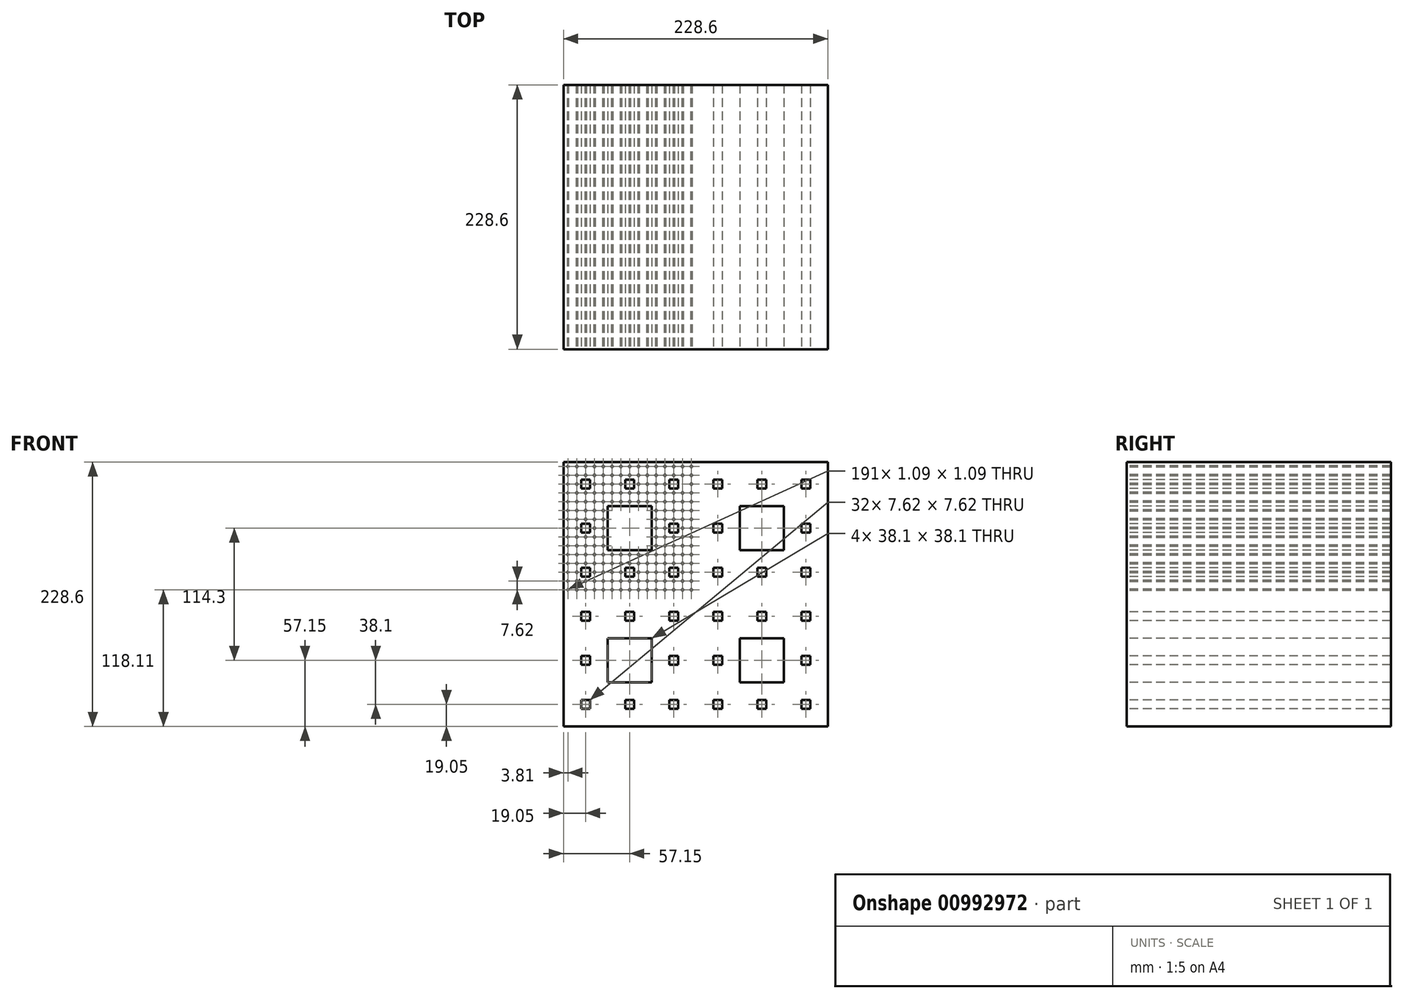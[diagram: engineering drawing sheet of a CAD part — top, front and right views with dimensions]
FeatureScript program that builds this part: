
annotation { "Feature Type Name" : "Feature", "Feature Type Description" : "" }
export const myFeature = defineFeature(function(context is Context, id is Id, definition is map)
    precondition{}
    {
        {
            var Q0;
            Q0=qCreatedBy(makeId("Front.planeOp"),FACE);
            var sketch = newSketch(context, id + "F0", { "sketchPlane" : qUnion([Q0])});
            skLineSegment(sketch, "E0.bottom", {"start": v(114.3, 114.3) * mm, "end": v(-114.3, 114.3) * mm});
            skLineSegment(sketch, "E0.top", {"start": v(114.3, -114.3) * mm, "end": v(-114.3, -114.3) * mm});
            skLineSegment(sketch, "E0.left", {"start": v(114.3, 114.3) * mm, "end": v(114.3, -114.3) * mm});
            skLineSegment(sketch, "E0.right", {"start": v(-114.3, 114.3) * mm, "end": v(-114.3, -114.3) * mm});
            skPoint(sketch, "E0.middle", {"position": v(0, 0) * mm});
            skSolve(sketch);
        }
        {
            var Q0;
            Q0 = qSketchRegion(id + "F0", true);
            extrude(context, id + "F1", {"entities" : qUnion([Q0]), "endBound" : BoundingType.SYMMETRIC, "depth" : 228.6 * mm, "offsetDistance" : 25.4 * mm});
        }
        {
            var Q0;
            Q0=makeQuery(id+"F1.opExtrude","CAP_FACE",FACE,{"disambiguationData":[OSD([sQuery(id+"F0.wireOp",EDGE,"E0.bottom"),sQuery(id+"F0.wireOp",EDGE,"E0.top"),sQuery(id+"F0.wireOp",EDGE,"E0.left"),sQuery(id+"F0.wireOp",EDGE,"E0.right")])],"isStart":false});
            var sketch = newSketch(context, id + "F2", { "sketchPlane" : qUnion([Q0])});
            skLineSegment(sketch, "E1", {"start": v(0, -114.3) * mm, "end": v(0, 114.3) * mm, "construction": true});
            skLineSegment(sketch, "E2", {"start": v(-114.3, 0) * mm, "end": v(114.3, 0) * mm, "construction": true});
            skLineSegment(sketch, "E3.bottom", {"start": v(-38.1, 76.2) * mm, "end": v(-76.2, 76.2) * mm});
            skLineSegment(sketch, "E3.top", {"start": v(-38.1, 38.1) * mm, "end": v(-76.2, 38.1) * mm});
            skLineSegment(sketch, "E3.left", {"start": v(-38.1, 76.2) * mm, "end": v(-38.1, 38.1) * mm});
            skLineSegment(sketch, "E3.right", {"start": v(-76.2, 76.2) * mm, "end": v(-76.2, 38.1) * mm});
            skPoint(sketch, "E4", {"position": v(-57.15, 95.25) * mm});
            skLineSegment(sketch, "E5.top", {"start": v(-38.1, 114.3) * mm, "end": v(-76.2, 114.3) * mm});
            skLineSegment(sketch, "E5.left", {"start": v(-38.1, 76.2) * mm, "end": v(-38.1, 114.3) * mm, "construction": true});
            skLineSegment(sketch, "E5.right", {"start": v(-76.2, 76.2) * mm, "end": v(-76.2, 114.3) * mm, "construction": true});
            skPoint(sketch, "E6", {"position": v(-19.05, 57.15) * mm});
            skPoint(sketch, "E7", {"position": v(-19.05, 95.25) * mm});
            skPoint(sketch, "E7.positionSnap0", {"position": v(-38.1, 95.25) * mm});
            skPoint(sketch, "E8", {"position": v(-57.15, 19.05) * mm});
            skPoint(sketch, "E9", {"position": v(-19.05, 19.05) * mm});
            skPoint(sketch, "E10", {"position": v(-95.25, 57.15) * mm});
            skPoint(sketch, "E11", {"position": v(-95.25, 95.25) * mm});
            skPoint(sketch, "E11.positionSnap0", {"position": v(-76.2, 95.25) * mm});
            skPoint(sketch, "E12", {"position": v(-95.25, 19.05) * mm});
            skLineSegment(sketch, "E13", {"start": v(-38.1, 76.2) * mm, "end": v(0, 76.2) * mm, "construction": true});
            skLineSegment(sketch, "E14", {"start": v(-38.1, 38.1) * mm, "end": v(0, 38.1) * mm, "construction": true});
            skLineSegment(sketch, "E15", {"start": v(-38.1, 38.1) * mm, "end": v(-38.1, 0) * mm, "construction": true});
            skLineSegment(sketch, "E16", {"start": v(-76.2, 38.1) * mm, "end": v(-76.2, 0) * mm, "construction": true});
            skLineSegment(sketch, "E17", {"start": v(-76.2, 76.2) * mm, "end": v(-114.3, 76.2) * mm, "construction": true});
            skLineSegment(sketch, "E18", {"start": v(-76.2, 38.1) * mm, "end": v(-114.3, 38.1) * mm, "construction": true});
            skLineSegment(sketch, "E19.bottom", {"start": v(-91.44, 99.06) * mm, "end": v(-99.06, 99.06) * mm});
            skLineSegment(sketch, "E19.top", {"start": v(-91.44, 91.44) * mm, "end": v(-99.06, 91.44) * mm});
            skLineSegment(sketch, "E19.left", {"start": v(-91.44, 99.06) * mm, "end": v(-91.44, 91.44) * mm});
            skLineSegment(sketch, "E19.right", {"start": v(-99.06, 99.06) * mm, "end": v(-99.06, 91.44) * mm});
            skLineSegment(sketch, "E20.0.1.0", {"start": v(-91.44, 60.96) * mm, "end": v(-91.44, 53.34) * mm});
            skLineSegment(sketch, "E20.0.1.2", {"start": v(-91.44, 60.96) * mm, "end": v(-99.06, 60.96) * mm});
            skLineSegment(sketch, "E20.0.1.3", {"start": v(-99.06, 60.96) * mm, "end": v(-99.06, 53.34) * mm});
            skLineSegment(sketch, "E20.0.1.4", {"start": v(-91.44, 53.34) * mm, "end": v(-99.06, 53.34) * mm});
            skLineSegment(sketch, "E20.0.2.0", {"start": v(-91.44, 22.86) * mm, "end": v(-91.44, 15.24) * mm});
            skLineSegment(sketch, "E20.0.2.2", {"start": v(-91.44, 22.86) * mm, "end": v(-99.06, 22.86) * mm});
            skLineSegment(sketch, "E20.0.2.3", {"start": v(-99.06, 22.86) * mm, "end": v(-99.06, 15.24) * mm});
            skLineSegment(sketch, "E20.0.2.4", {"start": v(-91.44, 15.24) * mm, "end": v(-99.06, 15.24) * mm});
            skLineSegment(sketch, "E20.1.0.0", {"start": v(-53.34, 99.06) * mm, "end": v(-53.34, 91.44) * mm});
            skLineSegment(sketch, "E20.1.0.2", {"start": v(-53.34, 99.06) * mm, "end": v(-60.96, 99.06) * mm});
            skLineSegment(sketch, "E20.1.0.3", {"start": v(-60.96, 99.06) * mm, "end": v(-60.96, 91.44) * mm});
            skLineSegment(sketch, "E20.1.0.4", {"start": v(-53.34, 91.44) * mm, "end": v(-60.96, 91.44) * mm});
            skLineSegment(sketch, "E20.1.2.0", {"start": v(-53.34, 22.86) * mm, "end": v(-53.34, 15.24) * mm});
            skLineSegment(sketch, "E20.1.2.2", {"start": v(-53.34, 22.86) * mm, "end": v(-60.96, 22.86) * mm});
            skLineSegment(sketch, "E20.1.2.3", {"start": v(-60.96, 22.86) * mm, "end": v(-60.96, 15.24) * mm});
            skLineSegment(sketch, "E20.1.2.4", {"start": v(-53.34, 15.24) * mm, "end": v(-60.96, 15.24) * mm});
            skLineSegment(sketch, "E20.2.0.0", {"start": v(-15.24, 99.06) * mm, "end": v(-15.24, 91.44) * mm});
            skLineSegment(sketch, "E20.2.0.2", {"start": v(-15.24, 99.06) * mm, "end": v(-22.86, 99.06) * mm});
            skLineSegment(sketch, "E20.2.0.3", {"start": v(-22.86, 99.06) * mm, "end": v(-22.86, 91.44) * mm});
            skLineSegment(sketch, "E20.2.0.4", {"start": v(-15.24, 91.44) * mm, "end": v(-22.86, 91.44) * mm});
            skLineSegment(sketch, "E20.2.1.0", {"start": v(-15.24, 60.96) * mm, "end": v(-15.24, 53.34) * mm});
            skLineSegment(sketch, "E20.2.1.2", {"start": v(-15.24, 60.96) * mm, "end": v(-22.86, 60.96) * mm});
            skLineSegment(sketch, "E20.2.1.3", {"start": v(-22.86, 60.96) * mm, "end": v(-22.86, 53.34) * mm});
            skLineSegment(sketch, "E20.2.1.4", {"start": v(-15.24, 53.34) * mm, "end": v(-22.86, 53.34) * mm});
            skLineSegment(sketch, "E20.2.2.0", {"start": v(-15.24, 22.86) * mm, "end": v(-15.24, 15.24) * mm});
            skLineSegment(sketch, "E20.2.2.2", {"start": v(-15.24, 22.86) * mm, "end": v(-22.86, 22.86) * mm});
            skLineSegment(sketch, "E20.2.2.3", {"start": v(-22.86, 22.86) * mm, "end": v(-22.86, 15.24) * mm});
            skLineSegment(sketch, "E20.2.2.4", {"start": v(-15.24, 15.24) * mm, "end": v(-22.86, 15.24) * mm});
            skLineSegment(sketch, "E20.direction1", {"start": v(-99.06, 91.44) * mm, "end": v(-60.96, 91.44) * mm, "construction": true});
            skLineSegment(sketch, "E20.direction2", {"start": v(-99.06, 91.44) * mm, "end": v(-99.06, 53.34) * mm, "construction": true});
            skLineSegment(sketch, "E21.0.1.0", {"start": v(-38.1, -76.2) * mm, "end": v(0, -76.2) * mm, "construction": true});
            skLineSegment(sketch, "E21.0.1.1", {"start": v(-38.1, 0) * mm, "end": v(-76.2, 0) * mm});
            skLineSegment(sketch, "E21.0.1.2", {"start": v(-76.2, -76.2) * mm, "end": v(-114.3, -76.2) * mm, "construction": true});
            skLineSegment(sketch, "E21.0.1.3", {"start": v(-38.1, -38.1) * mm, "end": v(-38.1, 0) * mm, "construction": true});
            skPoint(sketch, "E21.0.1.4", {"position": v(-19.05, -95.25) * mm});
            skPoint(sketch, "E21.0.1.5", {"position": v(-95.25, -95.25) * mm});
            skLineSegment(sketch, "E21.0.1.6", {"start": v(-76.2, -76.2) * mm, "end": v(-76.2, -114.3) * mm, "construction": true});
            skLineSegment(sketch, "E21.0.1.7", {"start": v(-76.2, -38.1) * mm, "end": v(-76.2, -76.2) * mm});
            skLineSegment(sketch, "E21.0.1.8", {"start": v(-38.1, -38.1) * mm, "end": v(-38.1, -76.2) * mm});
            skPoint(sketch, "E21.0.1.9", {"position": v(-57.15, -95.25) * mm});
            skLineSegment(sketch, "E21.0.1.10", {"start": v(-38.1, -38.1) * mm, "end": v(0, -38.1) * mm, "construction": true});
            skPoint(sketch, "E21.0.1.11", {"position": v(-19.05, -57.15) * mm});
            skPoint(sketch, "E21.0.1.12", {"position": v(-38.1, -19.05) * mm});
            skLineSegment(sketch, "E21.0.1.13", {"start": v(-38.1, -76.2) * mm, "end": v(-38.1, -114.3) * mm, "construction": true});
            skLineSegment(sketch, "E21.0.1.14", {"start": v(-99.06, -22.86) * mm, "end": v(-60.96, -22.86) * mm, "construction": true});
            skPoint(sketch, "E21.0.1.15", {"position": v(-95.25, -57.15) * mm});
            skPoint(sketch, "E21.0.1.16", {"position": v(-76.2, -19.05) * mm});
            skLineSegment(sketch, "E21.0.1.17", {"start": v(-38.1, -38.1) * mm, "end": v(-76.2, -38.1) * mm});
            skLineSegment(sketch, "E21.0.1.18", {"start": v(-76.2, -38.1) * mm, "end": v(-114.3, -38.1) * mm, "construction": true});
            skLineSegment(sketch, "E21.0.1.19", {"start": v(-76.2, -38.1) * mm, "end": v(-76.2, 0) * mm, "construction": true});
            skLineSegment(sketch, "E21.0.1.20", {"start": v(-99.06, -22.86) * mm, "end": v(-99.06, -60.96) * mm, "construction": true});
            skLineSegment(sketch, "E21.0.1.21", {"start": v(-38.1, -76.2) * mm, "end": v(-76.2, -76.2) * mm});
            skPoint(sketch, "E21.0.1.22", {"position": v(-19.05, -19.05) * mm});
            skPoint(sketch, "E21.0.1.23", {"position": v(-95.25, -19.05) * mm});
            skPoint(sketch, "E21.0.1.24", {"position": v(-57.15, -19.05) * mm});
            skPoint(sketch, "E21.0.1.25", {"position": v(-95.25, -57.15) * mm});
            skPoint(sketch, "E21.0.1.26", {"position": v(-95.25, -95.25) * mm});
            skPoint(sketch, "E21.0.1.27", {"position": v(-19.05, -95.25) * mm});
            skPoint(sketch, "E21.0.1.28", {"position": v(-57.15, -19.05) * mm});
            skPoint(sketch, "E21.0.1.29", {"position": v(-19.05, -57.15) * mm});
            skPoint(sketch, "E21.0.1.30", {"position": v(-95.25, -19.05) * mm});
            skPoint(sketch, "E21.0.1.31", {"position": v(-19.05, -19.05) * mm});
            skPoint(sketch, "E21.0.1.32", {"position": v(-57.15, -95.25) * mm});
            skLineSegment(sketch, "E21.0.1.33", {"start": v(-38.1, -38.1) * mm, "end": v(-76.2, -38.1) * mm});
            skLineSegment(sketch, "E21.0.1.34", {"start": v(-99.06, -15.24) * mm, "end": v(-99.06, -22.86) * mm});
            skPoint(sketch, "E21.0.1.35", {"position": v(-19.05, -57.15) * mm});
            skPoint(sketch, "E21.0.1.36", {"position": v(-19.05, -19.05) * mm});
            skPoint(sketch, "E21.0.1.37", {"position": v(-95.25, -57.15) * mm});
            skPoint(sketch, "E21.0.1.38", {"position": v(-57.15, -95.25) * mm});
            skPoint(sketch, "E21.0.1.39", {"position": v(-57.15, -19.05) * mm});
            skPoint(sketch, "E21.0.1.40", {"position": v(-19.05, -95.25) * mm});
            skLineSegment(sketch, "E21.0.1.41", {"start": v(-91.44, -15.24) * mm, "end": v(-99.06, -15.24) * mm});
            skLineSegment(sketch, "E21.0.1.42", {"start": v(-91.44, -22.86) * mm, "end": v(-99.06, -22.86) * mm});
            skLineSegment(sketch, "E21.0.1.43", {"start": v(-91.44, -15.24) * mm, "end": v(-91.44, -22.86) * mm});
            skPoint(sketch, "E21.0.1.44", {"position": v(-95.25, -95.25) * mm});
            skLineSegment(sketch, "E21.0.1.45", {"start": v(-91.44, -91.44) * mm, "end": v(-91.44, -99.06) * mm});
            skLineSegment(sketch, "E21.0.1.46", {"start": v(-22.86, -53.34) * mm, "end": v(-22.86, -60.96) * mm});
            skLineSegment(sketch, "E21.0.1.47", {"start": v(-15.24, -15.24) * mm, "end": v(-22.86, -15.24) * mm});
            skLineSegment(sketch, "E21.0.1.48", {"start": v(-15.24, -53.34) * mm, "end": v(-22.86, -53.34) * mm});
            skLineSegment(sketch, "E21.0.1.49", {"start": v(-99.06, -91.44) * mm, "end": v(-99.06, -99.06) * mm});
            skLineSegment(sketch, "E21.0.1.50", {"start": v(-91.44, -53.34) * mm, "end": v(-91.44, -60.96) * mm});
            skLineSegment(sketch, "E21.0.1.51", {"start": v(-60.96, -91.44) * mm, "end": v(-60.96, -99.06) * mm});
            skLineSegment(sketch, "E21.0.1.52", {"start": v(-15.24, -15.24) * mm, "end": v(-15.24, -22.86) * mm});
            skLineSegment(sketch, "E21.0.1.53", {"start": v(-91.44, -53.34) * mm, "end": v(-99.06, -53.34) * mm});
            skLineSegment(sketch, "E21.0.1.54", {"start": v(-53.34, -91.44) * mm, "end": v(-60.96, -91.44) * mm});
            skLineSegment(sketch, "E21.0.1.55", {"start": v(-22.86, -91.44) * mm, "end": v(-22.86, -99.06) * mm});
            skLineSegment(sketch, "E21.0.1.56", {"start": v(-15.24, -53.34) * mm, "end": v(-15.24, -60.96) * mm});
            skLineSegment(sketch, "E21.0.1.57", {"start": v(-91.44, -99.06) * mm, "end": v(-99.06, -99.06) * mm});
            skLineSegment(sketch, "E21.0.1.58", {"start": v(-91.44, -91.44) * mm, "end": v(-99.06, -91.44) * mm});
            skLineSegment(sketch, "E21.0.1.59", {"start": v(-22.86, -15.24) * mm, "end": v(-22.86, -22.86) * mm});
            skLineSegment(sketch, "E21.0.1.60", {"start": v(-15.24, -99.06) * mm, "end": v(-22.86, -99.06) * mm});
            skPoint(sketch, "E21.0.1.61", {"position": v(-57.15, -19.05) * mm});
            skLineSegment(sketch, "E21.0.1.62", {"start": v(-53.34, -99.06) * mm, "end": v(-60.96, -99.06) * mm});
            skLineSegment(sketch, "E21.0.1.63", {"start": v(-53.34, -91.44) * mm, "end": v(-53.34, -99.06) * mm});
            skLineSegment(sketch, "E21.0.1.64", {"start": v(-99.06, -53.34) * mm, "end": v(-99.06, -60.96) * mm});
            skLineSegment(sketch, "E21.0.1.65", {"start": v(-15.24, -91.44) * mm, "end": v(-15.24, -99.06) * mm});
            skLineSegment(sketch, "E21.0.1.66", {"start": v(-15.24, -60.96) * mm, "end": v(-22.86, -60.96) * mm});
            skLineSegment(sketch, "E21.0.1.67", {"start": v(-15.24, -91.44) * mm, "end": v(-22.86, -91.44) * mm});
            skLineSegment(sketch, "E21.0.1.68", {"start": v(-91.44, -60.96) * mm, "end": v(-99.06, -60.96) * mm});
            skLineSegment(sketch, "E21.0.1.69", {"start": v(-15.24, -22.86) * mm, "end": v(-22.86, -22.86) * mm});
            skLineSegment(sketch, "E21.0.1.70", {"start": v(-53.34, -15.24) * mm, "end": v(-53.34, -22.86) * mm});
            skLineSegment(sketch, "E21.0.1.71", {"start": v(-60.96, -15.24) * mm, "end": v(-60.96, -22.86) * mm});
            skLineSegment(sketch, "E21.0.1.72", {"start": v(-53.34, -22.86) * mm, "end": v(-60.96, -22.86) * mm});
            skLineSegment(sketch, "E21.0.1.73", {"start": v(-53.34, -15.24) * mm, "end": v(-60.96, -15.24) * mm});
            skLineSegment(sketch, "E21.1.0.0", {"start": v(76.2, 38.1) * mm, "end": v(114.3, 38.1) * mm, "construction": true});
            skLineSegment(sketch, "E21.1.0.1", {"start": v(76.2, 114.3) * mm, "end": v(38.1, 114.3) * mm});
            skLineSegment(sketch, "E21.1.0.2", {"start": v(38.1, 38.1) * mm, "end": v(0, 38.1) * mm, "construction": true});
            skLineSegment(sketch, "E21.1.0.3", {"start": v(76.2, 76.2) * mm, "end": v(76.2, 114.3) * mm, "construction": true});
            skPoint(sketch, "E21.1.0.4", {"position": v(95.25, 19.05) * mm});
            skPoint(sketch, "E21.1.0.5", {"position": v(19.05, 19.05) * mm});
            skLineSegment(sketch, "E21.1.0.6", {"start": v(38.1, 38.1) * mm, "end": v(38.1, 0) * mm, "construction": true});
            skLineSegment(sketch, "E21.1.0.7", {"start": v(38.1, 76.2) * mm, "end": v(38.1, 38.1) * mm});
            skLineSegment(sketch, "E21.1.0.8", {"start": v(76.2, 76.2) * mm, "end": v(76.2, 38.1) * mm});
            skPoint(sketch, "E21.1.0.9", {"position": v(57.15, 19.05) * mm});
            skLineSegment(sketch, "E21.1.0.10", {"start": v(76.2, 76.2) * mm, "end": v(114.3, 76.2) * mm, "construction": true});
            skPoint(sketch, "E21.1.0.11", {"position": v(95.25, 57.15) * mm});
            skPoint(sketch, "E21.1.0.12", {"position": v(76.2, 95.25) * mm});
            skLineSegment(sketch, "E21.1.0.13", {"start": v(76.2, 38.1) * mm, "end": v(76.2, 0) * mm, "construction": true});
            skLineSegment(sketch, "E21.1.0.14", {"start": v(15.24, 91.44) * mm, "end": v(53.34, 91.44) * mm, "construction": true});
            skPoint(sketch, "E21.1.0.15", {"position": v(19.05, 57.15) * mm});
            skPoint(sketch, "E21.1.0.16", {"position": v(38.1, 95.25) * mm});
            skLineSegment(sketch, "E21.1.0.17", {"start": v(76.2, 76.2) * mm, "end": v(38.1, 76.2) * mm});
            skLineSegment(sketch, "E21.1.0.18", {"start": v(38.1, 76.2) * mm, "end": v(0, 76.2) * mm, "construction": true});
            skLineSegment(sketch, "E21.1.0.19", {"start": v(38.1, 76.2) * mm, "end": v(38.1, 114.3) * mm, "construction": true});
            skLineSegment(sketch, "E21.1.0.20", {"start": v(15.24, 91.44) * mm, "end": v(15.24, 53.34) * mm, "construction": true});
            skLineSegment(sketch, "E21.1.0.21", {"start": v(76.2, 38.1) * mm, "end": v(38.1, 38.1) * mm});
            skPoint(sketch, "E21.1.0.22", {"position": v(95.25, 95.25) * mm});
            skPoint(sketch, "E21.1.0.23", {"position": v(19.05, 95.25) * mm});
            skPoint(sketch, "E21.1.0.24", {"position": v(57.15, 95.25) * mm});
            skPoint(sketch, "E21.1.0.25", {"position": v(19.05, 57.15) * mm});
            skPoint(sketch, "E21.1.0.26", {"position": v(19.05, 19.05) * mm});
            skPoint(sketch, "E21.1.0.27", {"position": v(95.25, 19.05) * mm});
            skPoint(sketch, "E21.1.0.28", {"position": v(57.15, 95.25) * mm});
            skPoint(sketch, "E21.1.0.29", {"position": v(95.25, 57.15) * mm});
            skPoint(sketch, "E21.1.0.30", {"position": v(19.05, 95.25) * mm});
            skPoint(sketch, "E21.1.0.31", {"position": v(95.25, 95.25) * mm});
            skPoint(sketch, "E21.1.0.32", {"position": v(57.15, 19.05) * mm});
            skLineSegment(sketch, "E21.1.0.33", {"start": v(76.2, 76.2) * mm, "end": v(38.1, 76.2) * mm});
            skLineSegment(sketch, "E21.1.0.34", {"start": v(15.24, 99.06) * mm, "end": v(15.24, 91.44) * mm});
            skPoint(sketch, "E21.1.0.35", {"position": v(95.25, 57.15) * mm});
            skPoint(sketch, "E21.1.0.36", {"position": v(95.25, 95.25) * mm});
            skPoint(sketch, "E21.1.0.37", {"position": v(19.05, 57.15) * mm});
            skPoint(sketch, "E21.1.0.38", {"position": v(57.15, 19.05) * mm});
            skPoint(sketch, "E21.1.0.39", {"position": v(57.15, 95.25) * mm});
            skPoint(sketch, "E21.1.0.40", {"position": v(95.25, 19.05) * mm});
            skLineSegment(sketch, "E21.1.0.41", {"start": v(22.86, 99.06) * mm, "end": v(15.24, 99.06) * mm});
            skLineSegment(sketch, "E21.1.0.42", {"start": v(22.86, 91.44) * mm, "end": v(15.24, 91.44) * mm});
            skLineSegment(sketch, "E21.1.0.43", {"start": v(22.86, 99.06) * mm, "end": v(22.86, 91.44) * mm});
            skPoint(sketch, "E21.1.0.44", {"position": v(19.05, 19.05) * mm});
            skLineSegment(sketch, "E21.1.0.45", {"start": v(22.86, 22.86) * mm, "end": v(22.86, 15.24) * mm});
            skLineSegment(sketch, "E21.1.0.46", {"start": v(91.44, 60.96) * mm, "end": v(91.44, 53.34) * mm});
            skLineSegment(sketch, "E21.1.0.47", {"start": v(99.06, 99.06) * mm, "end": v(91.44, 99.06) * mm});
            skLineSegment(sketch, "E21.1.0.48", {"start": v(99.06, 60.96) * mm, "end": v(91.44, 60.96) * mm});
            skLineSegment(sketch, "E21.1.0.49", {"start": v(15.24, 22.86) * mm, "end": v(15.24, 15.24) * mm});
            skLineSegment(sketch, "E21.1.0.50", {"start": v(22.86, 60.96) * mm, "end": v(22.86, 53.34) * mm});
            skLineSegment(sketch, "E21.1.0.51", {"start": v(53.34, 22.86) * mm, "end": v(53.34, 15.24) * mm});
            skLineSegment(sketch, "E21.1.0.52", {"start": v(99.06, 99.06) * mm, "end": v(99.06, 91.44) * mm});
            skLineSegment(sketch, "E21.1.0.53", {"start": v(22.86, 60.96) * mm, "end": v(15.24, 60.96) * mm});
            skLineSegment(sketch, "E21.1.0.54", {"start": v(60.96, 22.86) * mm, "end": v(53.34, 22.86) * mm});
            skLineSegment(sketch, "E21.1.0.55", {"start": v(91.44, 22.86) * mm, "end": v(91.44, 15.24) * mm});
            skLineSegment(sketch, "E21.1.0.56", {"start": v(99.06, 60.96) * mm, "end": v(99.06, 53.34) * mm});
            skLineSegment(sketch, "E21.1.0.57", {"start": v(22.86, 15.24) * mm, "end": v(15.24, 15.24) * mm});
            skLineSegment(sketch, "E21.1.0.58", {"start": v(22.86, 22.86) * mm, "end": v(15.24, 22.86) * mm});
            skLineSegment(sketch, "E21.1.0.59", {"start": v(91.44, 99.06) * mm, "end": v(91.44, 91.44) * mm});
            skLineSegment(sketch, "E21.1.0.60", {"start": v(99.06, 15.24) * mm, "end": v(91.44, 15.24) * mm});
            skPoint(sketch, "E21.1.0.61", {"position": v(57.15, 95.25) * mm});
            skLineSegment(sketch, "E21.1.0.62", {"start": v(60.96, 15.24) * mm, "end": v(53.34, 15.24) * mm});
            skLineSegment(sketch, "E21.1.0.63", {"start": v(60.96, 22.86) * mm, "end": v(60.96, 15.24) * mm});
            skLineSegment(sketch, "E21.1.0.64", {"start": v(15.24, 60.96) * mm, "end": v(15.24, 53.34) * mm});
            skLineSegment(sketch, "E21.1.0.65", {"start": v(99.06, 22.86) * mm, "end": v(99.06, 15.24) * mm});
            skLineSegment(sketch, "E21.1.0.66", {"start": v(99.06, 53.34) * mm, "end": v(91.44, 53.34) * mm});
            skLineSegment(sketch, "E21.1.0.67", {"start": v(99.06, 22.86) * mm, "end": v(91.44, 22.86) * mm});
            skLineSegment(sketch, "E21.1.0.68", {"start": v(22.86, 53.34) * mm, "end": v(15.24, 53.34) * mm});
            skLineSegment(sketch, "E21.1.0.69", {"start": v(99.06, 91.44) * mm, "end": v(91.44, 91.44) * mm});
            skLineSegment(sketch, "E21.1.0.70", {"start": v(60.96, 99.06) * mm, "end": v(60.96, 91.44) * mm});
            skLineSegment(sketch, "E21.1.0.71", {"start": v(53.34, 99.06) * mm, "end": v(53.34, 91.44) * mm});
            skLineSegment(sketch, "E21.1.0.72", {"start": v(60.96, 91.44) * mm, "end": v(53.34, 91.44) * mm});
            skLineSegment(sketch, "E21.1.0.73", {"start": v(60.96, 99.06) * mm, "end": v(53.34, 99.06) * mm});
            skLineSegment(sketch, "E21.1.1.0", {"start": v(76.2, -76.2) * mm, "end": v(114.3, -76.2) * mm, "construction": true});
            skLineSegment(sketch, "E21.1.1.1", {"start": v(76.2, 0) * mm, "end": v(38.1, 0) * mm});
            skLineSegment(sketch, "E21.1.1.2", {"start": v(38.1, -76.2) * mm, "end": v(0, -76.2) * mm, "construction": true});
            skLineSegment(sketch, "E21.1.1.3", {"start": v(76.2, -38.1) * mm, "end": v(76.2, 0) * mm, "construction": true});
            skPoint(sketch, "E21.1.1.4", {"position": v(95.25, -95.25) * mm});
            skPoint(sketch, "E21.1.1.5", {"position": v(19.05, -95.25) * mm});
            skLineSegment(sketch, "E21.1.1.6", {"start": v(38.1, -76.2) * mm, "end": v(38.1, -114.3) * mm, "construction": true});
            skLineSegment(sketch, "E21.1.1.7", {"start": v(38.1, -38.1) * mm, "end": v(38.1, -76.2) * mm});
            skLineSegment(sketch, "E21.1.1.8", {"start": v(76.2, -38.1) * mm, "end": v(76.2, -76.2) * mm});
            skPoint(sketch, "E21.1.1.9", {"position": v(57.15, -95.25) * mm});
            skLineSegment(sketch, "E21.1.1.10", {"start": v(76.2, -38.1) * mm, "end": v(114.3, -38.1) * mm, "construction": true});
            skPoint(sketch, "E21.1.1.11", {"position": v(95.25, -57.15) * mm});
            skPoint(sketch, "E21.1.1.12", {"position": v(76.2, -19.05) * mm});
            skLineSegment(sketch, "E21.1.1.13", {"start": v(76.2, -76.2) * mm, "end": v(76.2, -114.3) * mm, "construction": true});
            skLineSegment(sketch, "E21.1.1.14", {"start": v(15.24, -22.86) * mm, "end": v(53.34, -22.86) * mm, "construction": true});
            skPoint(sketch, "E21.1.1.15", {"position": v(19.05, -57.15) * mm});
            skPoint(sketch, "E21.1.1.16", {"position": v(38.1, -19.05) * mm});
            skLineSegment(sketch, "E21.1.1.17", {"start": v(76.2, -38.1) * mm, "end": v(38.1, -38.1) * mm});
            skLineSegment(sketch, "E21.1.1.18", {"start": v(38.1, -38.1) * mm, "end": v(0, -38.1) * mm, "construction": true});
            skLineSegment(sketch, "E21.1.1.19", {"start": v(38.1, -38.1) * mm, "end": v(38.1, 0) * mm, "construction": true});
            skLineSegment(sketch, "E21.1.1.20", {"start": v(15.24, -22.86) * mm, "end": v(15.24, -60.96) * mm, "construction": true});
            skLineSegment(sketch, "E21.1.1.21", {"start": v(76.2, -76.2) * mm, "end": v(38.1, -76.2) * mm});
            skPoint(sketch, "E21.1.1.22", {"position": v(95.25, -19.05) * mm});
            skPoint(sketch, "E21.1.1.23", {"position": v(19.05, -19.05) * mm});
            skPoint(sketch, "E21.1.1.24", {"position": v(57.15, -19.05) * mm});
            skPoint(sketch, "E21.1.1.25", {"position": v(19.05, -57.15) * mm});
            skPoint(sketch, "E21.1.1.26", {"position": v(19.05, -95.25) * mm});
            skPoint(sketch, "E21.1.1.27", {"position": v(95.25, -95.25) * mm});
            skPoint(sketch, "E21.1.1.28", {"position": v(57.15, -19.05) * mm});
            skPoint(sketch, "E21.1.1.29", {"position": v(95.25, -57.15) * mm});
            skPoint(sketch, "E21.1.1.30", {"position": v(19.05, -19.05) * mm});
            skPoint(sketch, "E21.1.1.31", {"position": v(95.25, -19.05) * mm});
            skPoint(sketch, "E21.1.1.32", {"position": v(57.15, -95.25) * mm});
            skLineSegment(sketch, "E21.1.1.33", {"start": v(76.2, -38.1) * mm, "end": v(38.1, -38.1) * mm});
            skLineSegment(sketch, "E21.1.1.34", {"start": v(15.24, -15.24) * mm, "end": v(15.24, -22.86) * mm});
            skPoint(sketch, "E21.1.1.35", {"position": v(95.25, -57.15) * mm});
            skPoint(sketch, "E21.1.1.36", {"position": v(95.25, -19.05) * mm});
            skPoint(sketch, "E21.1.1.37", {"position": v(19.05, -57.15) * mm});
            skPoint(sketch, "E21.1.1.38", {"position": v(57.15, -95.25) * mm});
            skPoint(sketch, "E21.1.1.39", {"position": v(57.15, -19.05) * mm});
            skPoint(sketch, "E21.1.1.40", {"position": v(95.25, -95.25) * mm});
            skLineSegment(sketch, "E21.1.1.41", {"start": v(22.86, -15.24) * mm, "end": v(15.24, -15.24) * mm});
            skLineSegment(sketch, "E21.1.1.42", {"start": v(22.86, -22.86) * mm, "end": v(15.24, -22.86) * mm});
            skLineSegment(sketch, "E21.1.1.43", {"start": v(22.86, -15.24) * mm, "end": v(22.86, -22.86) * mm});
            skPoint(sketch, "E21.1.1.44", {"position": v(19.05, -95.25) * mm});
            skLineSegment(sketch, "E21.1.1.45", {"start": v(22.86, -91.44) * mm, "end": v(22.86, -99.06) * mm});
            skLineSegment(sketch, "E21.1.1.46", {"start": v(91.44, -53.34) * mm, "end": v(91.44, -60.96) * mm});
            skLineSegment(sketch, "E21.1.1.47", {"start": v(99.06, -15.24) * mm, "end": v(91.44, -15.24) * mm});
            skLineSegment(sketch, "E21.1.1.48", {"start": v(99.06, -53.34) * mm, "end": v(91.44, -53.34) * mm});
            skLineSegment(sketch, "E21.1.1.49", {"start": v(15.24, -91.44) * mm, "end": v(15.24, -99.06) * mm});
            skLineSegment(sketch, "E21.1.1.50", {"start": v(22.86, -53.34) * mm, "end": v(22.86, -60.96) * mm});
            skLineSegment(sketch, "E21.1.1.51", {"start": v(53.34, -91.44) * mm, "end": v(53.34, -99.06) * mm});
            skLineSegment(sketch, "E21.1.1.52", {"start": v(99.06, -15.24) * mm, "end": v(99.06, -22.86) * mm});
            skLineSegment(sketch, "E21.1.1.53", {"start": v(22.86, -53.34) * mm, "end": v(15.24, -53.34) * mm});
            skLineSegment(sketch, "E21.1.1.54", {"start": v(60.96, -91.44) * mm, "end": v(53.34, -91.44) * mm});
            skLineSegment(sketch, "E21.1.1.55", {"start": v(91.44, -91.44) * mm, "end": v(91.44, -99.06) * mm});
            skLineSegment(sketch, "E21.1.1.56", {"start": v(99.06, -53.34) * mm, "end": v(99.06, -60.96) * mm});
            skLineSegment(sketch, "E21.1.1.57", {"start": v(22.86, -99.06) * mm, "end": v(15.24, -99.06) * mm});
            skLineSegment(sketch, "E21.1.1.58", {"start": v(22.86, -91.44) * mm, "end": v(15.24, -91.44) * mm});
            skLineSegment(sketch, "E21.1.1.59", {"start": v(91.44, -15.24) * mm, "end": v(91.44, -22.86) * mm});
            skLineSegment(sketch, "E21.1.1.60", {"start": v(99.06, -99.06) * mm, "end": v(91.44, -99.06) * mm});
            skPoint(sketch, "E21.1.1.61", {"position": v(57.15, -19.05) * mm});
            skLineSegment(sketch, "E21.1.1.62", {"start": v(60.96, -99.06) * mm, "end": v(53.34, -99.06) * mm});
            skLineSegment(sketch, "E21.1.1.63", {"start": v(60.96, -91.44) * mm, "end": v(60.96, -99.06) * mm});
            skLineSegment(sketch, "E21.1.1.64", {"start": v(15.24, -53.34) * mm, "end": v(15.24, -60.96) * mm});
            skLineSegment(sketch, "E21.1.1.65", {"start": v(99.06, -91.44) * mm, "end": v(99.06, -99.06) * mm});
            skLineSegment(sketch, "E21.1.1.66", {"start": v(99.06, -60.96) * mm, "end": v(91.44, -60.96) * mm});
            skLineSegment(sketch, "E21.1.1.67", {"start": v(99.06, -91.44) * mm, "end": v(91.44, -91.44) * mm});
            skLineSegment(sketch, "E21.1.1.68", {"start": v(22.86, -60.96) * mm, "end": v(15.24, -60.96) * mm});
            skLineSegment(sketch, "E21.1.1.69", {"start": v(99.06, -22.86) * mm, "end": v(91.44, -22.86) * mm});
            skLineSegment(sketch, "E21.1.1.70", {"start": v(60.96, -15.24) * mm, "end": v(60.96, -22.86) * mm});
            skLineSegment(sketch, "E21.1.1.71", {"start": v(53.34, -15.24) * mm, "end": v(53.34, -22.86) * mm});
            skLineSegment(sketch, "E21.1.1.72", {"start": v(60.96, -22.86) * mm, "end": v(53.34, -22.86) * mm});
            skLineSegment(sketch, "E21.1.1.73", {"start": v(60.96, -15.24) * mm, "end": v(53.34, -15.24) * mm});
            skLineSegment(sketch, "E21.direction1", {"start": v(-99.06, 15.24) * mm, "end": v(15.24, 15.24) * mm, "construction": true});
            skLineSegment(sketch, "E21.direction2", {"start": v(-99.06, 15.24) * mm, "end": v(-99.06, -99.06) * mm, "construction": true});
            skSolve(sketch);
        }
        {
            var Q0;
            Q0 = qSketchRegion(id + "F2", true);
            extrude(context, id + "F3", {"entities" : qUnion([Q0]), "operationType" : NewBodyOperationType.REMOVE, "oppositeDirection" : true, "depth" : 228.6 * mm, "offsetDistance" : 25.4 * mm});
        }
        {
            var Q0;
            Q0=makeQuery(id+"F1.opExtrude","CAP_FACE",FACE,{"disambiguationData":[OSD([sQuery(id+"F0.wireOp",EDGE,"E0.bottom"),sQuery(id+"F0.wireOp",EDGE,"E0.top"),sQuery(id+"F0.wireOp",EDGE,"E0.left"),sQuery(id+"F0.wireOp",EDGE,"E0.right")])],"isStart":false});
            var sketch = newSketch(context, id + "F4", { "sketchPlane" : qUnion([Q0])});
            skPoint(sketch, "E22.middle.positionSnap0", {"position": v(-95.25, 99.06) * mm});
            skPoint(sketch, "E22.middle.positionSnap1", {"position": v(-91.44, 95.25) * mm});
            skPoint(sketch, "E22.centerSnap0", {"position": v(-95.25, 99.06) * mm});
            skPoint(sketch, "E22.centerSnap1", {"position": v(-91.44, 95.25) * mm});
            skPoint(sketch, "E23.startSnap0", {"position": v(-83.82, 106.68) * mm});
            skPoint(sketch, "E24.startSnap0", {"position": v(-99.06, 83.82) * mm});
            skPoint(sketch, "E25", {"position": v(-110.49, 110.5) * mm});
            skPoint(sketch, "E25.positionSnap0", {"position": v(-106.68, 110.5) * mm});
            skLineSegment(sketch, "E26.bottom", {"start": v(-109.95, 111.03) * mm, "end": v(-111.03, 111.03) * mm});
            skLineSegment(sketch, "E26.top", {"start": v(-109.95, 109.95) * mm, "end": v(-111.03, 109.95) * mm});
            skLineSegment(sketch, "E26.left", {"start": v(-109.95, 111.03) * mm, "end": v(-109.95, 109.95) * mm});
            skLineSegment(sketch, "E26.right", {"start": v(-111.03, 111.03) * mm, "end": v(-111.03, 109.95) * mm});
            skLineSegment(sketch, "E27.0.1.0", {"start": v(-109.95, 102.33) * mm, "end": v(-111.03, 102.33) * mm});
            skLineSegment(sketch, "E27.0.1.1", {"start": v(-109.95, 103.41) * mm, "end": v(-109.95, 102.33) * mm});
            skLineSegment(sketch, "E27.0.1.2", {"start": v(-111.03, 103.41) * mm, "end": v(-111.03, 102.33) * mm});
            skLineSegment(sketch, "E27.0.1.3", {"start": v(-109.95, 103.41) * mm, "end": v(-111.03, 103.41) * mm});
            skPoint(sketch, "E27.0.1.4", {"position": v(-110.49, 102.87) * mm});
            skPoint(sketch, "E27.0.1.5", {"position": v(-110.49, 102.87) * mm});
            skLineSegment(sketch, "E27.0.2.0", {"start": v(-109.95, 94.7) * mm, "end": v(-111.03, 94.7) * mm});
            skLineSegment(sketch, "E27.0.2.1", {"start": v(-109.95, 95.8) * mm, "end": v(-109.95, 94.7) * mm});
            skLineSegment(sketch, "E27.0.2.2", {"start": v(-111.03, 95.8) * mm, "end": v(-111.03, 94.7) * mm});
            skLineSegment(sketch, "E27.0.2.3", {"start": v(-109.95, 95.8) * mm, "end": v(-111.03, 95.8) * mm});
            skPoint(sketch, "E27.0.2.4", {"position": v(-110.49, 95.25) * mm});
            skPoint(sketch, "E27.0.2.5", {"position": v(-110.49, 95.25) * mm});
            skLineSegment(sketch, "E27.0.3.0", {"start": v(-109.95, 87.09) * mm, "end": v(-111.03, 87.09) * mm});
            skLineSegment(sketch, "E27.0.3.1", {"start": v(-109.95, 88.17) * mm, "end": v(-109.95, 87.09) * mm});
            skLineSegment(sketch, "E27.0.3.2", {"start": v(-111.03, 88.17) * mm, "end": v(-111.03, 87.09) * mm});
            skLineSegment(sketch, "E27.0.3.3", {"start": v(-109.95, 88.17) * mm, "end": v(-111.03, 88.17) * mm});
            skPoint(sketch, "E27.0.3.4", {"position": v(-110.49, 87.63) * mm});
            skPoint(sketch, "E27.0.3.5", {"position": v(-110.49, 87.63) * mm});
            skLineSegment(sketch, "E27.0.4.0", {"start": v(-109.95, 79.47) * mm, "end": v(-111.03, 79.47) * mm});
            skLineSegment(sketch, "E27.0.4.1", {"start": v(-109.95, 80.55) * mm, "end": v(-109.95, 79.47) * mm});
            skLineSegment(sketch, "E27.0.4.2", {"start": v(-111.03, 80.55) * mm, "end": v(-111.03, 79.47) * mm});
            skLineSegment(sketch, "E27.0.4.3", {"start": v(-109.95, 80.55) * mm, "end": v(-111.03, 80.55) * mm});
            skPoint(sketch, "E27.0.4.4", {"position": v(-110.49, 80) * mm});
            skPoint(sketch, "E27.0.4.5", {"position": v(-110.49, 80) * mm});
            skLineSegment(sketch, "E27.1.0.0", {"start": v(-102.33, 109.95) * mm, "end": v(-103.41, 109.95) * mm});
            skLineSegment(sketch, "E27.1.0.1", {"start": v(-102.33, 111.03) * mm, "end": v(-102.33, 109.95) * mm});
            skLineSegment(sketch, "E27.1.0.2", {"start": v(-103.41, 111.03) * mm, "end": v(-103.41, 109.95) * mm});
            skLineSegment(sketch, "E27.1.0.3", {"start": v(-102.33, 111.03) * mm, "end": v(-103.41, 111.03) * mm});
            skPoint(sketch, "E27.1.0.4", {"position": v(-102.87, 110.5) * mm});
            skPoint(sketch, "E27.1.0.5", {"position": v(-102.87, 110.5) * mm});
            skLineSegment(sketch, "E27.1.1.0", {"start": v(-102.33, 102.33) * mm, "end": v(-103.41, 102.33) * mm});
            skLineSegment(sketch, "E27.1.1.1", {"start": v(-102.33, 103.41) * mm, "end": v(-102.33, 102.33) * mm});
            skLineSegment(sketch, "E27.1.1.2", {"start": v(-103.41, 103.41) * mm, "end": v(-103.41, 102.33) * mm});
            skLineSegment(sketch, "E27.1.1.3", {"start": v(-102.33, 103.41) * mm, "end": v(-103.41, 103.41) * mm});
            skPoint(sketch, "E27.1.1.4", {"position": v(-102.87, 102.87) * mm});
            skPoint(sketch, "E27.1.1.5", {"position": v(-102.87, 102.87) * mm});
            skLineSegment(sketch, "E27.1.2.0", {"start": v(-102.33, 94.7) * mm, "end": v(-103.41, 94.7) * mm});
            skLineSegment(sketch, "E27.1.2.1", {"start": v(-102.33, 95.8) * mm, "end": v(-102.33, 94.7) * mm});
            skLineSegment(sketch, "E27.1.2.2", {"start": v(-103.41, 95.8) * mm, "end": v(-103.41, 94.7) * mm});
            skLineSegment(sketch, "E27.1.2.3", {"start": v(-102.33, 95.8) * mm, "end": v(-103.41, 95.8) * mm});
            skPoint(sketch, "E27.1.2.4", {"position": v(-102.87, 95.25) * mm});
            skPoint(sketch, "E27.1.2.5", {"position": v(-102.87, 95.25) * mm});
            skLineSegment(sketch, "E27.1.3.0", {"start": v(-102.33, 87.09) * mm, "end": v(-103.41, 87.09) * mm});
            skLineSegment(sketch, "E27.1.3.1", {"start": v(-102.33, 88.17) * mm, "end": v(-102.33, 87.09) * mm});
            skLineSegment(sketch, "E27.1.3.2", {"start": v(-103.41, 88.17) * mm, "end": v(-103.41, 87.09) * mm});
            skLineSegment(sketch, "E27.1.3.3", {"start": v(-102.33, 88.17) * mm, "end": v(-103.41, 88.17) * mm});
            skPoint(sketch, "E27.1.3.4", {"position": v(-102.87, 87.63) * mm});
            skPoint(sketch, "E27.1.3.5", {"position": v(-102.87, 87.63) * mm});
            skLineSegment(sketch, "E27.1.4.0", {"start": v(-102.33, 79.47) * mm, "end": v(-103.41, 79.47) * mm});
            skLineSegment(sketch, "E27.1.4.1", {"start": v(-102.33, 80.55) * mm, "end": v(-102.33, 79.47) * mm});
            skLineSegment(sketch, "E27.1.4.2", {"start": v(-103.41, 80.55) * mm, "end": v(-103.41, 79.47) * mm});
            skLineSegment(sketch, "E27.1.4.3", {"start": v(-102.33, 80.55) * mm, "end": v(-103.41, 80.55) * mm});
            skPoint(sketch, "E27.1.4.4", {"position": v(-102.87, 80) * mm});
            skPoint(sketch, "E27.1.4.5", {"position": v(-102.87, 80) * mm});
            skLineSegment(sketch, "E27.2.0.0", {"start": v(-94.7, 109.95) * mm, "end": v(-95.8, 109.95) * mm});
            skLineSegment(sketch, "E27.2.0.1", {"start": v(-94.7, 111.03) * mm, "end": v(-94.7, 109.95) * mm});
            skLineSegment(sketch, "E27.2.0.2", {"start": v(-95.8, 111.03) * mm, "end": v(-95.8, 109.95) * mm});
            skLineSegment(sketch, "E27.2.0.3", {"start": v(-94.7, 111.03) * mm, "end": v(-95.8, 111.03) * mm});
            skPoint(sketch, "E27.2.0.4", {"position": v(-95.25, 110.5) * mm});
            skPoint(sketch, "E27.2.0.5", {"position": v(-95.25, 110.5) * mm});
            skLineSegment(sketch, "E27.2.1.0", {"start": v(-94.7, 102.33) * mm, "end": v(-95.8, 102.33) * mm});
            skLineSegment(sketch, "E27.2.1.1", {"start": v(-94.7, 103.41) * mm, "end": v(-94.7, 102.33) * mm});
            skLineSegment(sketch, "E27.2.1.2", {"start": v(-95.8, 103.41) * mm, "end": v(-95.8, 102.33) * mm});
            skLineSegment(sketch, "E27.2.1.3", {"start": v(-94.7, 103.41) * mm, "end": v(-95.8, 103.41) * mm});
            skPoint(sketch, "E27.2.1.4", {"position": v(-95.25, 102.87) * mm});
            skPoint(sketch, "E27.2.1.5", {"position": v(-95.25, 102.87) * mm});
            skLineSegment(sketch, "E27.2.3.0", {"start": v(-94.7, 87.09) * mm, "end": v(-95.8, 87.09) * mm});
            skLineSegment(sketch, "E27.2.3.1", {"start": v(-94.7, 88.17) * mm, "end": v(-94.7, 87.09) * mm});
            skLineSegment(sketch, "E27.2.3.2", {"start": v(-95.8, 88.17) * mm, "end": v(-95.8, 87.09) * mm});
            skLineSegment(sketch, "E27.2.3.3", {"start": v(-94.7, 88.17) * mm, "end": v(-95.8, 88.17) * mm});
            skPoint(sketch, "E27.2.3.4", {"position": v(-95.25, 87.63) * mm});
            skPoint(sketch, "E27.2.3.5", {"position": v(-95.25, 87.63) * mm});
            skLineSegment(sketch, "E27.2.4.0", {"start": v(-94.7, 79.47) * mm, "end": v(-95.8, 79.47) * mm});
            skLineSegment(sketch, "E27.2.4.1", {"start": v(-94.7, 80.55) * mm, "end": v(-94.7, 79.47) * mm});
            skLineSegment(sketch, "E27.2.4.2", {"start": v(-95.8, 80.55) * mm, "end": v(-95.8, 79.47) * mm});
            skLineSegment(sketch, "E27.2.4.3", {"start": v(-94.7, 80.55) * mm, "end": v(-95.8, 80.55) * mm});
            skPoint(sketch, "E27.2.4.4", {"position": v(-95.25, 80) * mm});
            skPoint(sketch, "E27.2.4.5", {"position": v(-95.25, 80) * mm});
            skLineSegment(sketch, "E27.3.0.0", {"start": v(-87.09, 109.95) * mm, "end": v(-88.17, 109.95) * mm});
            skLineSegment(sketch, "E27.3.0.1", {"start": v(-87.09, 111.03) * mm, "end": v(-87.09, 109.95) * mm});
            skLineSegment(sketch, "E27.3.0.2", {"start": v(-88.17, 111.03) * mm, "end": v(-88.17, 109.95) * mm});
            skLineSegment(sketch, "E27.3.0.3", {"start": v(-87.09, 111.03) * mm, "end": v(-88.17, 111.03) * mm});
            skPoint(sketch, "E27.3.0.4", {"position": v(-87.63, 110.5) * mm});
            skPoint(sketch, "E27.3.0.5", {"position": v(-87.63, 110.5) * mm});
            skLineSegment(sketch, "E27.3.1.0", {"start": v(-87.09, 102.33) * mm, "end": v(-88.17, 102.33) * mm});
            skLineSegment(sketch, "E27.3.1.1", {"start": v(-87.09, 103.41) * mm, "end": v(-87.09, 102.33) * mm});
            skLineSegment(sketch, "E27.3.1.2", {"start": v(-88.17, 103.41) * mm, "end": v(-88.17, 102.33) * mm});
            skLineSegment(sketch, "E27.3.1.3", {"start": v(-87.09, 103.41) * mm, "end": v(-88.17, 103.41) * mm});
            skPoint(sketch, "E27.3.1.4", {"position": v(-87.63, 102.87) * mm});
            skPoint(sketch, "E27.3.1.5", {"position": v(-87.63, 102.87) * mm});
            skLineSegment(sketch, "E27.3.2.0", {"start": v(-87.09, 94.7) * mm, "end": v(-88.17, 94.7) * mm});
            skLineSegment(sketch, "E27.3.2.1", {"start": v(-87.09, 95.8) * mm, "end": v(-87.09, 94.7) * mm});
            skLineSegment(sketch, "E27.3.2.2", {"start": v(-88.17, 95.8) * mm, "end": v(-88.17, 94.7) * mm});
            skLineSegment(sketch, "E27.3.2.3", {"start": v(-87.09, 95.8) * mm, "end": v(-88.17, 95.8) * mm});
            skPoint(sketch, "E27.3.2.4", {"position": v(-87.63, 95.25) * mm});
            skPoint(sketch, "E27.3.2.5", {"position": v(-87.63, 95.25) * mm});
            skLineSegment(sketch, "E27.3.3.0", {"start": v(-87.09, 87.09) * mm, "end": v(-88.17, 87.09) * mm});
            skLineSegment(sketch, "E27.3.3.1", {"start": v(-87.09, 88.17) * mm, "end": v(-87.09, 87.09) * mm});
            skLineSegment(sketch, "E27.3.3.2", {"start": v(-88.17, 88.17) * mm, "end": v(-88.17, 87.09) * mm});
            skLineSegment(sketch, "E27.3.3.3", {"start": v(-87.09, 88.17) * mm, "end": v(-88.17, 88.17) * mm});
            skPoint(sketch, "E27.3.3.4", {"position": v(-87.63, 87.63) * mm});
            skPoint(sketch, "E27.3.3.5", {"position": v(-87.63, 87.63) * mm});
            skLineSegment(sketch, "E27.3.4.0", {"start": v(-87.09, 79.47) * mm, "end": v(-88.17, 79.47) * mm});
            skLineSegment(sketch, "E27.3.4.1", {"start": v(-87.09, 80.55) * mm, "end": v(-87.09, 79.47) * mm});
            skLineSegment(sketch, "E27.3.4.2", {"start": v(-88.17, 80.55) * mm, "end": v(-88.17, 79.47) * mm});
            skLineSegment(sketch, "E27.3.4.3", {"start": v(-87.09, 80.55) * mm, "end": v(-88.17, 80.55) * mm});
            skPoint(sketch, "E27.3.4.4", {"position": v(-87.63, 80) * mm});
            skPoint(sketch, "E27.3.4.5", {"position": v(-87.63, 80) * mm});
            skLineSegment(sketch, "E27.4.0.0", {"start": v(-79.47, 109.95) * mm, "end": v(-80.55, 109.95) * mm});
            skLineSegment(sketch, "E27.4.0.1", {"start": v(-79.47, 111.03) * mm, "end": v(-79.47, 109.95) * mm});
            skLineSegment(sketch, "E27.4.0.2", {"start": v(-80.55, 111.03) * mm, "end": v(-80.55, 109.95) * mm});
            skLineSegment(sketch, "E27.4.0.3", {"start": v(-79.47, 111.03) * mm, "end": v(-80.55, 111.03) * mm});
            skPoint(sketch, "E27.4.0.4", {"position": v(-80, 110.5) * mm});
            skPoint(sketch, "E27.4.0.5", {"position": v(-80, 110.5) * mm});
            skLineSegment(sketch, "E27.4.1.0", {"start": v(-79.47, 102.33) * mm, "end": v(-80.55, 102.33) * mm});
            skLineSegment(sketch, "E27.4.1.1", {"start": v(-79.47, 103.41) * mm, "end": v(-79.47, 102.33) * mm});
            skLineSegment(sketch, "E27.4.1.2", {"start": v(-80.55, 103.41) * mm, "end": v(-80.55, 102.33) * mm});
            skLineSegment(sketch, "E27.4.1.3", {"start": v(-79.47, 103.41) * mm, "end": v(-80.55, 103.41) * mm});
            skPoint(sketch, "E27.4.1.4", {"position": v(-80, 102.87) * mm});
            skPoint(sketch, "E27.4.1.5", {"position": v(-80, 102.87) * mm});
            skLineSegment(sketch, "E27.4.2.0", {"start": v(-79.47, 94.7) * mm, "end": v(-80.55, 94.7) * mm});
            skLineSegment(sketch, "E27.4.2.1", {"start": v(-79.47, 95.8) * mm, "end": v(-79.47, 94.7) * mm});
            skLineSegment(sketch, "E27.4.2.2", {"start": v(-80.55, 95.8) * mm, "end": v(-80.55, 94.7) * mm});
            skLineSegment(sketch, "E27.4.2.3", {"start": v(-79.47, 95.8) * mm, "end": v(-80.55, 95.8) * mm});
            skPoint(sketch, "E27.4.2.4", {"position": v(-80, 95.25) * mm});
            skPoint(sketch, "E27.4.2.5", {"position": v(-80, 95.25) * mm});
            skLineSegment(sketch, "E27.4.3.0", {"start": v(-79.47, 87.09) * mm, "end": v(-80.55, 87.09) * mm});
            skLineSegment(sketch, "E27.4.3.1", {"start": v(-79.47, 88.17) * mm, "end": v(-79.47, 87.09) * mm});
            skLineSegment(sketch, "E27.4.3.2", {"start": v(-80.55, 88.17) * mm, "end": v(-80.55, 87.09) * mm});
            skLineSegment(sketch, "E27.4.3.3", {"start": v(-79.47, 88.17) * mm, "end": v(-80.55, 88.17) * mm});
            skPoint(sketch, "E27.4.3.4", {"position": v(-80, 87.63) * mm});
            skPoint(sketch, "E27.4.3.5", {"position": v(-80, 87.63) * mm});
            skLineSegment(sketch, "E27.4.4.0", {"start": v(-79.47, 79.47) * mm, "end": v(-80.55, 79.47) * mm});
            skLineSegment(sketch, "E27.4.4.1", {"start": v(-79.47, 80.55) * mm, "end": v(-79.47, 79.47) * mm});
            skLineSegment(sketch, "E27.4.4.2", {"start": v(-80.55, 80.55) * mm, "end": v(-80.55, 79.47) * mm});
            skLineSegment(sketch, "E27.4.4.3", {"start": v(-79.47, 80.55) * mm, "end": v(-80.55, 80.55) * mm});
            skPoint(sketch, "E27.4.4.4", {"position": v(-80, 80) * mm});
            skPoint(sketch, "E27.4.4.5", {"position": v(-80, 80) * mm});
            skPoint(sketch, "E28.0.1.1", {"position": v(-102.87, 41.9) * mm});
            skPoint(sketch, "E28.0.1.2", {"position": v(-87.63, 49.53) * mm});
            skPoint(sketch, "E28.0.1.3", {"position": v(-80, 64.77) * mm});
            skPoint(sketch, "E28.0.1.5", {"position": v(-110.49, 64.77) * mm});
            skPoint(sketch, "E28.0.1.6", {"position": v(-80, 49.53) * mm});
            skPoint(sketch, "E28.0.1.7", {"position": v(-80, 57.15) * mm});
            skPoint(sketch, "E28.0.1.8", {"position": v(-95.25, 64.77) * mm});
            skPoint(sketch, "E28.0.1.11", {"position": v(-106.68, 72.4) * mm});
            skPoint(sketch, "E28.0.1.13", {"position": v(-102.87, 49.53) * mm});
            skPoint(sketch, "E28.0.1.14", {"position": v(-95.25, 60.96) * mm});
            skPoint(sketch, "E28.0.1.16", {"position": v(-110.49, 41.9) * mm});
            skPoint(sketch, "E28.0.1.21", {"position": v(-102.87, 57.15) * mm});
            skPoint(sketch, "E28.0.1.22", {"position": v(-87.63, 57.15) * mm});
            skPoint(sketch, "E28.0.1.23", {"position": v(-80, 41.9) * mm});
            skPoint(sketch, "E28.0.1.24", {"position": v(-99.06, 45.72) * mm});
            skPoint(sketch, "E28.0.1.26", {"position": v(-95.25, 41.9) * mm});
            skPoint(sketch, "E28.0.1.27", {"position": v(-102.87, 64.77) * mm});
            skPoint(sketch, "E28.0.1.29", {"position": v(-87.63, 64.77) * mm});
            skPoint(sketch, "E28.0.1.30", {"position": v(-95.25, 72.4) * mm});
            skPoint(sketch, "E28.0.1.31", {"position": v(-87.63, 41.9) * mm});
            skPoint(sketch, "E28.0.1.32", {"position": v(-80, 72.4) * mm});
            skPoint(sketch, "E28.0.1.33", {"position": v(-95.25, 49.53) * mm});
            skPoint(sketch, "E28.0.1.34", {"position": v(-110.49, 49.53) * mm});
            skPoint(sketch, "E28.0.1.36", {"position": v(-102.87, 72.4) * mm});
            skPoint(sketch, "E28.0.1.39", {"position": v(-110.49, 57.15) * mm});
            skPoint(sketch, "E28.0.1.40", {"position": v(-91.44, 57.15) * mm});
            skPoint(sketch, "E28.0.1.42", {"position": v(-83.82, 68.58) * mm});
            skPoint(sketch, "E28.0.1.44", {"position": v(-87.63, 72.4) * mm});
            skPoint(sketch, "E28.0.1.45", {"position": v(-80, 72.4) * mm});
            skPoint(sketch, "E28.0.1.46", {"position": v(-110.49, 57.15) * mm});
            skPoint(sketch, "E28.0.1.47", {"position": v(-87.63, 41.9) * mm});
            skPoint(sketch, "E28.0.1.48", {"position": v(-87.63, 49.53) * mm});
            skPoint(sketch, "E28.0.1.49", {"position": v(-91.44, 57.15) * mm});
            skPoint(sketch, "E28.0.1.50", {"position": v(-110.49, 41.9) * mm});
            skPoint(sketch, "E28.0.1.51", {"position": v(-110.49, 49.53) * mm});
            skPoint(sketch, "E28.0.1.52", {"position": v(-95.25, 49.53) * mm});
            skPoint(sketch, "E28.0.1.53", {"position": v(-102.87, 64.77) * mm});
            skPoint(sketch, "E28.0.1.54", {"position": v(-95.25, 72.4) * mm});
            skPoint(sketch, "E28.0.1.55", {"position": v(-102.87, 57.15) * mm});
            skPoint(sketch, "E28.0.1.56", {"position": v(-110.49, 64.77) * mm});
            skPoint(sketch, "E28.0.1.57", {"position": v(-87.63, 57.15) * mm});
            skPoint(sketch, "E28.0.1.58", {"position": v(-87.63, 64.77) * mm});
            skPoint(sketch, "E28.0.1.59", {"position": v(-80, 41.9) * mm});
            skPoint(sketch, "E28.0.1.60", {"position": v(-102.87, 72.4) * mm});
            skPoint(sketch, "E28.0.1.61", {"position": v(-80, 57.15) * mm});
            skPoint(sketch, "E28.0.1.62", {"position": v(-87.63, 72.4) * mm});
            skPoint(sketch, "E28.0.1.63", {"position": v(-80, 49.53) * mm});
            skPoint(sketch, "E28.0.1.64", {"position": v(-102.87, 41.9) * mm});
            skPoint(sketch, "E28.0.1.65", {"position": v(-95.25, 60.96) * mm});
            skPoint(sketch, "E28.0.1.66", {"position": v(-102.87, 49.53) * mm});
            skPoint(sketch, "E28.0.1.67", {"position": v(-80, 64.77) * mm});
            skPoint(sketch, "E28.0.1.68", {"position": v(-110.49, 72.4) * mm});
            skPoint(sketch, "E28.0.1.69", {"position": v(-95.25, 64.77) * mm});
            skPoint(sketch, "E28.0.1.70", {"position": v(-95.25, 41.9) * mm});
            skLineSegment(sketch, "E28.0.1.71", {"start": v(-87.09, 57.7) * mm, "end": v(-87.09, 56.6) * mm});
            skPoint(sketch, "E28.0.1.72", {"position": v(-110.49, 72.4) * mm});
            skLineSegment(sketch, "E28.0.1.73", {"start": v(-87.09, 56.6) * mm, "end": v(-88.17, 56.6) * mm});
            skLineSegment(sketch, "E28.0.1.74", {"start": v(-79.47, 41.37) * mm, "end": v(-80.55, 41.37) * mm});
            skLineSegment(sketch, "E28.0.1.75", {"start": v(-95.8, 42.45) * mm, "end": v(-95.8, 41.37) * mm});
            skLineSegment(sketch, "E28.0.1.76", {"start": v(-94.7, 50.07) * mm, "end": v(-94.7, 48.99) * mm});
            skLineSegment(sketch, "E28.0.1.77", {"start": v(-102.33, 41.37) * mm, "end": v(-103.41, 41.37) * mm});
            skLineSegment(sketch, "E28.0.1.78", {"start": v(-103.41, 57.7) * mm, "end": v(-103.41, 56.6) * mm});
            skLineSegment(sketch, "E28.0.1.79", {"start": v(-103.41, 42.45) * mm, "end": v(-103.41, 41.37) * mm});
            skLineSegment(sketch, "E28.0.1.80", {"start": v(-102.33, 71.85) * mm, "end": v(-103.41, 71.85) * mm});
            skLineSegment(sketch, "E28.0.1.81", {"start": v(-102.33, 72.93) * mm, "end": v(-103.41, 72.93) * mm});
            skLineSegment(sketch, "E28.0.1.82", {"start": v(-111.03, 50.07) * mm, "end": v(-111.03, 48.99) * mm});
            skLineSegment(sketch, "E28.0.1.83", {"start": v(-79.47, 65.31) * mm, "end": v(-80.55, 65.31) * mm});
            skLineSegment(sketch, "E28.0.1.84", {"start": v(-102.33, 57.7) * mm, "end": v(-102.33, 56.6) * mm});
            skLineSegment(sketch, "E28.0.1.85", {"start": v(-87.09, 50.07) * mm, "end": v(-88.17, 50.07) * mm});
            skLineSegment(sketch, "E28.0.1.86", {"start": v(-94.7, 64.23) * mm, "end": v(-95.8, 64.23) * mm});
            skLineSegment(sketch, "E28.0.1.87", {"start": v(-87.09, 64.23) * mm, "end": v(-88.17, 64.23) * mm});
            skLineSegment(sketch, "E28.0.1.88", {"start": v(-109.95, 50.07) * mm, "end": v(-111.03, 50.07) * mm});
            skLineSegment(sketch, "E28.0.1.89", {"start": v(-102.33, 50.07) * mm, "end": v(-103.41, 50.07) * mm});
            skLineSegment(sketch, "E28.0.1.90", {"start": v(-109.95, 41.37) * mm, "end": v(-111.03, 41.37) * mm});
            skLineSegment(sketch, "E28.0.1.91", {"start": v(-109.95, 64.23) * mm, "end": v(-111.03, 64.23) * mm});
            skLineSegment(sketch, "E28.0.1.92", {"start": v(-103.41, 50.07) * mm, "end": v(-103.41, 48.99) * mm});
            skLineSegment(sketch, "E28.0.1.93", {"start": v(-94.7, 41.37) * mm, "end": v(-95.8, 41.37) * mm});
            skLineSegment(sketch, "E28.0.1.94", {"start": v(-109.95, 56.6) * mm, "end": v(-111.03, 56.6) * mm});
            skLineSegment(sketch, "E28.0.1.95", {"start": v(-95.8, 65.31) * mm, "end": v(-95.8, 64.23) * mm});
            skLineSegment(sketch, "E28.0.1.96", {"start": v(-87.09, 57.7) * mm, "end": v(-88.17, 57.7) * mm});
            skLineSegment(sketch, "E28.0.1.97", {"start": v(-88.17, 42.45) * mm, "end": v(-88.17, 41.37) * mm});
            skLineSegment(sketch, "E28.0.1.98", {"start": v(-79.47, 65.31) * mm, "end": v(-79.47, 64.23) * mm});
            skLineSegment(sketch, "E28.0.1.99", {"start": v(-109.95, 42.45) * mm, "end": v(-109.95, 41.37) * mm});
            skLineSegment(sketch, "E28.0.1.100", {"start": v(-111.03, 57.7) * mm, "end": v(-111.03, 56.6) * mm});
            skLineSegment(sketch, "E28.0.1.101", {"start": v(-109.95, 65.31) * mm, "end": v(-111.03, 65.31) * mm});
            skLineSegment(sketch, "E28.0.1.102", {"start": v(-79.47, 50.07) * mm, "end": v(-79.47, 48.99) * mm});
            skLineSegment(sketch, "E28.0.1.103", {"start": v(-102.33, 42.45) * mm, "end": v(-103.41, 42.45) * mm});
            skLineSegment(sketch, "E28.0.1.104", {"start": v(-79.47, 56.6) * mm, "end": v(-80.55, 56.6) * mm});
            skLineSegment(sketch, "E28.0.1.105", {"start": v(-87.09, 72.93) * mm, "end": v(-87.09, 71.85) * mm});
            skLineSegment(sketch, "E28.0.1.106", {"start": v(-87.09, 42.45) * mm, "end": v(-87.09, 41.37) * mm});
            skLineSegment(sketch, "E28.0.1.107", {"start": v(-103.41, 65.31) * mm, "end": v(-103.41, 64.23) * mm});
            skLineSegment(sketch, "E28.0.1.108", {"start": v(-94.7, 48.99) * mm, "end": v(-95.8, 48.99) * mm});
            skLineSegment(sketch, "E28.0.1.109", {"start": v(-102.33, 65.31) * mm, "end": v(-102.33, 64.23) * mm});
            skLineSegment(sketch, "E28.0.1.110", {"start": v(-80.55, 57.7) * mm, "end": v(-80.55, 56.6) * mm});
            skLineSegment(sketch, "E28.0.1.111", {"start": v(-87.09, 41.37) * mm, "end": v(-88.17, 41.37) * mm});
            skLineSegment(sketch, "E28.0.1.112", {"start": v(-102.33, 72.93) * mm, "end": v(-102.33, 71.85) * mm});
            skLineSegment(sketch, "E28.0.1.113", {"start": v(-94.7, 42.45) * mm, "end": v(-94.7, 41.37) * mm});
            skLineSegment(sketch, "E28.0.1.114", {"start": v(-102.33, 57.7) * mm, "end": v(-103.41, 57.7) * mm});
            skLineSegment(sketch, "E28.0.1.115", {"start": v(-102.33, 56.6) * mm, "end": v(-103.41, 56.6) * mm});
            skLineSegment(sketch, "E28.0.1.116", {"start": v(-87.09, 42.45) * mm, "end": v(-88.17, 42.45) * mm});
            skLineSegment(sketch, "E28.0.1.117", {"start": v(-102.33, 42.45) * mm, "end": v(-102.33, 41.37) * mm});
            skLineSegment(sketch, "E28.0.1.118", {"start": v(-79.47, 57.7) * mm, "end": v(-80.55, 57.7) * mm});
            skLineSegment(sketch, "E28.0.1.119", {"start": v(-88.17, 65.31) * mm, "end": v(-88.17, 64.23) * mm});
            skLineSegment(sketch, "E28.0.1.120", {"start": v(-109.95, 48.99) * mm, "end": v(-111.03, 48.99) * mm});
            skLineSegment(sketch, "E28.0.1.121", {"start": v(-79.47, 50.07) * mm, "end": v(-80.55, 50.07) * mm});
            skLineSegment(sketch, "E28.0.1.122", {"start": v(-111.03, 42.45) * mm, "end": v(-111.03, 41.37) * mm});
            skLineSegment(sketch, "E28.0.1.123", {"start": v(-94.7, 72.93) * mm, "end": v(-94.7, 71.85) * mm});
            skLineSegment(sketch, "E28.0.1.124", {"start": v(-94.7, 65.31) * mm, "end": v(-94.7, 64.23) * mm});
            skLineSegment(sketch, "E28.0.1.125", {"start": v(-79.47, 71.85) * mm, "end": v(-80.55, 71.85) * mm});
            skLineSegment(sketch, "E28.0.1.126", {"start": v(-80.55, 65.31) * mm, "end": v(-80.55, 64.23) * mm});
            skLineSegment(sketch, "E28.0.1.127", {"start": v(-87.09, 72.93) * mm, "end": v(-88.17, 72.93) * mm});
            skLineSegment(sketch, "E28.0.1.128", {"start": v(-95.8, 50.07) * mm, "end": v(-95.8, 48.99) * mm});
            skLineSegment(sketch, "E28.0.1.129", {"start": v(-94.7, 71.85) * mm, "end": v(-95.8, 71.85) * mm});
            skLineSegment(sketch, "E28.0.1.130", {"start": v(-87.09, 71.85) * mm, "end": v(-88.17, 71.85) * mm});
            skLineSegment(sketch, "E28.0.1.131", {"start": v(-103.41, 72.93) * mm, "end": v(-103.41, 71.85) * mm});
            skLineSegment(sketch, "E28.0.1.132", {"start": v(-109.95, 65.31) * mm, "end": v(-109.95, 64.23) * mm});
            skLineSegment(sketch, "E28.0.1.133", {"start": v(-79.47, 72.93) * mm, "end": v(-80.55, 72.93) * mm});
            skLineSegment(sketch, "E28.0.1.134", {"start": v(-94.7, 42.45) * mm, "end": v(-95.8, 42.45) * mm});
            skLineSegment(sketch, "E28.0.1.135", {"start": v(-87.09, 65.31) * mm, "end": v(-88.17, 65.31) * mm});
            skLineSegment(sketch, "E28.0.1.136", {"start": v(-94.7, 72.93) * mm, "end": v(-95.8, 72.93) * mm});
            skLineSegment(sketch, "E28.0.1.137", {"start": v(-102.33, 50.07) * mm, "end": v(-102.33, 48.99) * mm});
            skLineSegment(sketch, "E28.0.1.138", {"start": v(-94.7, 65.31) * mm, "end": v(-95.8, 65.31) * mm});
            skLineSegment(sketch, "E28.0.1.139", {"start": v(-79.47, 42.45) * mm, "end": v(-80.55, 42.45) * mm});
            skLineSegment(sketch, "E28.0.1.140", {"start": v(-87.09, 65.31) * mm, "end": v(-87.09, 64.23) * mm});
            skLineSegment(sketch, "E28.0.1.141", {"start": v(-80.55, 72.93) * mm, "end": v(-80.55, 71.85) * mm});
            skLineSegment(sketch, "E28.0.1.142", {"start": v(-80.55, 50.07) * mm, "end": v(-80.55, 48.99) * mm});
            skLineSegment(sketch, "E28.0.1.143", {"start": v(-80.55, 42.45) * mm, "end": v(-80.55, 41.37) * mm});
            skLineSegment(sketch, "E28.0.1.144", {"start": v(-102.33, 64.23) * mm, "end": v(-103.41, 64.23) * mm});
            skLineSegment(sketch, "E28.0.1.145", {"start": v(-79.47, 72.93) * mm, "end": v(-79.47, 71.85) * mm});
            skLineSegment(sketch, "E28.0.1.146", {"start": v(-88.17, 72.93) * mm, "end": v(-88.17, 71.85) * mm});
            skLineSegment(sketch, "E28.0.1.147", {"start": v(-79.47, 42.45) * mm, "end": v(-79.47, 41.37) * mm});
            skLineSegment(sketch, "E28.0.1.148", {"start": v(-95.8, 72.93) * mm, "end": v(-95.8, 71.85) * mm});
            skLineSegment(sketch, "E28.0.1.149", {"start": v(-79.47, 48.99) * mm, "end": v(-80.55, 48.99) * mm});
            skLineSegment(sketch, "E28.0.1.150", {"start": v(-94.7, 50.07) * mm, "end": v(-95.8, 50.07) * mm});
            skLineSegment(sketch, "E28.0.1.151", {"start": v(-79.47, 57.7) * mm, "end": v(-79.47, 56.6) * mm});
            skLineSegment(sketch, "E28.0.1.152", {"start": v(-87.09, 48.99) * mm, "end": v(-88.17, 48.99) * mm});
            skLineSegment(sketch, "E28.0.1.153", {"start": v(-87.09, 50.07) * mm, "end": v(-87.09, 48.99) * mm});
            skLineSegment(sketch, "E28.0.1.154", {"start": v(-79.47, 64.23) * mm, "end": v(-80.55, 64.23) * mm});
            skLineSegment(sketch, "E28.0.1.155", {"start": v(-102.33, 65.31) * mm, "end": v(-103.41, 65.31) * mm});
            skLineSegment(sketch, "E28.0.1.156", {"start": v(-109.95, 42.45) * mm, "end": v(-111.03, 42.45) * mm});
            skLineSegment(sketch, "E28.0.1.157", {"start": v(-109.95, 57.7) * mm, "end": v(-111.03, 57.7) * mm});
            skLineSegment(sketch, "E28.0.1.158", {"start": v(-102.33, 48.99) * mm, "end": v(-103.41, 48.99) * mm});
            skLineSegment(sketch, "E28.0.1.159", {"start": v(-109.95, 72.93) * mm, "end": v(-111.03, 72.93) * mm});
            skLineSegment(sketch, "E28.0.1.160", {"start": v(-88.17, 50.07) * mm, "end": v(-88.17, 48.99) * mm});
            skLineSegment(sketch, "E28.0.1.161", {"start": v(-109.95, 71.85) * mm, "end": v(-111.03, 71.85) * mm});
            skLineSegment(sketch, "E28.0.1.162", {"start": v(-109.95, 72.93) * mm, "end": v(-109.95, 71.85) * mm});
            skLineSegment(sketch, "E28.0.1.163", {"start": v(-111.03, 65.31) * mm, "end": v(-111.03, 64.23) * mm});
            skLineSegment(sketch, "E28.0.1.164", {"start": v(-88.17, 57.7) * mm, "end": v(-88.17, 56.6) * mm});
            skLineSegment(sketch, "E28.0.1.165", {"start": v(-109.95, 57.7) * mm, "end": v(-109.95, 56.6) * mm});
            skLineSegment(sketch, "E28.0.1.166", {"start": v(-109.95, 50.07) * mm, "end": v(-109.95, 48.99) * mm});
            skLineSegment(sketch, "E28.0.1.167", {"start": v(-111.03, 72.93) * mm, "end": v(-111.03, 71.85) * mm});
            skPoint(sketch, "E28.0.2.1", {"position": v(-102.87, 3.8) * mm});
            skPoint(sketch, "E28.0.2.2", {"position": v(-87.63, 11.43) * mm});
            skPoint(sketch, "E28.0.2.3", {"position": v(-80, 26.67) * mm});
            skPoint(sketch, "E28.0.2.5", {"position": v(-110.49, 26.67) * mm});
            skPoint(sketch, "E28.0.2.6", {"position": v(-80, 11.43) * mm});
            skPoint(sketch, "E28.0.2.7", {"position": v(-80, 19.05) * mm});
            skPoint(sketch, "E28.0.2.8", {"position": v(-95.25, 26.67) * mm});
            skPoint(sketch, "E28.0.2.11", {"position": v(-106.68, 34.3) * mm});
            skPoint(sketch, "E28.0.2.13", {"position": v(-102.87, 11.43) * mm});
            skPoint(sketch, "E28.0.2.14", {"position": v(-95.25, 22.86) * mm});
            skPoint(sketch, "E28.0.2.16", {"position": v(-110.49, 3.8) * mm});
            skPoint(sketch, "E28.0.2.21", {"position": v(-102.87, 19.05) * mm});
            skPoint(sketch, "E28.0.2.22", {"position": v(-87.63, 19.05) * mm});
            skPoint(sketch, "E28.0.2.23", {"position": v(-80, 3.8) * mm});
            skPoint(sketch, "E28.0.2.24", {"position": v(-99.06, 7.62) * mm});
            skPoint(sketch, "E28.0.2.26", {"position": v(-95.25, 3.8) * mm});
            skPoint(sketch, "E28.0.2.27", {"position": v(-102.87, 26.67) * mm});
            skPoint(sketch, "E28.0.2.29", {"position": v(-87.63, 26.67) * mm});
            skPoint(sketch, "E28.0.2.30", {"position": v(-95.25, 34.3) * mm});
            skPoint(sketch, "E28.0.2.31", {"position": v(-87.63, 3.8) * mm});
            skPoint(sketch, "E28.0.2.32", {"position": v(-80, 34.3) * mm});
            skPoint(sketch, "E28.0.2.33", {"position": v(-95.25, 11.43) * mm});
            skPoint(sketch, "E28.0.2.34", {"position": v(-110.49, 11.43) * mm});
            skPoint(sketch, "E28.0.2.36", {"position": v(-102.87, 34.3) * mm});
            skPoint(sketch, "E28.0.2.39", {"position": v(-110.49, 19.05) * mm});
            skPoint(sketch, "E28.0.2.40", {"position": v(-91.44, 19.05) * mm});
            skPoint(sketch, "E28.0.2.42", {"position": v(-83.82, 30.48) * mm});
            skPoint(sketch, "E28.0.2.44", {"position": v(-87.63, 34.3) * mm});
            skPoint(sketch, "E28.0.2.45", {"position": v(-80, 34.3) * mm});
            skPoint(sketch, "E28.0.2.46", {"position": v(-110.49, 19.05) * mm});
            skPoint(sketch, "E28.0.2.47", {"position": v(-87.63, 3.8) * mm});
            skPoint(sketch, "E28.0.2.48", {"position": v(-87.63, 11.43) * mm});
            skPoint(sketch, "E28.0.2.49", {"position": v(-91.44, 19.05) * mm});
            skPoint(sketch, "E28.0.2.50", {"position": v(-110.49, 3.8) * mm});
            skPoint(sketch, "E28.0.2.51", {"position": v(-110.49, 11.43) * mm});
            skPoint(sketch, "E28.0.2.52", {"position": v(-95.25, 11.43) * mm});
            skPoint(sketch, "E28.0.2.53", {"position": v(-102.87, 26.67) * mm});
            skPoint(sketch, "E28.0.2.54", {"position": v(-95.25, 34.3) * mm});
            skPoint(sketch, "E28.0.2.55", {"position": v(-102.87, 19.05) * mm});
            skPoint(sketch, "E28.0.2.56", {"position": v(-110.49, 26.67) * mm});
            skPoint(sketch, "E28.0.2.57", {"position": v(-87.63, 19.05) * mm});
            skPoint(sketch, "E28.0.2.58", {"position": v(-87.63, 26.67) * mm});
            skPoint(sketch, "E28.0.2.59", {"position": v(-80, 3.8) * mm});
            skPoint(sketch, "E28.0.2.60", {"position": v(-102.87, 34.3) * mm});
            skPoint(sketch, "E28.0.2.61", {"position": v(-80, 19.05) * mm});
            skPoint(sketch, "E28.0.2.62", {"position": v(-87.63, 34.3) * mm});
            skPoint(sketch, "E28.0.2.63", {"position": v(-80, 11.43) * mm});
            skPoint(sketch, "E28.0.2.64", {"position": v(-102.87, 3.8) * mm});
            skPoint(sketch, "E28.0.2.65", {"position": v(-95.25, 22.86) * mm});
            skPoint(sketch, "E28.0.2.66", {"position": v(-102.87, 11.43) * mm});
            skPoint(sketch, "E28.0.2.67", {"position": v(-80, 26.67) * mm});
            skPoint(sketch, "E28.0.2.68", {"position": v(-110.49, 34.3) * mm});
            skPoint(sketch, "E28.0.2.69", {"position": v(-95.25, 26.67) * mm});
            skPoint(sketch, "E28.0.2.70", {"position": v(-95.25, 3.8) * mm});
            skLineSegment(sketch, "E28.0.2.71", {"start": v(-87.09, 19.6) * mm, "end": v(-87.09, 18.5) * mm});
            skPoint(sketch, "E28.0.2.72", {"position": v(-110.49, 34.3) * mm});
            skLineSegment(sketch, "E28.0.2.73", {"start": v(-87.09, 18.5) * mm, "end": v(-88.17, 18.5) * mm});
            skLineSegment(sketch, "E28.0.2.74", {"start": v(-79.47, 3.27) * mm, "end": v(-80.55, 3.27) * mm});
            skLineSegment(sketch, "E28.0.2.75", {"start": v(-95.8, 4.35) * mm, "end": v(-95.8, 3.27) * mm});
            skLineSegment(sketch, "E28.0.2.76", {"start": v(-94.7, 11.97) * mm, "end": v(-94.7, 10.89) * mm});
            skLineSegment(sketch, "E28.0.2.77", {"start": v(-102.33, 3.27) * mm, "end": v(-103.41, 3.27) * mm});
            skLineSegment(sketch, "E28.0.2.78", {"start": v(-103.41, 19.6) * mm, "end": v(-103.41, 18.5) * mm});
            skLineSegment(sketch, "E28.0.2.79", {"start": v(-103.41, 4.35) * mm, "end": v(-103.41, 3.27) * mm});
            skLineSegment(sketch, "E28.0.2.80", {"start": v(-102.33, 33.75) * mm, "end": v(-103.41, 33.75) * mm});
            skLineSegment(sketch, "E28.0.2.81", {"start": v(-102.33, 34.83) * mm, "end": v(-103.41, 34.83) * mm});
            skLineSegment(sketch, "E28.0.2.82", {"start": v(-111.03, 11.97) * mm, "end": v(-111.03, 10.89) * mm});
            skLineSegment(sketch, "E28.0.2.83", {"start": v(-79.47, 27.21) * mm, "end": v(-80.55, 27.21) * mm});
            skLineSegment(sketch, "E28.0.2.84", {"start": v(-102.33, 19.6) * mm, "end": v(-102.33, 18.5) * mm});
            skLineSegment(sketch, "E28.0.2.85", {"start": v(-87.09, 11.97) * mm, "end": v(-88.17, 11.97) * mm});
            skLineSegment(sketch, "E28.0.2.86", {"start": v(-94.7, 26.13) * mm, "end": v(-95.8, 26.13) * mm});
            skLineSegment(sketch, "E28.0.2.87", {"start": v(-87.09, 26.13) * mm, "end": v(-88.17, 26.13) * mm});
            skLineSegment(sketch, "E28.0.2.88", {"start": v(-109.95, 11.97) * mm, "end": v(-111.03, 11.97) * mm});
            skLineSegment(sketch, "E28.0.2.89", {"start": v(-102.33, 11.97) * mm, "end": v(-103.41, 11.97) * mm});
            skLineSegment(sketch, "E28.0.2.90", {"start": v(-109.95, 3.27) * mm, "end": v(-111.03, 3.27) * mm});
            skLineSegment(sketch, "E28.0.2.91", {"start": v(-109.95, 26.13) * mm, "end": v(-111.03, 26.13) * mm});
            skLineSegment(sketch, "E28.0.2.92", {"start": v(-103.41, 11.97) * mm, "end": v(-103.41, 10.89) * mm});
            skLineSegment(sketch, "E28.0.2.93", {"start": v(-94.7, 3.27) * mm, "end": v(-95.8, 3.27) * mm});
            skLineSegment(sketch, "E28.0.2.94", {"start": v(-109.95, 18.5) * mm, "end": v(-111.03, 18.5) * mm});
            skLineSegment(sketch, "E28.0.2.95", {"start": v(-95.8, 27.21) * mm, "end": v(-95.8, 26.13) * mm});
            skLineSegment(sketch, "E28.0.2.96", {"start": v(-87.09, 19.6) * mm, "end": v(-88.17, 19.6) * mm});
            skLineSegment(sketch, "E28.0.2.97", {"start": v(-88.17, 4.35) * mm, "end": v(-88.17, 3.27) * mm});
            skLineSegment(sketch, "E28.0.2.98", {"start": v(-79.47, 27.21) * mm, "end": v(-79.47, 26.13) * mm});
            skLineSegment(sketch, "E28.0.2.99", {"start": v(-109.95, 4.35) * mm, "end": v(-109.95, 3.27) * mm});
            skLineSegment(sketch, "E28.0.2.100", {"start": v(-111.03, 19.6) * mm, "end": v(-111.03, 18.5) * mm});
            skLineSegment(sketch, "E28.0.2.101", {"start": v(-109.95, 27.21) * mm, "end": v(-111.03, 27.21) * mm});
            skLineSegment(sketch, "E28.0.2.102", {"start": v(-79.47, 11.97) * mm, "end": v(-79.47, 10.89) * mm});
            skLineSegment(sketch, "E28.0.2.103", {"start": v(-102.33, 4.35) * mm, "end": v(-103.41, 4.35) * mm});
            skLineSegment(sketch, "E28.0.2.104", {"start": v(-79.47, 18.5) * mm, "end": v(-80.55, 18.5) * mm});
            skLineSegment(sketch, "E28.0.2.105", {"start": v(-87.09, 34.83) * mm, "end": v(-87.09, 33.75) * mm});
            skLineSegment(sketch, "E28.0.2.106", {"start": v(-87.09, 4.35) * mm, "end": v(-87.09, 3.27) * mm});
            skLineSegment(sketch, "E28.0.2.107", {"start": v(-103.41, 27.21) * mm, "end": v(-103.41, 26.13) * mm});
            skLineSegment(sketch, "E28.0.2.108", {"start": v(-94.7, 10.89) * mm, "end": v(-95.8, 10.89) * mm});
            skLineSegment(sketch, "E28.0.2.109", {"start": v(-102.33, 27.21) * mm, "end": v(-102.33, 26.13) * mm});
            skLineSegment(sketch, "E28.0.2.110", {"start": v(-80.55, 19.6) * mm, "end": v(-80.55, 18.5) * mm});
            skLineSegment(sketch, "E28.0.2.111", {"start": v(-87.09, 3.27) * mm, "end": v(-88.17, 3.27) * mm});
            skLineSegment(sketch, "E28.0.2.112", {"start": v(-102.33, 34.83) * mm, "end": v(-102.33, 33.75) * mm});
            skLineSegment(sketch, "E28.0.2.113", {"start": v(-94.7, 4.35) * mm, "end": v(-94.7, 3.27) * mm});
            skLineSegment(sketch, "E28.0.2.114", {"start": v(-102.33, 19.6) * mm, "end": v(-103.41, 19.6) * mm});
            skLineSegment(sketch, "E28.0.2.115", {"start": v(-102.33, 18.5) * mm, "end": v(-103.41, 18.5) * mm});
            skLineSegment(sketch, "E28.0.2.116", {"start": v(-87.09, 4.35) * mm, "end": v(-88.17, 4.35) * mm});
            skLineSegment(sketch, "E28.0.2.117", {"start": v(-102.33, 4.35) * mm, "end": v(-102.33, 3.27) * mm});
            skLineSegment(sketch, "E28.0.2.118", {"start": v(-79.47, 19.6) * mm, "end": v(-80.55, 19.6) * mm});
            skLineSegment(sketch, "E28.0.2.119", {"start": v(-88.17, 27.21) * mm, "end": v(-88.17, 26.13) * mm});
            skLineSegment(sketch, "E28.0.2.120", {"start": v(-109.95, 10.89) * mm, "end": v(-111.03, 10.89) * mm});
            skLineSegment(sketch, "E28.0.2.121", {"start": v(-79.47, 11.97) * mm, "end": v(-80.55, 11.97) * mm});
            skLineSegment(sketch, "E28.0.2.122", {"start": v(-111.03, 4.35) * mm, "end": v(-111.03, 3.27) * mm});
            skLineSegment(sketch, "E28.0.2.123", {"start": v(-94.7, 34.83) * mm, "end": v(-94.7, 33.75) * mm});
            skLineSegment(sketch, "E28.0.2.124", {"start": v(-94.7, 27.21) * mm, "end": v(-94.7, 26.13) * mm});
            skLineSegment(sketch, "E28.0.2.125", {"start": v(-79.47, 33.75) * mm, "end": v(-80.55, 33.75) * mm});
            skLineSegment(sketch, "E28.0.2.126", {"start": v(-80.55, 27.21) * mm, "end": v(-80.55, 26.13) * mm});
            skLineSegment(sketch, "E28.0.2.127", {"start": v(-87.09, 34.83) * mm, "end": v(-88.17, 34.83) * mm});
            skLineSegment(sketch, "E28.0.2.128", {"start": v(-95.8, 11.97) * mm, "end": v(-95.8, 10.89) * mm});
            skLineSegment(sketch, "E28.0.2.129", {"start": v(-94.7, 33.75) * mm, "end": v(-95.8, 33.75) * mm});
            skLineSegment(sketch, "E28.0.2.130", {"start": v(-87.09, 33.75) * mm, "end": v(-88.17, 33.75) * mm});
            skLineSegment(sketch, "E28.0.2.131", {"start": v(-103.41, 34.83) * mm, "end": v(-103.41, 33.75) * mm});
            skLineSegment(sketch, "E28.0.2.132", {"start": v(-109.95, 27.21) * mm, "end": v(-109.95, 26.13) * mm});
            skLineSegment(sketch, "E28.0.2.133", {"start": v(-79.47, 34.83) * mm, "end": v(-80.55, 34.83) * mm});
            skLineSegment(sketch, "E28.0.2.134", {"start": v(-94.7, 4.35) * mm, "end": v(-95.8, 4.35) * mm});
            skLineSegment(sketch, "E28.0.2.135", {"start": v(-87.09, 27.21) * mm, "end": v(-88.17, 27.21) * mm});
            skLineSegment(sketch, "E28.0.2.136", {"start": v(-94.7, 34.83) * mm, "end": v(-95.8, 34.83) * mm});
            skLineSegment(sketch, "E28.0.2.137", {"start": v(-102.33, 11.97) * mm, "end": v(-102.33, 10.89) * mm});
            skLineSegment(sketch, "E28.0.2.138", {"start": v(-94.7, 27.21) * mm, "end": v(-95.8, 27.21) * mm});
            skLineSegment(sketch, "E28.0.2.139", {"start": v(-79.47, 4.35) * mm, "end": v(-80.55, 4.35) * mm});
            skLineSegment(sketch, "E28.0.2.140", {"start": v(-87.09, 27.21) * mm, "end": v(-87.09, 26.13) * mm});
            skLineSegment(sketch, "E28.0.2.141", {"start": v(-80.55, 34.83) * mm, "end": v(-80.55, 33.75) * mm});
            skLineSegment(sketch, "E28.0.2.142", {"start": v(-80.55, 11.97) * mm, "end": v(-80.55, 10.89) * mm});
            skLineSegment(sketch, "E28.0.2.143", {"start": v(-80.55, 4.35) * mm, "end": v(-80.55, 3.27) * mm});
            skLineSegment(sketch, "E28.0.2.144", {"start": v(-102.33, 26.13) * mm, "end": v(-103.41, 26.13) * mm});
            skLineSegment(sketch, "E28.0.2.145", {"start": v(-79.47, 34.83) * mm, "end": v(-79.47, 33.75) * mm});
            skLineSegment(sketch, "E28.0.2.146", {"start": v(-88.17, 34.83) * mm, "end": v(-88.17, 33.75) * mm});
            skLineSegment(sketch, "E28.0.2.147", {"start": v(-79.47, 4.35) * mm, "end": v(-79.47, 3.27) * mm});
            skLineSegment(sketch, "E28.0.2.148", {"start": v(-95.8, 34.83) * mm, "end": v(-95.8, 33.75) * mm});
            skLineSegment(sketch, "E28.0.2.149", {"start": v(-79.47, 10.89) * mm, "end": v(-80.55, 10.89) * mm});
            skLineSegment(sketch, "E28.0.2.150", {"start": v(-94.7, 11.97) * mm, "end": v(-95.8, 11.97) * mm});
            skLineSegment(sketch, "E28.0.2.151", {"start": v(-79.47, 19.6) * mm, "end": v(-79.47, 18.5) * mm});
            skLineSegment(sketch, "E28.0.2.152", {"start": v(-87.09, 10.89) * mm, "end": v(-88.17, 10.89) * mm});
            skLineSegment(sketch, "E28.0.2.153", {"start": v(-87.09, 11.97) * mm, "end": v(-87.09, 10.89) * mm});
            skLineSegment(sketch, "E28.0.2.154", {"start": v(-79.47, 26.13) * mm, "end": v(-80.55, 26.13) * mm});
            skLineSegment(sketch, "E28.0.2.155", {"start": v(-102.33, 27.21) * mm, "end": v(-103.41, 27.21) * mm});
            skLineSegment(sketch, "E28.0.2.156", {"start": v(-109.95, 4.35) * mm, "end": v(-111.03, 4.35) * mm});
            skLineSegment(sketch, "E28.0.2.157", {"start": v(-109.95, 19.6) * mm, "end": v(-111.03, 19.6) * mm});
            skLineSegment(sketch, "E28.0.2.158", {"start": v(-102.33, 10.89) * mm, "end": v(-103.41, 10.89) * mm});
            skLineSegment(sketch, "E28.0.2.159", {"start": v(-109.95, 34.83) * mm, "end": v(-111.03, 34.83) * mm});
            skLineSegment(sketch, "E28.0.2.160", {"start": v(-88.17, 11.97) * mm, "end": v(-88.17, 10.89) * mm});
            skLineSegment(sketch, "E28.0.2.161", {"start": v(-109.95, 33.75) * mm, "end": v(-111.03, 33.75) * mm});
            skLineSegment(sketch, "E28.0.2.162", {"start": v(-109.95, 34.83) * mm, "end": v(-109.95, 33.75) * mm});
            skLineSegment(sketch, "E28.0.2.163", {"start": v(-111.03, 27.21) * mm, "end": v(-111.03, 26.13) * mm});
            skLineSegment(sketch, "E28.0.2.164", {"start": v(-88.17, 19.6) * mm, "end": v(-88.17, 18.5) * mm});
            skLineSegment(sketch, "E28.0.2.165", {"start": v(-109.95, 19.6) * mm, "end": v(-109.95, 18.5) * mm});
            skLineSegment(sketch, "E28.0.2.166", {"start": v(-109.95, 11.97) * mm, "end": v(-109.95, 10.89) * mm});
            skLineSegment(sketch, "E28.0.2.167", {"start": v(-111.03, 34.83) * mm, "end": v(-111.03, 33.75) * mm});
            skPoint(sketch, "E28.1.0.1", {"position": v(-64.77, 80) * mm});
            skPoint(sketch, "E28.1.0.2", {"position": v(-49.53, 87.63) * mm});
            skPoint(sketch, "E28.1.0.3", {"position": v(-41.9, 102.87) * mm});
            skPoint(sketch, "E28.1.0.5", {"position": v(-72.39, 102.87) * mm});
            skPoint(sketch, "E28.1.0.6", {"position": v(-41.9, 87.63) * mm});
            skPoint(sketch, "E28.1.0.7", {"position": v(-41.9, 95.25) * mm});
            skPoint(sketch, "E28.1.0.8", {"position": v(-57.15, 102.87) * mm});
            skPoint(sketch, "E28.1.0.11", {"position": v(-68.58, 110.5) * mm});
            skPoint(sketch, "E28.1.0.13", {"position": v(-64.77, 87.63) * mm});
            skPoint(sketch, "E28.1.0.14", {"position": v(-57.15, 99.06) * mm});
            skPoint(sketch, "E28.1.0.16", {"position": v(-72.39, 80) * mm});
            skPoint(sketch, "E28.1.0.21", {"position": v(-64.77, 95.25) * mm});
            skPoint(sketch, "E28.1.0.22", {"position": v(-49.53, 95.25) * mm});
            skPoint(sketch, "E28.1.0.23", {"position": v(-41.9, 80) * mm});
            skPoint(sketch, "E28.1.0.24", {"position": v(-60.96, 83.82) * mm});
            skPoint(sketch, "E28.1.0.26", {"position": v(-57.15, 80) * mm});
            skPoint(sketch, "E28.1.0.27", {"position": v(-64.77, 102.87) * mm});
            skPoint(sketch, "E28.1.0.29", {"position": v(-49.53, 102.87) * mm});
            skPoint(sketch, "E28.1.0.30", {"position": v(-57.15, 110.5) * mm});
            skPoint(sketch, "E28.1.0.31", {"position": v(-49.53, 80) * mm});
            skPoint(sketch, "E28.1.0.32", {"position": v(-41.9, 110.5) * mm});
            skPoint(sketch, "E28.1.0.33", {"position": v(-57.15, 87.63) * mm});
            skPoint(sketch, "E28.1.0.34", {"position": v(-72.39, 87.63) * mm});
            skPoint(sketch, "E28.1.0.36", {"position": v(-64.77, 110.5) * mm});
            skPoint(sketch, "E28.1.0.39", {"position": v(-72.39, 95.25) * mm});
            skPoint(sketch, "E28.1.0.40", {"position": v(-53.34, 95.25) * mm});
            skPoint(sketch, "E28.1.0.42", {"position": v(-45.72, 106.68) * mm});
            skPoint(sketch, "E28.1.0.44", {"position": v(-49.53, 110.5) * mm});
            skPoint(sketch, "E28.1.0.45", {"position": v(-41.9, 110.5) * mm});
            skPoint(sketch, "E28.1.0.46", {"position": v(-72.39, 95.25) * mm});
            skPoint(sketch, "E28.1.0.47", {"position": v(-49.53, 80) * mm});
            skPoint(sketch, "E28.1.0.48", {"position": v(-49.53, 87.63) * mm});
            skPoint(sketch, "E28.1.0.49", {"position": v(-53.34, 95.25) * mm});
            skPoint(sketch, "E28.1.0.50", {"position": v(-72.39, 80) * mm});
            skPoint(sketch, "E28.1.0.51", {"position": v(-72.39, 87.63) * mm});
            skPoint(sketch, "E28.1.0.52", {"position": v(-57.15, 87.63) * mm});
            skPoint(sketch, "E28.1.0.53", {"position": v(-64.77, 102.87) * mm});
            skPoint(sketch, "E28.1.0.54", {"position": v(-57.15, 110.5) * mm});
            skPoint(sketch, "E28.1.0.55", {"position": v(-64.77, 95.25) * mm});
            skPoint(sketch, "E28.1.0.56", {"position": v(-72.39, 102.87) * mm});
            skPoint(sketch, "E28.1.0.57", {"position": v(-49.53, 95.25) * mm});
            skPoint(sketch, "E28.1.0.58", {"position": v(-49.53, 102.87) * mm});
            skPoint(sketch, "E28.1.0.59", {"position": v(-41.9, 80) * mm});
            skPoint(sketch, "E28.1.0.60", {"position": v(-64.77, 110.5) * mm});
            skPoint(sketch, "E28.1.0.61", {"position": v(-41.9, 95.25) * mm});
            skPoint(sketch, "E28.1.0.62", {"position": v(-49.53, 110.5) * mm});
            skPoint(sketch, "E28.1.0.63", {"position": v(-41.9, 87.63) * mm});
            skPoint(sketch, "E28.1.0.64", {"position": v(-64.77, 80) * mm});
            skPoint(sketch, "E28.1.0.65", {"position": v(-57.15, 99.06) * mm});
            skPoint(sketch, "E28.1.0.66", {"position": v(-64.77, 87.63) * mm});
            skPoint(sketch, "E28.1.0.67", {"position": v(-41.9, 102.87) * mm});
            skPoint(sketch, "E28.1.0.68", {"position": v(-72.39, 110.5) * mm});
            skPoint(sketch, "E28.1.0.69", {"position": v(-57.15, 102.87) * mm});
            skPoint(sketch, "E28.1.0.70", {"position": v(-57.15, 80) * mm});
            skLineSegment(sketch, "E28.1.0.71", {"start": v(-48.99, 95.8) * mm, "end": v(-48.99, 94.7) * mm});
            skPoint(sketch, "E28.1.0.72", {"position": v(-72.39, 110.5) * mm});
            skLineSegment(sketch, "E28.1.0.73", {"start": v(-48.99, 94.7) * mm, "end": v(-50.07, 94.7) * mm});
            skLineSegment(sketch, "E28.1.0.74", {"start": v(-41.37, 79.47) * mm, "end": v(-42.45, 79.47) * mm});
            skLineSegment(sketch, "E28.1.0.75", {"start": v(-57.7, 80.55) * mm, "end": v(-57.7, 79.47) * mm});
            skLineSegment(sketch, "E28.1.0.76", {"start": v(-56.6, 88.17) * mm, "end": v(-56.6, 87.09) * mm});
            skLineSegment(sketch, "E28.1.0.77", {"start": v(-64.23, 79.47) * mm, "end": v(-65.31, 79.47) * mm});
            skLineSegment(sketch, "E28.1.0.78", {"start": v(-65.31, 95.8) * mm, "end": v(-65.31, 94.7) * mm});
            skLineSegment(sketch, "E28.1.0.79", {"start": v(-65.31, 80.55) * mm, "end": v(-65.31, 79.47) * mm});
            skLineSegment(sketch, "E28.1.0.80", {"start": v(-64.23, 109.95) * mm, "end": v(-65.31, 109.95) * mm});
            skLineSegment(sketch, "E28.1.0.81", {"start": v(-64.23, 111.03) * mm, "end": v(-65.31, 111.03) * mm});
            skLineSegment(sketch, "E28.1.0.82", {"start": v(-72.93, 88.17) * mm, "end": v(-72.93, 87.09) * mm});
            skLineSegment(sketch, "E28.1.0.83", {"start": v(-41.37, 103.41) * mm, "end": v(-42.45, 103.41) * mm});
            skLineSegment(sketch, "E28.1.0.84", {"start": v(-64.23, 95.8) * mm, "end": v(-64.23, 94.7) * mm});
            skLineSegment(sketch, "E28.1.0.85", {"start": v(-48.99, 88.17) * mm, "end": v(-50.07, 88.17) * mm});
            skLineSegment(sketch, "E28.1.0.86", {"start": v(-56.6, 102.33) * mm, "end": v(-57.7, 102.33) * mm});
            skLineSegment(sketch, "E28.1.0.87", {"start": v(-48.99, 102.33) * mm, "end": v(-50.07, 102.33) * mm});
            skLineSegment(sketch, "E28.1.0.88", {"start": v(-71.85, 88.17) * mm, "end": v(-72.93, 88.17) * mm});
            skLineSegment(sketch, "E28.1.0.89", {"start": v(-64.23, 88.17) * mm, "end": v(-65.31, 88.17) * mm});
            skLineSegment(sketch, "E28.1.0.90", {"start": v(-71.85, 79.47) * mm, "end": v(-72.93, 79.47) * mm});
            skLineSegment(sketch, "E28.1.0.91", {"start": v(-71.85, 102.33) * mm, "end": v(-72.93, 102.33) * mm});
            skLineSegment(sketch, "E28.1.0.92", {"start": v(-65.31, 88.17) * mm, "end": v(-65.31, 87.09) * mm});
            skLineSegment(sketch, "E28.1.0.93", {"start": v(-56.6, 79.47) * mm, "end": v(-57.7, 79.47) * mm});
            skLineSegment(sketch, "E28.1.0.94", {"start": v(-71.85, 94.7) * mm, "end": v(-72.93, 94.7) * mm});
            skLineSegment(sketch, "E28.1.0.95", {"start": v(-57.7, 103.41) * mm, "end": v(-57.7, 102.33) * mm});
            skLineSegment(sketch, "E28.1.0.96", {"start": v(-48.99, 95.8) * mm, "end": v(-50.07, 95.8) * mm});
            skLineSegment(sketch, "E28.1.0.97", {"start": v(-50.07, 80.55) * mm, "end": v(-50.07, 79.47) * mm});
            skLineSegment(sketch, "E28.1.0.98", {"start": v(-41.37, 103.41) * mm, "end": v(-41.37, 102.33) * mm});
            skLineSegment(sketch, "E28.1.0.99", {"start": v(-71.85, 80.55) * mm, "end": v(-71.85, 79.47) * mm});
            skLineSegment(sketch, "E28.1.0.100", {"start": v(-72.93, 95.8) * mm, "end": v(-72.93, 94.7) * mm});
            skLineSegment(sketch, "E28.1.0.101", {"start": v(-71.85, 103.41) * mm, "end": v(-72.93, 103.41) * mm});
            skLineSegment(sketch, "E28.1.0.102", {"start": v(-41.37, 88.17) * mm, "end": v(-41.37, 87.09) * mm});
            skLineSegment(sketch, "E28.1.0.103", {"start": v(-64.23, 80.55) * mm, "end": v(-65.31, 80.55) * mm});
            skLineSegment(sketch, "E28.1.0.104", {"start": v(-41.37, 94.7) * mm, "end": v(-42.45, 94.7) * mm});
            skLineSegment(sketch, "E28.1.0.105", {"start": v(-48.99, 111.03) * mm, "end": v(-48.99, 109.95) * mm});
            skLineSegment(sketch, "E28.1.0.106", {"start": v(-48.99, 80.55) * mm, "end": v(-48.99, 79.47) * mm});
            skLineSegment(sketch, "E28.1.0.107", {"start": v(-65.31, 103.41) * mm, "end": v(-65.31, 102.33) * mm});
            skLineSegment(sketch, "E28.1.0.108", {"start": v(-56.6, 87.09) * mm, "end": v(-57.7, 87.09) * mm});
            skLineSegment(sketch, "E28.1.0.109", {"start": v(-64.23, 103.41) * mm, "end": v(-64.23, 102.33) * mm});
            skLineSegment(sketch, "E28.1.0.110", {"start": v(-42.45, 95.8) * mm, "end": v(-42.45, 94.7) * mm});
            skLineSegment(sketch, "E28.1.0.111", {"start": v(-48.99, 79.47) * mm, "end": v(-50.07, 79.47) * mm});
            skLineSegment(sketch, "E28.1.0.112", {"start": v(-64.23, 111.03) * mm, "end": v(-64.23, 109.95) * mm});
            skLineSegment(sketch, "E28.1.0.113", {"start": v(-56.6, 80.55) * mm, "end": v(-56.6, 79.47) * mm});
            skLineSegment(sketch, "E28.1.0.114", {"start": v(-64.23, 95.8) * mm, "end": v(-65.31, 95.8) * mm});
            skLineSegment(sketch, "E28.1.0.115", {"start": v(-64.23, 94.7) * mm, "end": v(-65.31, 94.7) * mm});
            skLineSegment(sketch, "E28.1.0.116", {"start": v(-48.99, 80.55) * mm, "end": v(-50.07, 80.55) * mm});
            skLineSegment(sketch, "E28.1.0.117", {"start": v(-64.23, 80.55) * mm, "end": v(-64.23, 79.47) * mm});
            skLineSegment(sketch, "E28.1.0.118", {"start": v(-41.37, 95.8) * mm, "end": v(-42.45, 95.8) * mm});
            skLineSegment(sketch, "E28.1.0.119", {"start": v(-50.07, 103.41) * mm, "end": v(-50.07, 102.33) * mm});
            skLineSegment(sketch, "E28.1.0.120", {"start": v(-71.85, 87.09) * mm, "end": v(-72.93, 87.09) * mm});
            skLineSegment(sketch, "E28.1.0.121", {"start": v(-41.37, 88.17) * mm, "end": v(-42.45, 88.17) * mm});
            skLineSegment(sketch, "E28.1.0.122", {"start": v(-72.93, 80.55) * mm, "end": v(-72.93, 79.47) * mm});
            skLineSegment(sketch, "E28.1.0.123", {"start": v(-56.6, 111.03) * mm, "end": v(-56.6, 109.95) * mm});
            skLineSegment(sketch, "E28.1.0.124", {"start": v(-56.6, 103.41) * mm, "end": v(-56.6, 102.33) * mm});
            skLineSegment(sketch, "E28.1.0.125", {"start": v(-41.37, 109.95) * mm, "end": v(-42.45, 109.95) * mm});
            skLineSegment(sketch, "E28.1.0.126", {"start": v(-42.45, 103.41) * mm, "end": v(-42.45, 102.33) * mm});
            skLineSegment(sketch, "E28.1.0.127", {"start": v(-48.99, 111.03) * mm, "end": v(-50.07, 111.03) * mm});
            skLineSegment(sketch, "E28.1.0.128", {"start": v(-57.7, 88.17) * mm, "end": v(-57.7, 87.09) * mm});
            skLineSegment(sketch, "E28.1.0.129", {"start": v(-56.6, 109.95) * mm, "end": v(-57.7, 109.95) * mm});
            skLineSegment(sketch, "E28.1.0.130", {"start": v(-48.99, 109.95) * mm, "end": v(-50.07, 109.95) * mm});
            skLineSegment(sketch, "E28.1.0.131", {"start": v(-65.31, 111.03) * mm, "end": v(-65.31, 109.95) * mm});
            skLineSegment(sketch, "E28.1.0.132", {"start": v(-71.85, 103.41) * mm, "end": v(-71.85, 102.33) * mm});
            skLineSegment(sketch, "E28.1.0.133", {"start": v(-41.37, 111.03) * mm, "end": v(-42.45, 111.03) * mm});
            skLineSegment(sketch, "E28.1.0.134", {"start": v(-56.6, 80.55) * mm, "end": v(-57.7, 80.55) * mm});
            skLineSegment(sketch, "E28.1.0.135", {"start": v(-48.99, 103.41) * mm, "end": v(-50.07, 103.41) * mm});
            skLineSegment(sketch, "E28.1.0.136", {"start": v(-56.6, 111.03) * mm, "end": v(-57.7, 111.03) * mm});
            skLineSegment(sketch, "E28.1.0.137", {"start": v(-64.23, 88.17) * mm, "end": v(-64.23, 87.09) * mm});
            skLineSegment(sketch, "E28.1.0.138", {"start": v(-56.6, 103.41) * mm, "end": v(-57.7, 103.41) * mm});
            skLineSegment(sketch, "E28.1.0.139", {"start": v(-41.37, 80.55) * mm, "end": v(-42.45, 80.55) * mm});
            skLineSegment(sketch, "E28.1.0.140", {"start": v(-48.99, 103.41) * mm, "end": v(-48.99, 102.33) * mm});
            skLineSegment(sketch, "E28.1.0.141", {"start": v(-42.45, 111.03) * mm, "end": v(-42.45, 109.95) * mm});
            skLineSegment(sketch, "E28.1.0.142", {"start": v(-42.45, 88.17) * mm, "end": v(-42.45, 87.09) * mm});
            skLineSegment(sketch, "E28.1.0.143", {"start": v(-42.45, 80.55) * mm, "end": v(-42.45, 79.47) * mm});
            skLineSegment(sketch, "E28.1.0.144", {"start": v(-64.23, 102.33) * mm, "end": v(-65.31, 102.33) * mm});
            skLineSegment(sketch, "E28.1.0.145", {"start": v(-41.37, 111.03) * mm, "end": v(-41.37, 109.95) * mm});
            skLineSegment(sketch, "E28.1.0.146", {"start": v(-50.07, 111.03) * mm, "end": v(-50.07, 109.95) * mm});
            skLineSegment(sketch, "E28.1.0.147", {"start": v(-41.37, 80.55) * mm, "end": v(-41.37, 79.47) * mm});
            skLineSegment(sketch, "E28.1.0.148", {"start": v(-57.7, 111.03) * mm, "end": v(-57.7, 109.95) * mm});
            skLineSegment(sketch, "E28.1.0.149", {"start": v(-41.37, 87.09) * mm, "end": v(-42.45, 87.09) * mm});
            skLineSegment(sketch, "E28.1.0.150", {"start": v(-56.6, 88.17) * mm, "end": v(-57.7, 88.17) * mm});
            skLineSegment(sketch, "E28.1.0.151", {"start": v(-41.37, 95.8) * mm, "end": v(-41.37, 94.7) * mm});
            skLineSegment(sketch, "E28.1.0.152", {"start": v(-48.99, 87.09) * mm, "end": v(-50.07, 87.09) * mm});
            skLineSegment(sketch, "E28.1.0.153", {"start": v(-48.99, 88.17) * mm, "end": v(-48.99, 87.09) * mm});
            skLineSegment(sketch, "E28.1.0.154", {"start": v(-41.37, 102.33) * mm, "end": v(-42.45, 102.33) * mm});
            skLineSegment(sketch, "E28.1.0.155", {"start": v(-64.23, 103.41) * mm, "end": v(-65.31, 103.41) * mm});
            skLineSegment(sketch, "E28.1.0.156", {"start": v(-71.85, 80.55) * mm, "end": v(-72.93, 80.55) * mm});
            skLineSegment(sketch, "E28.1.0.157", {"start": v(-71.85, 95.8) * mm, "end": v(-72.93, 95.8) * mm});
            skLineSegment(sketch, "E28.1.0.158", {"start": v(-64.23, 87.09) * mm, "end": v(-65.31, 87.09) * mm});
            skLineSegment(sketch, "E28.1.0.159", {"start": v(-71.85, 111.03) * mm, "end": v(-72.93, 111.03) * mm});
            skLineSegment(sketch, "E28.1.0.160", {"start": v(-50.07, 88.17) * mm, "end": v(-50.07, 87.09) * mm});
            skLineSegment(sketch, "E28.1.0.161", {"start": v(-71.85, 109.95) * mm, "end": v(-72.93, 109.95) * mm});
            skLineSegment(sketch, "E28.1.0.162", {"start": v(-71.85, 111.03) * mm, "end": v(-71.85, 109.95) * mm});
            skLineSegment(sketch, "E28.1.0.163", {"start": v(-72.93, 103.41) * mm, "end": v(-72.93, 102.33) * mm});
            skLineSegment(sketch, "E28.1.0.164", {"start": v(-50.07, 95.8) * mm, "end": v(-50.07, 94.7) * mm});
            skLineSegment(sketch, "E28.1.0.165", {"start": v(-71.85, 95.8) * mm, "end": v(-71.85, 94.7) * mm});
            skLineSegment(sketch, "E28.1.0.166", {"start": v(-71.85, 88.17) * mm, "end": v(-71.85, 87.09) * mm});
            skLineSegment(sketch, "E28.1.0.167", {"start": v(-72.93, 111.03) * mm, "end": v(-72.93, 109.95) * mm});
            skPoint(sketch, "E28.1.2.1", {"position": v(-64.77, 3.8) * mm});
            skPoint(sketch, "E28.1.2.2", {"position": v(-49.53, 11.43) * mm});
            skPoint(sketch, "E28.1.2.3", {"position": v(-41.9, 26.67) * mm});
            skPoint(sketch, "E28.1.2.5", {"position": v(-72.39, 26.67) * mm});
            skPoint(sketch, "E28.1.2.6", {"position": v(-41.9, 11.43) * mm});
            skPoint(sketch, "E28.1.2.7", {"position": v(-41.9, 19.05) * mm});
            skPoint(sketch, "E28.1.2.8", {"position": v(-57.15, 26.67) * mm});
            skPoint(sketch, "E28.1.2.11", {"position": v(-68.58, 34.3) * mm});
            skPoint(sketch, "E28.1.2.13", {"position": v(-64.77, 11.43) * mm});
            skPoint(sketch, "E28.1.2.14", {"position": v(-57.15, 22.86) * mm});
            skPoint(sketch, "E28.1.2.16", {"position": v(-72.39, 3.8) * mm});
            skPoint(sketch, "E28.1.2.21", {"position": v(-64.77, 19.05) * mm});
            skPoint(sketch, "E28.1.2.22", {"position": v(-49.53, 19.05) * mm});
            skPoint(sketch, "E28.1.2.23", {"position": v(-41.9, 3.8) * mm});
            skPoint(sketch, "E28.1.2.24", {"position": v(-60.96, 7.62) * mm});
            skPoint(sketch, "E28.1.2.26", {"position": v(-57.15, 3.8) * mm});
            skPoint(sketch, "E28.1.2.27", {"position": v(-64.77, 26.67) * mm});
            skPoint(sketch, "E28.1.2.29", {"position": v(-49.53, 26.67) * mm});
            skPoint(sketch, "E28.1.2.30", {"position": v(-57.15, 34.3) * mm});
            skPoint(sketch, "E28.1.2.31", {"position": v(-49.53, 3.8) * mm});
            skPoint(sketch, "E28.1.2.32", {"position": v(-41.9, 34.3) * mm});
            skPoint(sketch, "E28.1.2.33", {"position": v(-57.15, 11.43) * mm});
            skPoint(sketch, "E28.1.2.34", {"position": v(-72.39, 11.43) * mm});
            skPoint(sketch, "E28.1.2.36", {"position": v(-64.77, 34.3) * mm});
            skPoint(sketch, "E28.1.2.39", {"position": v(-72.39, 19.05) * mm});
            skPoint(sketch, "E28.1.2.40", {"position": v(-53.34, 19.05) * mm});
            skPoint(sketch, "E28.1.2.42", {"position": v(-45.72, 30.48) * mm});
            skPoint(sketch, "E28.1.2.44", {"position": v(-49.53, 34.3) * mm});
            skPoint(sketch, "E28.1.2.45", {"position": v(-41.9, 34.3) * mm});
            skPoint(sketch, "E28.1.2.46", {"position": v(-72.39, 19.05) * mm});
            skPoint(sketch, "E28.1.2.47", {"position": v(-49.53, 3.8) * mm});
            skPoint(sketch, "E28.1.2.48", {"position": v(-49.53, 11.43) * mm});
            skPoint(sketch, "E28.1.2.49", {"position": v(-53.34, 19.05) * mm});
            skPoint(sketch, "E28.1.2.50", {"position": v(-72.39, 3.8) * mm});
            skPoint(sketch, "E28.1.2.51", {"position": v(-72.39, 11.43) * mm});
            skPoint(sketch, "E28.1.2.52", {"position": v(-57.15, 11.43) * mm});
            skPoint(sketch, "E28.1.2.53", {"position": v(-64.77, 26.67) * mm});
            skPoint(sketch, "E28.1.2.54", {"position": v(-57.15, 34.3) * mm});
            skPoint(sketch, "E28.1.2.55", {"position": v(-64.77, 19.05) * mm});
            skPoint(sketch, "E28.1.2.56", {"position": v(-72.39, 26.67) * mm});
            skPoint(sketch, "E28.1.2.57", {"position": v(-49.53, 19.05) * mm});
            skPoint(sketch, "E28.1.2.58", {"position": v(-49.53, 26.67) * mm});
            skPoint(sketch, "E28.1.2.59", {"position": v(-41.9, 3.8) * mm});
            skPoint(sketch, "E28.1.2.60", {"position": v(-64.77, 34.3) * mm});
            skPoint(sketch, "E28.1.2.61", {"position": v(-41.9, 19.05) * mm});
            skPoint(sketch, "E28.1.2.62", {"position": v(-49.53, 34.3) * mm});
            skPoint(sketch, "E28.1.2.63", {"position": v(-41.9, 11.43) * mm});
            skPoint(sketch, "E28.1.2.64", {"position": v(-64.77, 3.8) * mm});
            skPoint(sketch, "E28.1.2.65", {"position": v(-57.15, 22.86) * mm});
            skPoint(sketch, "E28.1.2.66", {"position": v(-64.77, 11.43) * mm});
            skPoint(sketch, "E28.1.2.67", {"position": v(-41.9, 26.67) * mm});
            skPoint(sketch, "E28.1.2.68", {"position": v(-72.39, 34.3) * mm});
            skPoint(sketch, "E28.1.2.69", {"position": v(-57.15, 26.67) * mm});
            skPoint(sketch, "E28.1.2.70", {"position": v(-57.15, 3.8) * mm});
            skLineSegment(sketch, "E28.1.2.71", {"start": v(-48.99, 19.6) * mm, "end": v(-48.99, 18.5) * mm});
            skPoint(sketch, "E28.1.2.72", {"position": v(-72.39, 34.3) * mm});
            skLineSegment(sketch, "E28.1.2.73", {"start": v(-48.99, 18.5) * mm, "end": v(-50.07, 18.5) * mm});
            skLineSegment(sketch, "E28.1.2.74", {"start": v(-41.37, 3.27) * mm, "end": v(-42.45, 3.27) * mm});
            skLineSegment(sketch, "E28.1.2.75", {"start": v(-57.7, 4.35) * mm, "end": v(-57.7, 3.27) * mm});
            skLineSegment(sketch, "E28.1.2.76", {"start": v(-56.6, 11.97) * mm, "end": v(-56.6, 10.89) * mm});
            skLineSegment(sketch, "E28.1.2.77", {"start": v(-64.23, 3.27) * mm, "end": v(-65.31, 3.27) * mm});
            skLineSegment(sketch, "E28.1.2.78", {"start": v(-65.31, 19.6) * mm, "end": v(-65.31, 18.5) * mm});
            skLineSegment(sketch, "E28.1.2.79", {"start": v(-65.31, 4.35) * mm, "end": v(-65.31, 3.27) * mm});
            skLineSegment(sketch, "E28.1.2.80", {"start": v(-64.23, 33.75) * mm, "end": v(-65.31, 33.75) * mm});
            skLineSegment(sketch, "E28.1.2.81", {"start": v(-64.23, 34.83) * mm, "end": v(-65.31, 34.83) * mm});
            skLineSegment(sketch, "E28.1.2.82", {"start": v(-72.93, 11.97) * mm, "end": v(-72.93, 10.89) * mm});
            skLineSegment(sketch, "E28.1.2.83", {"start": v(-41.37, 27.21) * mm, "end": v(-42.45, 27.21) * mm});
            skLineSegment(sketch, "E28.1.2.84", {"start": v(-64.23, 19.6) * mm, "end": v(-64.23, 18.5) * mm});
            skLineSegment(sketch, "E28.1.2.85", {"start": v(-48.99, 11.97) * mm, "end": v(-50.07, 11.97) * mm});
            skLineSegment(sketch, "E28.1.2.86", {"start": v(-56.6, 26.13) * mm, "end": v(-57.7, 26.13) * mm});
            skLineSegment(sketch, "E28.1.2.87", {"start": v(-48.99, 26.13) * mm, "end": v(-50.07, 26.13) * mm});
            skLineSegment(sketch, "E28.1.2.88", {"start": v(-71.85, 11.97) * mm, "end": v(-72.93, 11.97) * mm});
            skLineSegment(sketch, "E28.1.2.89", {"start": v(-64.23, 11.97) * mm, "end": v(-65.31, 11.97) * mm});
            skLineSegment(sketch, "E28.1.2.90", {"start": v(-71.85, 3.27) * mm, "end": v(-72.93, 3.27) * mm});
            skLineSegment(sketch, "E28.1.2.91", {"start": v(-71.85, 26.13) * mm, "end": v(-72.93, 26.13) * mm});
            skLineSegment(sketch, "E28.1.2.92", {"start": v(-65.31, 11.97) * mm, "end": v(-65.31, 10.89) * mm});
            skLineSegment(sketch, "E28.1.2.93", {"start": v(-56.6, 3.27) * mm, "end": v(-57.7, 3.27) * mm});
            skLineSegment(sketch, "E28.1.2.94", {"start": v(-71.85, 18.5) * mm, "end": v(-72.93, 18.5) * mm});
            skLineSegment(sketch, "E28.1.2.95", {"start": v(-57.7, 27.21) * mm, "end": v(-57.7, 26.13) * mm});
            skLineSegment(sketch, "E28.1.2.96", {"start": v(-48.99, 19.6) * mm, "end": v(-50.07, 19.6) * mm});
            skLineSegment(sketch, "E28.1.2.97", {"start": v(-50.07, 4.35) * mm, "end": v(-50.07, 3.27) * mm});
            skLineSegment(sketch, "E28.1.2.98", {"start": v(-41.37, 27.21) * mm, "end": v(-41.37, 26.13) * mm});
            skLineSegment(sketch, "E28.1.2.99", {"start": v(-71.85, 4.35) * mm, "end": v(-71.85, 3.27) * mm});
            skLineSegment(sketch, "E28.1.2.100", {"start": v(-72.93, 19.6) * mm, "end": v(-72.93, 18.5) * mm});
            skLineSegment(sketch, "E28.1.2.101", {"start": v(-71.85, 27.21) * mm, "end": v(-72.93, 27.21) * mm});
            skLineSegment(sketch, "E28.1.2.102", {"start": v(-41.37, 11.97) * mm, "end": v(-41.37, 10.89) * mm});
            skLineSegment(sketch, "E28.1.2.103", {"start": v(-64.23, 4.35) * mm, "end": v(-65.31, 4.35) * mm});
            skLineSegment(sketch, "E28.1.2.104", {"start": v(-41.37, 18.5) * mm, "end": v(-42.45, 18.5) * mm});
            skLineSegment(sketch, "E28.1.2.105", {"start": v(-48.99, 34.83) * mm, "end": v(-48.99, 33.75) * mm});
            skLineSegment(sketch, "E28.1.2.106", {"start": v(-48.99, 4.35) * mm, "end": v(-48.99, 3.27) * mm});
            skLineSegment(sketch, "E28.1.2.107", {"start": v(-65.31, 27.21) * mm, "end": v(-65.31, 26.13) * mm});
            skLineSegment(sketch, "E28.1.2.108", {"start": v(-56.6, 10.89) * mm, "end": v(-57.7, 10.89) * mm});
            skLineSegment(sketch, "E28.1.2.109", {"start": v(-64.23, 27.21) * mm, "end": v(-64.23, 26.13) * mm});
            skLineSegment(sketch, "E28.1.2.110", {"start": v(-42.45, 19.6) * mm, "end": v(-42.45, 18.5) * mm});
            skLineSegment(sketch, "E28.1.2.111", {"start": v(-48.99, 3.27) * mm, "end": v(-50.07, 3.27) * mm});
            skLineSegment(sketch, "E28.1.2.112", {"start": v(-64.23, 34.83) * mm, "end": v(-64.23, 33.75) * mm});
            skLineSegment(sketch, "E28.1.2.113", {"start": v(-56.6, 4.35) * mm, "end": v(-56.6, 3.27) * mm});
            skLineSegment(sketch, "E28.1.2.114", {"start": v(-64.23, 19.6) * mm, "end": v(-65.31, 19.6) * mm});
            skLineSegment(sketch, "E28.1.2.115", {"start": v(-64.23, 18.5) * mm, "end": v(-65.31, 18.5) * mm});
            skLineSegment(sketch, "E28.1.2.116", {"start": v(-48.99, 4.35) * mm, "end": v(-50.07, 4.35) * mm});
            skLineSegment(sketch, "E28.1.2.117", {"start": v(-64.23, 4.35) * mm, "end": v(-64.23, 3.27) * mm});
            skLineSegment(sketch, "E28.1.2.118", {"start": v(-41.37, 19.6) * mm, "end": v(-42.45, 19.6) * mm});
            skLineSegment(sketch, "E28.1.2.119", {"start": v(-50.07, 27.21) * mm, "end": v(-50.07, 26.13) * mm});
            skLineSegment(sketch, "E28.1.2.120", {"start": v(-71.85, 10.89) * mm, "end": v(-72.93, 10.89) * mm});
            skLineSegment(sketch, "E28.1.2.121", {"start": v(-41.37, 11.97) * mm, "end": v(-42.45, 11.97) * mm});
            skLineSegment(sketch, "E28.1.2.122", {"start": v(-72.93, 4.35) * mm, "end": v(-72.93, 3.27) * mm});
            skLineSegment(sketch, "E28.1.2.123", {"start": v(-56.6, 34.83) * mm, "end": v(-56.6, 33.75) * mm});
            skLineSegment(sketch, "E28.1.2.124", {"start": v(-56.6, 27.21) * mm, "end": v(-56.6, 26.13) * mm});
            skLineSegment(sketch, "E28.1.2.125", {"start": v(-41.37, 33.75) * mm, "end": v(-42.45, 33.75) * mm});
            skLineSegment(sketch, "E28.1.2.126", {"start": v(-42.45, 27.21) * mm, "end": v(-42.45, 26.13) * mm});
            skLineSegment(sketch, "E28.1.2.127", {"start": v(-48.99, 34.83) * mm, "end": v(-50.07, 34.83) * mm});
            skLineSegment(sketch, "E28.1.2.128", {"start": v(-57.7, 11.97) * mm, "end": v(-57.7, 10.89) * mm});
            skLineSegment(sketch, "E28.1.2.129", {"start": v(-56.6, 33.75) * mm, "end": v(-57.7, 33.75) * mm});
            skLineSegment(sketch, "E28.1.2.130", {"start": v(-48.99, 33.75) * mm, "end": v(-50.07, 33.75) * mm});
            skLineSegment(sketch, "E28.1.2.131", {"start": v(-65.31, 34.83) * mm, "end": v(-65.31, 33.75) * mm});
            skLineSegment(sketch, "E28.1.2.132", {"start": v(-71.85, 27.21) * mm, "end": v(-71.85, 26.13) * mm});
            skLineSegment(sketch, "E28.1.2.133", {"start": v(-41.37, 34.83) * mm, "end": v(-42.45, 34.83) * mm});
            skLineSegment(sketch, "E28.1.2.134", {"start": v(-56.6, 4.35) * mm, "end": v(-57.7, 4.35) * mm});
            skLineSegment(sketch, "E28.1.2.135", {"start": v(-48.99, 27.21) * mm, "end": v(-50.07, 27.21) * mm});
            skLineSegment(sketch, "E28.1.2.136", {"start": v(-56.6, 34.83) * mm, "end": v(-57.7, 34.83) * mm});
            skLineSegment(sketch, "E28.1.2.137", {"start": v(-64.23, 11.97) * mm, "end": v(-64.23, 10.89) * mm});
            skLineSegment(sketch, "E28.1.2.138", {"start": v(-56.6, 27.21) * mm, "end": v(-57.7, 27.21) * mm});
            skLineSegment(sketch, "E28.1.2.139", {"start": v(-41.37, 4.35) * mm, "end": v(-42.45, 4.35) * mm});
            skLineSegment(sketch, "E28.1.2.140", {"start": v(-48.99, 27.21) * mm, "end": v(-48.99, 26.13) * mm});
            skLineSegment(sketch, "E28.1.2.141", {"start": v(-42.45, 34.83) * mm, "end": v(-42.45, 33.75) * mm});
            skLineSegment(sketch, "E28.1.2.142", {"start": v(-42.45, 11.97) * mm, "end": v(-42.45, 10.89) * mm});
            skLineSegment(sketch, "E28.1.2.143", {"start": v(-42.45, 4.35) * mm, "end": v(-42.45, 3.27) * mm});
            skLineSegment(sketch, "E28.1.2.144", {"start": v(-64.23, 26.13) * mm, "end": v(-65.31, 26.13) * mm});
            skLineSegment(sketch, "E28.1.2.145", {"start": v(-41.37, 34.83) * mm, "end": v(-41.37, 33.75) * mm});
            skLineSegment(sketch, "E28.1.2.146", {"start": v(-50.07, 34.83) * mm, "end": v(-50.07, 33.75) * mm});
            skLineSegment(sketch, "E28.1.2.147", {"start": v(-41.37, 4.35) * mm, "end": v(-41.37, 3.27) * mm});
            skLineSegment(sketch, "E28.1.2.148", {"start": v(-57.7, 34.83) * mm, "end": v(-57.7, 33.75) * mm});
            skLineSegment(sketch, "E28.1.2.149", {"start": v(-41.37, 10.89) * mm, "end": v(-42.45, 10.89) * mm});
            skLineSegment(sketch, "E28.1.2.150", {"start": v(-56.6, 11.97) * mm, "end": v(-57.7, 11.97) * mm});
            skLineSegment(sketch, "E28.1.2.151", {"start": v(-41.37, 19.6) * mm, "end": v(-41.37, 18.5) * mm});
            skLineSegment(sketch, "E28.1.2.152", {"start": v(-48.99, 10.89) * mm, "end": v(-50.07, 10.89) * mm});
            skLineSegment(sketch, "E28.1.2.153", {"start": v(-48.99, 11.97) * mm, "end": v(-48.99, 10.89) * mm});
            skLineSegment(sketch, "E28.1.2.154", {"start": v(-41.37, 26.13) * mm, "end": v(-42.45, 26.13) * mm});
            skLineSegment(sketch, "E28.1.2.155", {"start": v(-64.23, 27.21) * mm, "end": v(-65.31, 27.21) * mm});
            skLineSegment(sketch, "E28.1.2.156", {"start": v(-71.85, 4.35) * mm, "end": v(-72.93, 4.35) * mm});
            skLineSegment(sketch, "E28.1.2.157", {"start": v(-71.85, 19.6) * mm, "end": v(-72.93, 19.6) * mm});
            skLineSegment(sketch, "E28.1.2.158", {"start": v(-64.23, 10.89) * mm, "end": v(-65.31, 10.89) * mm});
            skLineSegment(sketch, "E28.1.2.159", {"start": v(-71.85, 34.83) * mm, "end": v(-72.93, 34.83) * mm});
            skLineSegment(sketch, "E28.1.2.160", {"start": v(-50.07, 11.97) * mm, "end": v(-50.07, 10.89) * mm});
            skLineSegment(sketch, "E28.1.2.161", {"start": v(-71.85, 33.75) * mm, "end": v(-72.93, 33.75) * mm});
            skLineSegment(sketch, "E28.1.2.162", {"start": v(-71.85, 34.83) * mm, "end": v(-71.85, 33.75) * mm});
            skLineSegment(sketch, "E28.1.2.163", {"start": v(-72.93, 27.21) * mm, "end": v(-72.93, 26.13) * mm});
            skLineSegment(sketch, "E28.1.2.164", {"start": v(-50.07, 19.6) * mm, "end": v(-50.07, 18.5) * mm});
            skLineSegment(sketch, "E28.1.2.165", {"start": v(-71.85, 19.6) * mm, "end": v(-71.85, 18.5) * mm});
            skLineSegment(sketch, "E28.1.2.166", {"start": v(-71.85, 11.97) * mm, "end": v(-71.85, 10.89) * mm});
            skLineSegment(sketch, "E28.1.2.167", {"start": v(-72.93, 34.83) * mm, "end": v(-72.93, 33.75) * mm});
            skPoint(sketch, "E28.2.0.1", {"position": v(-26.67, 80) * mm});
            skPoint(sketch, "E28.2.0.2", {"position": v(-11.43, 87.63) * mm});
            skPoint(sketch, "E28.2.0.3", {"position": v(-3.8, 102.87) * mm});
            skPoint(sketch, "E28.2.0.5", {"position": v(-34.29, 102.87) * mm});
            skPoint(sketch, "E28.2.0.6", {"position": v(-3.8, 87.63) * mm});
            skPoint(sketch, "E28.2.0.7", {"position": v(-3.8, 95.25) * mm});
            skPoint(sketch, "E28.2.0.8", {"position": v(-19.05, 102.87) * mm});
            skPoint(sketch, "E28.2.0.11", {"position": v(-30.48, 110.5) * mm});
            skPoint(sketch, "E28.2.0.13", {"position": v(-26.67, 87.63) * mm});
            skPoint(sketch, "E28.2.0.14", {"position": v(-19.05, 99.06) * mm});
            skPoint(sketch, "E28.2.0.16", {"position": v(-34.29, 80) * mm});
            skPoint(sketch, "E28.2.0.21", {"position": v(-26.67, 95.25) * mm});
            skPoint(sketch, "E28.2.0.22", {"position": v(-11.43, 95.25) * mm});
            skPoint(sketch, "E28.2.0.23", {"position": v(-3.8, 80) * mm});
            skPoint(sketch, "E28.2.0.24", {"position": v(-22.86, 83.82) * mm});
            skPoint(sketch, "E28.2.0.26", {"position": v(-19.05, 80) * mm});
            skPoint(sketch, "E28.2.0.27", {"position": v(-26.67, 102.87) * mm});
            skPoint(sketch, "E28.2.0.29", {"position": v(-11.43, 102.87) * mm});
            skPoint(sketch, "E28.2.0.30", {"position": v(-19.05, 110.5) * mm});
            skPoint(sketch, "E28.2.0.31", {"position": v(-11.43, 80) * mm});
            skPoint(sketch, "E28.2.0.32", {"position": v(-3.8, 110.5) * mm});
            skPoint(sketch, "E28.2.0.33", {"position": v(-19.05, 87.63) * mm});
            skPoint(sketch, "E28.2.0.34", {"position": v(-34.29, 87.63) * mm});
            skPoint(sketch, "E28.2.0.36", {"position": v(-26.67, 110.5) * mm});
            skPoint(sketch, "E28.2.0.39", {"position": v(-34.29, 95.25) * mm});
            skPoint(sketch, "E28.2.0.40", {"position": v(-15.24, 95.25) * mm});
            skPoint(sketch, "E28.2.0.42", {"position": v(-7.62, 106.68) * mm});
            skPoint(sketch, "E28.2.0.44", {"position": v(-11.43, 110.5) * mm});
            skPoint(sketch, "E28.2.0.45", {"position": v(-3.8, 110.5) * mm});
            skPoint(sketch, "E28.2.0.46", {"position": v(-34.29, 95.25) * mm});
            skPoint(sketch, "E28.2.0.47", {"position": v(-11.43, 80) * mm});
            skPoint(sketch, "E28.2.0.48", {"position": v(-11.43, 87.63) * mm});
            skPoint(sketch, "E28.2.0.49", {"position": v(-15.24, 95.25) * mm});
            skPoint(sketch, "E28.2.0.50", {"position": v(-34.29, 80) * mm});
            skPoint(sketch, "E28.2.0.51", {"position": v(-34.29, 87.63) * mm});
            skPoint(sketch, "E28.2.0.52", {"position": v(-19.05, 87.63) * mm});
            skPoint(sketch, "E28.2.0.53", {"position": v(-26.67, 102.87) * mm});
            skPoint(sketch, "E28.2.0.54", {"position": v(-19.05, 110.5) * mm});
            skPoint(sketch, "E28.2.0.55", {"position": v(-26.67, 95.25) * mm});
            skPoint(sketch, "E28.2.0.56", {"position": v(-34.29, 102.87) * mm});
            skPoint(sketch, "E28.2.0.57", {"position": v(-11.43, 95.25) * mm});
            skPoint(sketch, "E28.2.0.58", {"position": v(-11.43, 102.87) * mm});
            skPoint(sketch, "E28.2.0.59", {"position": v(-3.8, 80) * mm});
            skPoint(sketch, "E28.2.0.60", {"position": v(-26.67, 110.5) * mm});
            skPoint(sketch, "E28.2.0.61", {"position": v(-3.8, 95.25) * mm});
            skPoint(sketch, "E28.2.0.62", {"position": v(-11.43, 110.5) * mm});
            skPoint(sketch, "E28.2.0.63", {"position": v(-3.8, 87.63) * mm});
            skPoint(sketch, "E28.2.0.64", {"position": v(-26.67, 80) * mm});
            skPoint(sketch, "E28.2.0.65", {"position": v(-19.05, 99.06) * mm});
            skPoint(sketch, "E28.2.0.66", {"position": v(-26.67, 87.63) * mm});
            skPoint(sketch, "E28.2.0.67", {"position": v(-3.8, 102.87) * mm});
            skPoint(sketch, "E28.2.0.68", {"position": v(-34.29, 110.5) * mm});
            skPoint(sketch, "E28.2.0.69", {"position": v(-19.05, 102.87) * mm});
            skPoint(sketch, "E28.2.0.70", {"position": v(-19.05, 80) * mm});
            skPoint(sketch, "E28.2.0.72", {"position": v(-34.29, 110.5) * mm});
            skLineSegment(sketch, "E28.2.0.73", {"start": v(-10.89, 94.7) * mm, "end": v(-11.97, 94.7) * mm});
            skLineSegment(sketch, "E28.2.0.74", {"start": v(-3.27, 79.47) * mm, "end": v(-4.35, 79.47) * mm});
            skLineSegment(sketch, "E28.2.0.75", {"start": v(-19.6, 80.55) * mm, "end": v(-19.6, 79.47) * mm});
            skLineSegment(sketch, "E28.2.0.76", {"start": v(-18.5, 88.17) * mm, "end": v(-18.5, 87.09) * mm});
            skLineSegment(sketch, "E28.2.0.77", {"start": v(-26.13, 79.47) * mm, "end": v(-27.21, 79.47) * mm});
            skLineSegment(sketch, "E28.2.0.78", {"start": v(-27.21, 95.8) * mm, "end": v(-27.21, 94.7) * mm});
            skLineSegment(sketch, "E28.2.0.79", {"start": v(-27.21, 80.55) * mm, "end": v(-27.21, 79.47) * mm});
            skLineSegment(sketch, "E28.2.0.80", {"start": v(-26.13, 109.95) * mm, "end": v(-27.21, 109.95) * mm});
            skLineSegment(sketch, "E28.2.0.81", {"start": v(-26.13, 111.03) * mm, "end": v(-27.21, 111.03) * mm});
            skLineSegment(sketch, "E28.2.0.82", {"start": v(-34.83, 88.17) * mm, "end": v(-34.83, 87.09) * mm});
            skLineSegment(sketch, "E28.2.0.83", {"start": v(-3.27, 103.41) * mm, "end": v(-4.35, 103.41) * mm});
            skLineSegment(sketch, "E28.2.0.84", {"start": v(-26.13, 95.8) * mm, "end": v(-26.13, 94.7) * mm});
            skLineSegment(sketch, "E28.2.0.85", {"start": v(-10.89, 88.17) * mm, "end": v(-11.97, 88.17) * mm});
            skLineSegment(sketch, "E28.2.0.86", {"start": v(-18.5, 102.33) * mm, "end": v(-19.6, 102.33) * mm});
            skLineSegment(sketch, "E28.2.0.87", {"start": v(-10.89, 102.33) * mm, "end": v(-11.97, 102.33) * mm});
            skLineSegment(sketch, "E28.2.0.88", {"start": v(-33.75, 88.17) * mm, "end": v(-34.83, 88.17) * mm});
            skLineSegment(sketch, "E28.2.0.89", {"start": v(-26.13, 88.17) * mm, "end": v(-27.21, 88.17) * mm});
            skLineSegment(sketch, "E28.2.0.90", {"start": v(-33.75, 79.47) * mm, "end": v(-34.83, 79.47) * mm});
            skLineSegment(sketch, "E28.2.0.91", {"start": v(-33.75, 102.33) * mm, "end": v(-34.83, 102.33) * mm});
            skLineSegment(sketch, "E28.2.0.92", {"start": v(-27.21, 88.17) * mm, "end": v(-27.21, 87.09) * mm});
            skLineSegment(sketch, "E28.2.0.93", {"start": v(-18.5, 79.47) * mm, "end": v(-19.6, 79.47) * mm});
            skLineSegment(sketch, "E28.2.0.94", {"start": v(-33.75, 94.7) * mm, "end": v(-34.83, 94.7) * mm});
            skLineSegment(sketch, "E28.2.0.95", {"start": v(-19.6, 103.41) * mm, "end": v(-19.6, 102.33) * mm});
            skLineSegment(sketch, "E28.2.0.96", {"start": v(-10.89, 95.8) * mm, "end": v(-11.97, 95.8) * mm});
            skLineSegment(sketch, "E28.2.0.97", {"start": v(-11.97, 80.55) * mm, "end": v(-11.97, 79.47) * mm});
            skLineSegment(sketch, "E28.2.0.98", {"start": v(-3.27, 103.41) * mm, "end": v(-3.27, 102.33) * mm});
            skLineSegment(sketch, "E28.2.0.99", {"start": v(-33.75, 80.55) * mm, "end": v(-33.75, 79.47) * mm});
            skLineSegment(sketch, "E28.2.0.100", {"start": v(-34.83, 95.8) * mm, "end": v(-34.83, 94.7) * mm});
            skLineSegment(sketch, "E28.2.0.101", {"start": v(-33.75, 103.41) * mm, "end": v(-34.83, 103.41) * mm});
            skLineSegment(sketch, "E28.2.0.102", {"start": v(-3.27, 88.17) * mm, "end": v(-3.27, 87.09) * mm});
            skLineSegment(sketch, "E28.2.0.103", {"start": v(-26.13, 80.55) * mm, "end": v(-27.21, 80.55) * mm});
            skLineSegment(sketch, "E28.2.0.104", {"start": v(-3.27, 94.7) * mm, "end": v(-4.35, 94.7) * mm});
            skLineSegment(sketch, "E28.2.0.105", {"start": v(-10.89, 111.03) * mm, "end": v(-10.89, 109.95) * mm});
            skLineSegment(sketch, "E28.2.0.106", {"start": v(-10.89, 80.55) * mm, "end": v(-10.89, 79.47) * mm});
            skLineSegment(sketch, "E28.2.0.107", {"start": v(-27.21, 103.41) * mm, "end": v(-27.21, 102.33) * mm});
            skLineSegment(sketch, "E28.2.0.108", {"start": v(-18.5, 87.09) * mm, "end": v(-19.6, 87.09) * mm});
            skLineSegment(sketch, "E28.2.0.109", {"start": v(-26.13, 103.41) * mm, "end": v(-26.13, 102.33) * mm});
            skLineSegment(sketch, "E28.2.0.110", {"start": v(-4.35, 95.8) * mm, "end": v(-4.35, 94.7) * mm});
            skLineSegment(sketch, "E28.2.0.111", {"start": v(-10.89, 79.47) * mm, "end": v(-11.97, 79.47) * mm});
            skLineSegment(sketch, "E28.2.0.112", {"start": v(-26.13, 111.03) * mm, "end": v(-26.13, 109.95) * mm});
            skLineSegment(sketch, "E28.2.0.113", {"start": v(-18.5, 80.55) * mm, "end": v(-18.5, 79.47) * mm});
            skLineSegment(sketch, "E28.2.0.114", {"start": v(-26.13, 95.8) * mm, "end": v(-27.21, 95.8) * mm});
            skLineSegment(sketch, "E28.2.0.115", {"start": v(-26.13, 94.7) * mm, "end": v(-27.21, 94.7) * mm});
            skLineSegment(sketch, "E28.2.0.116", {"start": v(-10.89, 80.55) * mm, "end": v(-11.97, 80.55) * mm});
            skLineSegment(sketch, "E28.2.0.117", {"start": v(-26.13, 80.55) * mm, "end": v(-26.13, 79.47) * mm});
            skLineSegment(sketch, "E28.2.0.118", {"start": v(-3.27, 95.8) * mm, "end": v(-4.35, 95.8) * mm});
            skLineSegment(sketch, "E28.2.0.119", {"start": v(-11.97, 103.41) * mm, "end": v(-11.97, 102.33) * mm});
            skLineSegment(sketch, "E28.2.0.120", {"start": v(-33.75, 87.09) * mm, "end": v(-34.83, 87.09) * mm});
            skLineSegment(sketch, "E28.2.0.121", {"start": v(-3.27, 88.17) * mm, "end": v(-4.35, 88.17) * mm});
            skLineSegment(sketch, "E28.2.0.122", {"start": v(-34.83, 80.55) * mm, "end": v(-34.83, 79.47) * mm});
            skLineSegment(sketch, "E28.2.0.123", {"start": v(-18.5, 111.03) * mm, "end": v(-18.5, 109.95) * mm});
            skLineSegment(sketch, "E28.2.0.124", {"start": v(-18.5, 103.41) * mm, "end": v(-18.5, 102.33) * mm});
            skLineSegment(sketch, "E28.2.0.125", {"start": v(-3.27, 109.95) * mm, "end": v(-4.35, 109.95) * mm});
            skLineSegment(sketch, "E28.2.0.126", {"start": v(-4.35, 103.41) * mm, "end": v(-4.35, 102.33) * mm});
            skLineSegment(sketch, "E28.2.0.127", {"start": v(-10.89, 111.03) * mm, "end": v(-11.97, 111.03) * mm});
            skLineSegment(sketch, "E28.2.0.128", {"start": v(-19.6, 88.17) * mm, "end": v(-19.6, 87.09) * mm});
            skLineSegment(sketch, "E28.2.0.129", {"start": v(-18.5, 109.95) * mm, "end": v(-19.6, 109.95) * mm});
            skLineSegment(sketch, "E28.2.0.130", {"start": v(-10.89, 109.95) * mm, "end": v(-11.97, 109.95) * mm});
            skLineSegment(sketch, "E28.2.0.131", {"start": v(-27.21, 111.03) * mm, "end": v(-27.21, 109.95) * mm});
            skLineSegment(sketch, "E28.2.0.132", {"start": v(-33.75, 103.41) * mm, "end": v(-33.75, 102.33) * mm});
            skLineSegment(sketch, "E28.2.0.133", {"start": v(-3.27, 111.03) * mm, "end": v(-4.35, 111.03) * mm});
            skLineSegment(sketch, "E28.2.0.134", {"start": v(-18.5, 80.55) * mm, "end": v(-19.6, 80.55) * mm});
            skLineSegment(sketch, "E28.2.0.135", {"start": v(-10.89, 103.41) * mm, "end": v(-11.97, 103.41) * mm});
            skLineSegment(sketch, "E28.2.0.136", {"start": v(-18.5, 111.03) * mm, "end": v(-19.6, 111.03) * mm});
            skLineSegment(sketch, "E28.2.0.137", {"start": v(-26.13, 88.17) * mm, "end": v(-26.13, 87.09) * mm});
            skLineSegment(sketch, "E28.2.0.138", {"start": v(-18.5, 103.41) * mm, "end": v(-19.6, 103.41) * mm});
            skLineSegment(sketch, "E28.2.0.139", {"start": v(-3.27, 80.55) * mm, "end": v(-4.35, 80.55) * mm});
            skLineSegment(sketch, "E28.2.0.140", {"start": v(-10.89, 103.41) * mm, "end": v(-10.89, 102.33) * mm});
            skLineSegment(sketch, "E28.2.0.141", {"start": v(-4.35, 111.03) * mm, "end": v(-4.35, 109.95) * mm});
            skLineSegment(sketch, "E28.2.0.142", {"start": v(-4.35, 88.17) * mm, "end": v(-4.35, 87.09) * mm});
            skLineSegment(sketch, "E28.2.0.143", {"start": v(-4.35, 80.55) * mm, "end": v(-4.35, 79.47) * mm});
            skLineSegment(sketch, "E28.2.0.144", {"start": v(-26.13, 102.33) * mm, "end": v(-27.21, 102.33) * mm});
            skLineSegment(sketch, "E28.2.0.145", {"start": v(-3.27, 111.03) * mm, "end": v(-3.27, 109.95) * mm});
            skLineSegment(sketch, "E28.2.0.146", {"start": v(-11.97, 111.03) * mm, "end": v(-11.97, 109.95) * mm});
            skLineSegment(sketch, "E28.2.0.147", {"start": v(-3.27, 80.55) * mm, "end": v(-3.27, 79.47) * mm});
            skLineSegment(sketch, "E28.2.0.148", {"start": v(-19.6, 111.03) * mm, "end": v(-19.6, 109.95) * mm});
            skLineSegment(sketch, "E28.2.0.149", {"start": v(-3.27, 87.09) * mm, "end": v(-4.35, 87.09) * mm});
            skLineSegment(sketch, "E28.2.0.150", {"start": v(-18.5, 88.17) * mm, "end": v(-19.6, 88.17) * mm});
            skLineSegment(sketch, "E28.2.0.151", {"start": v(-3.27, 95.8) * mm, "end": v(-3.27, 94.7) * mm});
            skLineSegment(sketch, "E28.2.0.152", {"start": v(-10.89, 87.09) * mm, "end": v(-11.97, 87.09) * mm});
            skLineSegment(sketch, "E28.2.0.153", {"start": v(-10.89, 88.17) * mm, "end": v(-10.89, 87.09) * mm});
            skLineSegment(sketch, "E28.2.0.154", {"start": v(-3.27, 102.33) * mm, "end": v(-4.35, 102.33) * mm});
            skLineSegment(sketch, "E28.2.0.155", {"start": v(-26.13, 103.41) * mm, "end": v(-27.21, 103.41) * mm});
            skLineSegment(sketch, "E28.2.0.156", {"start": v(-33.75, 80.55) * mm, "end": v(-34.83, 80.55) * mm});
            skLineSegment(sketch, "E28.2.0.157", {"start": v(-33.75, 95.8) * mm, "end": v(-34.83, 95.8) * mm});
            skLineSegment(sketch, "E28.2.0.158", {"start": v(-26.13, 87.09) * mm, "end": v(-27.21, 87.09) * mm});
            skLineSegment(sketch, "E28.2.0.159", {"start": v(-33.75, 111.03) * mm, "end": v(-34.83, 111.03) * mm});
            skLineSegment(sketch, "E28.2.0.160", {"start": v(-11.97, 88.17) * mm, "end": v(-11.97, 87.09) * mm});
            skLineSegment(sketch, "E28.2.0.161", {"start": v(-33.75, 109.95) * mm, "end": v(-34.83, 109.95) * mm});
            skLineSegment(sketch, "E28.2.0.162", {"start": v(-33.75, 111.03) * mm, "end": v(-33.75, 109.95) * mm});
            skLineSegment(sketch, "E28.2.0.163", {"start": v(-34.83, 103.41) * mm, "end": v(-34.83, 102.33) * mm});
            skLineSegment(sketch, "E28.2.0.164", {"start": v(-11.97, 95.8) * mm, "end": v(-11.97, 94.7) * mm});
            skLineSegment(sketch, "E28.2.0.165", {"start": v(-33.75, 95.8) * mm, "end": v(-33.75, 94.7) * mm});
            skLineSegment(sketch, "E28.2.0.166", {"start": v(-33.75, 88.17) * mm, "end": v(-33.75, 87.09) * mm});
            skLineSegment(sketch, "E28.2.0.167", {"start": v(-34.83, 111.03) * mm, "end": v(-34.83, 109.95) * mm});
            skPoint(sketch, "E28.2.1.1", {"position": v(-26.67, 41.9) * mm});
            skPoint(sketch, "E28.2.1.2", {"position": v(-11.43, 49.53) * mm});
            skPoint(sketch, "E28.2.1.3", {"position": v(-3.8, 64.77) * mm});
            skPoint(sketch, "E28.2.1.5", {"position": v(-34.29, 64.77) * mm});
            skPoint(sketch, "E28.2.1.6", {"position": v(-3.8, 49.53) * mm});
            skPoint(sketch, "E28.2.1.7", {"position": v(-3.8, 57.15) * mm});
            skPoint(sketch, "E28.2.1.8", {"position": v(-19.05, 64.77) * mm});
            skPoint(sketch, "E28.2.1.11", {"position": v(-30.48, 72.4) * mm});
            skPoint(sketch, "E28.2.1.13", {"position": v(-26.67, 49.53) * mm});
            skPoint(sketch, "E28.2.1.14", {"position": v(-19.05, 60.96) * mm});
            skPoint(sketch, "E28.2.1.16", {"position": v(-34.29, 41.9) * mm});
            skPoint(sketch, "E28.2.1.21", {"position": v(-26.67, 57.15) * mm});
            skPoint(sketch, "E28.2.1.22", {"position": v(-11.43, 57.15) * mm});
            skPoint(sketch, "E28.2.1.23", {"position": v(-3.8, 41.9) * mm});
            skPoint(sketch, "E28.2.1.24", {"position": v(-22.86, 45.72) * mm});
            skPoint(sketch, "E28.2.1.26", {"position": v(-19.05, 41.9) * mm});
            skPoint(sketch, "E28.2.1.27", {"position": v(-26.67, 64.77) * mm});
            skPoint(sketch, "E28.2.1.29", {"position": v(-11.43, 64.77) * mm});
            skPoint(sketch, "E28.2.1.30", {"position": v(-19.05, 72.4) * mm});
            skPoint(sketch, "E28.2.1.31", {"position": v(-11.43, 41.9) * mm});
            skPoint(sketch, "E28.2.1.32", {"position": v(-3.8, 72.4) * mm});
            skPoint(sketch, "E28.2.1.33", {"position": v(-19.05, 49.53) * mm});
            skPoint(sketch, "E28.2.1.34", {"position": v(-34.29, 49.53) * mm});
            skPoint(sketch, "E28.2.1.36", {"position": v(-26.67, 72.4) * mm});
            skPoint(sketch, "E28.2.1.39", {"position": v(-34.29, 57.15) * mm});
            skPoint(sketch, "E28.2.1.40", {"position": v(-15.24, 57.15) * mm});
            skPoint(sketch, "E28.2.1.42", {"position": v(-7.62, 68.58) * mm});
            skPoint(sketch, "E28.2.1.44", {"position": v(-11.43, 72.4) * mm});
            skPoint(sketch, "E28.2.1.45", {"position": v(-3.8, 72.4) * mm});
            skPoint(sketch, "E28.2.1.46", {"position": v(-34.29, 57.15) * mm});
            skPoint(sketch, "E28.2.1.47", {"position": v(-11.43, 41.9) * mm});
            skPoint(sketch, "E28.2.1.48", {"position": v(-11.43, 49.53) * mm});
            skPoint(sketch, "E28.2.1.49", {"position": v(-15.24, 57.15) * mm});
            skPoint(sketch, "E28.2.1.50", {"position": v(-34.29, 41.9) * mm});
            skPoint(sketch, "E28.2.1.51", {"position": v(-34.29, 49.53) * mm});
            skPoint(sketch, "E28.2.1.52", {"position": v(-19.05, 49.53) * mm});
            skPoint(sketch, "E28.2.1.53", {"position": v(-26.67, 64.77) * mm});
            skPoint(sketch, "E28.2.1.54", {"position": v(-19.05, 72.4) * mm});
            skPoint(sketch, "E28.2.1.55", {"position": v(-26.67, 57.15) * mm});
            skPoint(sketch, "E28.2.1.56", {"position": v(-34.29, 64.77) * mm});
            skPoint(sketch, "E28.2.1.57", {"position": v(-11.43, 57.15) * mm});
            skPoint(sketch, "E28.2.1.58", {"position": v(-11.43, 64.77) * mm});
            skPoint(sketch, "E28.2.1.59", {"position": v(-3.8, 41.9) * mm});
            skPoint(sketch, "E28.2.1.60", {"position": v(-26.67, 72.4) * mm});
            skPoint(sketch, "E28.2.1.61", {"position": v(-3.8, 57.15) * mm});
            skPoint(sketch, "E28.2.1.62", {"position": v(-11.43, 72.4) * mm});
            skPoint(sketch, "E28.2.1.63", {"position": v(-3.8, 49.53) * mm});
            skPoint(sketch, "E28.2.1.64", {"position": v(-26.67, 41.9) * mm});
            skPoint(sketch, "E28.2.1.65", {"position": v(-19.05, 60.96) * mm});
            skPoint(sketch, "E28.2.1.66", {"position": v(-26.67, 49.53) * mm});
            skPoint(sketch, "E28.2.1.67", {"position": v(-3.8, 64.77) * mm});
            skPoint(sketch, "E28.2.1.68", {"position": v(-34.29, 72.4) * mm});
            skPoint(sketch, "E28.2.1.69", {"position": v(-19.05, 64.77) * mm});
            skPoint(sketch, "E28.2.1.70", {"position": v(-19.05, 41.9) * mm});
            skLineSegment(sketch, "E28.2.1.71", {"start": v(-10.89, 57.7) * mm, "end": v(-10.89, 56.6) * mm});
            skPoint(sketch, "E28.2.1.72", {"position": v(-34.29, 72.4) * mm});
            skLineSegment(sketch, "E28.2.1.73", {"start": v(-10.89, 56.6) * mm, "end": v(-11.97, 56.6) * mm});
            skLineSegment(sketch, "E28.2.1.74", {"start": v(-3.27, 41.37) * mm, "end": v(-4.35, 41.37) * mm});
            skLineSegment(sketch, "E28.2.1.75", {"start": v(-19.6, 42.45) * mm, "end": v(-19.6, 41.37) * mm});
            skLineSegment(sketch, "E28.2.1.76", {"start": v(-18.5, 50.07) * mm, "end": v(-18.5, 48.99) * mm});
            skLineSegment(sketch, "E28.2.1.77", {"start": v(-26.13, 41.37) * mm, "end": v(-27.21, 41.37) * mm});
            skLineSegment(sketch, "E28.2.1.78", {"start": v(-27.21, 57.7) * mm, "end": v(-27.21, 56.6) * mm});
            skLineSegment(sketch, "E28.2.1.79", {"start": v(-27.21, 42.45) * mm, "end": v(-27.21, 41.37) * mm});
            skLineSegment(sketch, "E28.2.1.80", {"start": v(-26.13, 71.85) * mm, "end": v(-27.21, 71.85) * mm});
            skLineSegment(sketch, "E28.2.1.81", {"start": v(-26.13, 72.93) * mm, "end": v(-27.21, 72.93) * mm});
            skLineSegment(sketch, "E28.2.1.82", {"start": v(-34.83, 50.07) * mm, "end": v(-34.83, 48.99) * mm});
            skLineSegment(sketch, "E28.2.1.83", {"start": v(-3.27, 65.31) * mm, "end": v(-4.35, 65.31) * mm});
            skLineSegment(sketch, "E28.2.1.84", {"start": v(-26.13, 57.7) * mm, "end": v(-26.13, 56.6) * mm});
            skLineSegment(sketch, "E28.2.1.85", {"start": v(-10.89, 50.07) * mm, "end": v(-11.97, 50.07) * mm});
            skLineSegment(sketch, "E28.2.1.86", {"start": v(-18.5, 64.23) * mm, "end": v(-19.6, 64.23) * mm});
            skLineSegment(sketch, "E28.2.1.87", {"start": v(-10.89, 64.23) * mm, "end": v(-11.97, 64.23) * mm});
            skLineSegment(sketch, "E28.2.1.88", {"start": v(-33.75, 50.07) * mm, "end": v(-34.83, 50.07) * mm});
            skLineSegment(sketch, "E28.2.1.89", {"start": v(-26.13, 50.07) * mm, "end": v(-27.21, 50.07) * mm});
            skLineSegment(sketch, "E28.2.1.90", {"start": v(-33.75, 41.37) * mm, "end": v(-34.83, 41.37) * mm});
            skLineSegment(sketch, "E28.2.1.91", {"start": v(-33.75, 64.23) * mm, "end": v(-34.83, 64.23) * mm});
            skLineSegment(sketch, "E28.2.1.92", {"start": v(-27.21, 50.07) * mm, "end": v(-27.21, 48.99) * mm});
            skLineSegment(sketch, "E28.2.1.93", {"start": v(-18.5, 41.37) * mm, "end": v(-19.6, 41.37) * mm});
            skLineSegment(sketch, "E28.2.1.94", {"start": v(-33.75, 56.6) * mm, "end": v(-34.83, 56.6) * mm});
            skLineSegment(sketch, "E28.2.1.95", {"start": v(-19.6, 65.31) * mm, "end": v(-19.6, 64.23) * mm});
            skLineSegment(sketch, "E28.2.1.96", {"start": v(-10.89, 57.7) * mm, "end": v(-11.97, 57.7) * mm});
            skLineSegment(sketch, "E28.2.1.97", {"start": v(-11.97, 42.45) * mm, "end": v(-11.97, 41.37) * mm});
            skLineSegment(sketch, "E28.2.1.98", {"start": v(-3.27, 65.31) * mm, "end": v(-3.27, 64.23) * mm});
            skLineSegment(sketch, "E28.2.1.99", {"start": v(-33.75, 42.45) * mm, "end": v(-33.75, 41.37) * mm});
            skLineSegment(sketch, "E28.2.1.100", {"start": v(-34.83, 57.7) * mm, "end": v(-34.83, 56.6) * mm});
            skLineSegment(sketch, "E28.2.1.101", {"start": v(-33.75, 65.31) * mm, "end": v(-34.83, 65.31) * mm});
            skLineSegment(sketch, "E28.2.1.102", {"start": v(-3.27, 50.07) * mm, "end": v(-3.27, 48.99) * mm});
            skLineSegment(sketch, "E28.2.1.103", {"start": v(-26.13, 42.45) * mm, "end": v(-27.21, 42.45) * mm});
            skLineSegment(sketch, "E28.2.1.104", {"start": v(-3.27, 56.6) * mm, "end": v(-4.35, 56.6) * mm});
            skLineSegment(sketch, "E28.2.1.105", {"start": v(-10.89, 72.93) * mm, "end": v(-10.89, 71.85) * mm});
            skLineSegment(sketch, "E28.2.1.106", {"start": v(-10.89, 42.45) * mm, "end": v(-10.89, 41.37) * mm});
            skLineSegment(sketch, "E28.2.1.107", {"start": v(-27.21, 65.31) * mm, "end": v(-27.21, 64.23) * mm});
            skLineSegment(sketch, "E28.2.1.108", {"start": v(-18.5, 48.99) * mm, "end": v(-19.6, 48.99) * mm});
            skLineSegment(sketch, "E28.2.1.109", {"start": v(-26.13, 65.31) * mm, "end": v(-26.13, 64.23) * mm});
            skLineSegment(sketch, "E28.2.1.110", {"start": v(-4.35, 57.7) * mm, "end": v(-4.35, 56.6) * mm});
            skLineSegment(sketch, "E28.2.1.111", {"start": v(-10.89, 41.37) * mm, "end": v(-11.97, 41.37) * mm});
            skLineSegment(sketch, "E28.2.1.112", {"start": v(-26.13, 72.93) * mm, "end": v(-26.13, 71.85) * mm});
            skLineSegment(sketch, "E28.2.1.113", {"start": v(-18.5, 42.45) * mm, "end": v(-18.5, 41.37) * mm});
            skLineSegment(sketch, "E28.2.1.114", {"start": v(-26.13, 57.7) * mm, "end": v(-27.21, 57.7) * mm});
            skLineSegment(sketch, "E28.2.1.115", {"start": v(-26.13, 56.6) * mm, "end": v(-27.21, 56.6) * mm});
            skLineSegment(sketch, "E28.2.1.116", {"start": v(-10.89, 42.45) * mm, "end": v(-11.97, 42.45) * mm});
            skLineSegment(sketch, "E28.2.1.117", {"start": v(-26.13, 42.45) * mm, "end": v(-26.13, 41.37) * mm});
            skLineSegment(sketch, "E28.2.1.118", {"start": v(-3.27, 57.7) * mm, "end": v(-4.35, 57.7) * mm});
            skLineSegment(sketch, "E28.2.1.119", {"start": v(-11.97, 65.31) * mm, "end": v(-11.97, 64.23) * mm});
            skLineSegment(sketch, "E28.2.1.120", {"start": v(-33.75, 48.99) * mm, "end": v(-34.83, 48.99) * mm});
            skLineSegment(sketch, "E28.2.1.121", {"start": v(-3.27, 50.07) * mm, "end": v(-4.35, 50.07) * mm});
            skLineSegment(sketch, "E28.2.1.122", {"start": v(-34.83, 42.45) * mm, "end": v(-34.83, 41.37) * mm});
            skLineSegment(sketch, "E28.2.1.123", {"start": v(-18.5, 72.93) * mm, "end": v(-18.5, 71.85) * mm});
            skLineSegment(sketch, "E28.2.1.124", {"start": v(-18.5, 65.31) * mm, "end": v(-18.5, 64.23) * mm});
            skLineSegment(sketch, "E28.2.1.125", {"start": v(-3.27, 71.85) * mm, "end": v(-4.35, 71.85) * mm});
            skLineSegment(sketch, "E28.2.1.126", {"start": v(-4.35, 65.31) * mm, "end": v(-4.35, 64.23) * mm});
            skLineSegment(sketch, "E28.2.1.127", {"start": v(-10.89, 72.93) * mm, "end": v(-11.97, 72.93) * mm});
            skLineSegment(sketch, "E28.2.1.128", {"start": v(-19.6, 50.07) * mm, "end": v(-19.6, 48.99) * mm});
            skLineSegment(sketch, "E28.2.1.129", {"start": v(-18.5, 71.85) * mm, "end": v(-19.6, 71.85) * mm});
            skLineSegment(sketch, "E28.2.1.130", {"start": v(-10.89, 71.85) * mm, "end": v(-11.97, 71.85) * mm});
            skLineSegment(sketch, "E28.2.1.131", {"start": v(-27.21, 72.93) * mm, "end": v(-27.21, 71.85) * mm});
            skLineSegment(sketch, "E28.2.1.132", {"start": v(-33.75, 65.31) * mm, "end": v(-33.75, 64.23) * mm});
            skLineSegment(sketch, "E28.2.1.133", {"start": v(-3.27, 72.93) * mm, "end": v(-4.35, 72.93) * mm});
            skLineSegment(sketch, "E28.2.1.134", {"start": v(-18.5, 42.45) * mm, "end": v(-19.6, 42.45) * mm});
            skLineSegment(sketch, "E28.2.1.135", {"start": v(-10.89, 65.31) * mm, "end": v(-11.97, 65.31) * mm});
            skLineSegment(sketch, "E28.2.1.136", {"start": v(-18.5, 72.93) * mm, "end": v(-19.6, 72.93) * mm});
            skLineSegment(sketch, "E28.2.1.137", {"start": v(-26.13, 50.07) * mm, "end": v(-26.13, 48.99) * mm});
            skLineSegment(sketch, "E28.2.1.138", {"start": v(-18.5, 65.31) * mm, "end": v(-19.6, 65.31) * mm});
            skLineSegment(sketch, "E28.2.1.139", {"start": v(-3.27, 42.45) * mm, "end": v(-4.35, 42.45) * mm});
            skLineSegment(sketch, "E28.2.1.140", {"start": v(-10.89, 65.31) * mm, "end": v(-10.89, 64.23) * mm});
            skLineSegment(sketch, "E28.2.1.141", {"start": v(-4.35, 72.93) * mm, "end": v(-4.35, 71.85) * mm});
            skLineSegment(sketch, "E28.2.1.142", {"start": v(-4.35, 50.07) * mm, "end": v(-4.35, 48.99) * mm});
            skLineSegment(sketch, "E28.2.1.143", {"start": v(-4.35, 42.45) * mm, "end": v(-4.35, 41.37) * mm});
            skLineSegment(sketch, "E28.2.1.144", {"start": v(-26.13, 64.23) * mm, "end": v(-27.21, 64.23) * mm});
            skLineSegment(sketch, "E28.2.1.145", {"start": v(-3.27, 72.93) * mm, "end": v(-3.27, 71.85) * mm});
            skLineSegment(sketch, "E28.2.1.146", {"start": v(-11.97, 72.93) * mm, "end": v(-11.97, 71.85) * mm});
            skLineSegment(sketch, "E28.2.1.147", {"start": v(-3.27, 42.45) * mm, "end": v(-3.27, 41.37) * mm});
            skLineSegment(sketch, "E28.2.1.148", {"start": v(-19.6, 72.93) * mm, "end": v(-19.6, 71.85) * mm});
            skLineSegment(sketch, "E28.2.1.149", {"start": v(-3.27, 48.99) * mm, "end": v(-4.35, 48.99) * mm});
            skLineSegment(sketch, "E28.2.1.150", {"start": v(-18.5, 50.07) * mm, "end": v(-19.6, 50.07) * mm});
            skLineSegment(sketch, "E28.2.1.151", {"start": v(-3.27, 57.7) * mm, "end": v(-3.27, 56.6) * mm});
            skLineSegment(sketch, "E28.2.1.152", {"start": v(-10.89, 48.99) * mm, "end": v(-11.97, 48.99) * mm});
            skLineSegment(sketch, "E28.2.1.153", {"start": v(-10.89, 50.07) * mm, "end": v(-10.89, 48.99) * mm});
            skLineSegment(sketch, "E28.2.1.154", {"start": v(-3.27, 64.23) * mm, "end": v(-4.35, 64.23) * mm});
            skLineSegment(sketch, "E28.2.1.155", {"start": v(-26.13, 65.31) * mm, "end": v(-27.21, 65.31) * mm});
            skLineSegment(sketch, "E28.2.1.156", {"start": v(-33.75, 42.45) * mm, "end": v(-34.83, 42.45) * mm});
            skLineSegment(sketch, "E28.2.1.157", {"start": v(-33.75, 57.7) * mm, "end": v(-34.83, 57.7) * mm});
            skLineSegment(sketch, "E28.2.1.158", {"start": v(-26.13, 48.99) * mm, "end": v(-27.21, 48.99) * mm});
            skLineSegment(sketch, "E28.2.1.159", {"start": v(-33.75, 72.93) * mm, "end": v(-34.83, 72.93) * mm});
            skLineSegment(sketch, "E28.2.1.160", {"start": v(-11.97, 50.07) * mm, "end": v(-11.97, 48.99) * mm});
            skLineSegment(sketch, "E28.2.1.161", {"start": v(-33.75, 71.85) * mm, "end": v(-34.83, 71.85) * mm});
            skLineSegment(sketch, "E28.2.1.162", {"start": v(-33.75, 72.93) * mm, "end": v(-33.75, 71.85) * mm});
            skLineSegment(sketch, "E28.2.1.163", {"start": v(-34.83, 65.31) * mm, "end": v(-34.83, 64.23) * mm});
            skLineSegment(sketch, "E28.2.1.164", {"start": v(-11.97, 57.7) * mm, "end": v(-11.97, 56.6) * mm});
            skLineSegment(sketch, "E28.2.1.165", {"start": v(-33.75, 57.7) * mm, "end": v(-33.75, 56.6) * mm});
            skLineSegment(sketch, "E28.2.1.166", {"start": v(-33.75, 50.07) * mm, "end": v(-33.75, 48.99) * mm});
            skLineSegment(sketch, "E28.2.1.167", {"start": v(-34.83, 72.93) * mm, "end": v(-34.83, 71.85) * mm});
            skPoint(sketch, "E28.2.2.1", {"position": v(-26.67, 3.8) * mm});
            skPoint(sketch, "E28.2.2.2", {"position": v(-11.43, 11.43) * mm});
            skPoint(sketch, "E28.2.2.3", {"position": v(-3.8, 26.67) * mm});
            skPoint(sketch, "E28.2.2.5", {"position": v(-34.29, 26.67) * mm});
            skPoint(sketch, "E28.2.2.6", {"position": v(-3.8, 11.43) * mm});
            skPoint(sketch, "E28.2.2.7", {"position": v(-3.8, 19.05) * mm});
            skPoint(sketch, "E28.2.2.8", {"position": v(-19.05, 26.67) * mm});
            skPoint(sketch, "E28.2.2.11", {"position": v(-30.48, 34.3) * mm});
            skPoint(sketch, "E28.2.2.13", {"position": v(-26.67, 11.43) * mm});
            skPoint(sketch, "E28.2.2.14", {"position": v(-19.05, 22.86) * mm});
            skPoint(sketch, "E28.2.2.16", {"position": v(-34.29, 3.8) * mm});
            skPoint(sketch, "E28.2.2.21", {"position": v(-26.67, 19.05) * mm});
            skPoint(sketch, "E28.2.2.22", {"position": v(-11.43, 19.05) * mm});
            skPoint(sketch, "E28.2.2.23", {"position": v(-3.8, 3.8) * mm});
            skPoint(sketch, "E28.2.2.24", {"position": v(-22.86, 7.62) * mm});
            skPoint(sketch, "E28.2.2.26", {"position": v(-19.05, 3.8) * mm});
            skPoint(sketch, "E28.2.2.27", {"position": v(-26.67, 26.67) * mm});
            skPoint(sketch, "E28.2.2.29", {"position": v(-11.43, 26.67) * mm});
            skPoint(sketch, "E28.2.2.30", {"position": v(-19.05, 34.3) * mm});
            skPoint(sketch, "E28.2.2.31", {"position": v(-11.43, 3.8) * mm});
            skPoint(sketch, "E28.2.2.32", {"position": v(-3.8, 34.3) * mm});
            skPoint(sketch, "E28.2.2.33", {"position": v(-19.05, 11.43) * mm});
            skPoint(sketch, "E28.2.2.34", {"position": v(-34.29, 11.43) * mm});
            skPoint(sketch, "E28.2.2.36", {"position": v(-26.67, 34.3) * mm});
            skPoint(sketch, "E28.2.2.39", {"position": v(-34.29, 19.05) * mm});
            skPoint(sketch, "E28.2.2.40", {"position": v(-15.24, 19.05) * mm});
            skPoint(sketch, "E28.2.2.42", {"position": v(-7.62, 30.48) * mm});
            skPoint(sketch, "E28.2.2.44", {"position": v(-11.43, 34.3) * mm});
            skPoint(sketch, "E28.2.2.45", {"position": v(-3.8, 34.3) * mm});
            skPoint(sketch, "E28.2.2.46", {"position": v(-34.29, 19.05) * mm});
            skPoint(sketch, "E28.2.2.47", {"position": v(-11.43, 3.8) * mm});
            skPoint(sketch, "E28.2.2.48", {"position": v(-11.43, 11.43) * mm});
            skPoint(sketch, "E28.2.2.49", {"position": v(-15.24, 19.05) * mm});
            skPoint(sketch, "E28.2.2.50", {"position": v(-34.29, 3.8) * mm});
            skPoint(sketch, "E28.2.2.51", {"position": v(-34.29, 11.43) * mm});
            skPoint(sketch, "E28.2.2.52", {"position": v(-19.05, 11.43) * mm});
            skPoint(sketch, "E28.2.2.53", {"position": v(-26.67, 26.67) * mm});
            skPoint(sketch, "E28.2.2.54", {"position": v(-19.05, 34.3) * mm});
            skPoint(sketch, "E28.2.2.55", {"position": v(-26.67, 19.05) * mm});
            skPoint(sketch, "E28.2.2.56", {"position": v(-34.29, 26.67) * mm});
            skPoint(sketch, "E28.2.2.57", {"position": v(-11.43, 19.05) * mm});
            skPoint(sketch, "E28.2.2.58", {"position": v(-11.43, 26.67) * mm});
            skPoint(sketch, "E28.2.2.59", {"position": v(-3.8, 3.8) * mm});
            skPoint(sketch, "E28.2.2.60", {"position": v(-26.67, 34.3) * mm});
            skPoint(sketch, "E28.2.2.61", {"position": v(-3.8, 19.05) * mm});
            skPoint(sketch, "E28.2.2.62", {"position": v(-11.43, 34.3) * mm});
            skPoint(sketch, "E28.2.2.63", {"position": v(-3.8, 11.43) * mm});
            skPoint(sketch, "E28.2.2.64", {"position": v(-26.67, 3.8) * mm});
            skPoint(sketch, "E28.2.2.65", {"position": v(-19.05, 22.86) * mm});
            skPoint(sketch, "E28.2.2.66", {"position": v(-26.67, 11.43) * mm});
            skPoint(sketch, "E28.2.2.67", {"position": v(-3.8, 26.67) * mm});
            skPoint(sketch, "E28.2.2.68", {"position": v(-34.29, 34.3) * mm});
            skPoint(sketch, "E28.2.2.69", {"position": v(-19.05, 26.67) * mm});
            skPoint(sketch, "E28.2.2.70", {"position": v(-19.05, 3.8) * mm});
            skLineSegment(sketch, "E28.2.2.71", {"start": v(-10.89, 19.6) * mm, "end": v(-10.89, 18.5) * mm});
            skPoint(sketch, "E28.2.2.72", {"position": v(-34.29, 34.3) * mm});
            skLineSegment(sketch, "E28.2.2.73", {"start": v(-10.89, 18.5) * mm, "end": v(-11.97, 18.5) * mm});
            skLineSegment(sketch, "E28.2.2.74", {"start": v(-3.27, 3.27) * mm, "end": v(-4.35, 3.27) * mm});
            skLineSegment(sketch, "E28.2.2.75", {"start": v(-19.6, 4.35) * mm, "end": v(-19.6, 3.27) * mm});
            skLineSegment(sketch, "E28.2.2.76", {"start": v(-18.5, 11.97) * mm, "end": v(-18.5, 10.89) * mm});
            skLineSegment(sketch, "E28.2.2.77", {"start": v(-26.13, 3.27) * mm, "end": v(-27.21, 3.27) * mm});
            skLineSegment(sketch, "E28.2.2.78", {"start": v(-27.21, 19.6) * mm, "end": v(-27.21, 18.5) * mm});
            skLineSegment(sketch, "E28.2.2.79", {"start": v(-27.21, 4.35) * mm, "end": v(-27.21, 3.27) * mm});
            skLineSegment(sketch, "E28.2.2.80", {"start": v(-26.13, 33.75) * mm, "end": v(-27.21, 33.75) * mm});
            skLineSegment(sketch, "E28.2.2.81", {"start": v(-26.13, 34.83) * mm, "end": v(-27.21, 34.83) * mm});
            skLineSegment(sketch, "E28.2.2.82", {"start": v(-34.83, 11.97) * mm, "end": v(-34.83, 10.89) * mm});
            skLineSegment(sketch, "E28.2.2.83", {"start": v(-3.27, 27.21) * mm, "end": v(-4.35, 27.21) * mm});
            skLineSegment(sketch, "E28.2.2.84", {"start": v(-26.13, 19.6) * mm, "end": v(-26.13, 18.5) * mm});
            skLineSegment(sketch, "E28.2.2.85", {"start": v(-10.89, 11.97) * mm, "end": v(-11.97, 11.97) * mm});
            skLineSegment(sketch, "E28.2.2.86", {"start": v(-18.5, 26.13) * mm, "end": v(-19.6, 26.13) * mm});
            skLineSegment(sketch, "E28.2.2.87", {"start": v(-10.89, 26.13) * mm, "end": v(-11.97, 26.13) * mm});
            skLineSegment(sketch, "E28.2.2.88", {"start": v(-33.75, 11.97) * mm, "end": v(-34.83, 11.97) * mm});
            skLineSegment(sketch, "E28.2.2.89", {"start": v(-26.13, 11.97) * mm, "end": v(-27.21, 11.97) * mm});
            skLineSegment(sketch, "E28.2.2.90", {"start": v(-33.75, 3.27) * mm, "end": v(-34.83, 3.27) * mm});
            skLineSegment(sketch, "E28.2.2.91", {"start": v(-33.75, 26.13) * mm, "end": v(-34.83, 26.13) * mm});
            skLineSegment(sketch, "E28.2.2.92", {"start": v(-27.21, 11.97) * mm, "end": v(-27.21, 10.89) * mm});
            skLineSegment(sketch, "E28.2.2.93", {"start": v(-18.5, 3.27) * mm, "end": v(-19.6, 3.27) * mm});
            skLineSegment(sketch, "E28.2.2.94", {"start": v(-33.75, 18.5) * mm, "end": v(-34.83, 18.5) * mm});
            skLineSegment(sketch, "E28.2.2.95", {"start": v(-19.6, 27.21) * mm, "end": v(-19.6, 26.13) * mm});
            skLineSegment(sketch, "E28.2.2.96", {"start": v(-10.89, 19.6) * mm, "end": v(-11.97, 19.6) * mm});
            skLineSegment(sketch, "E28.2.2.97", {"start": v(-11.97, 4.35) * mm, "end": v(-11.97, 3.27) * mm});
            skLineSegment(sketch, "E28.2.2.98", {"start": v(-3.27, 27.21) * mm, "end": v(-3.27, 26.13) * mm});
            skLineSegment(sketch, "E28.2.2.99", {"start": v(-33.75, 4.35) * mm, "end": v(-33.75, 3.27) * mm});
            skLineSegment(sketch, "E28.2.2.100", {"start": v(-34.83, 19.6) * mm, "end": v(-34.83, 18.5) * mm});
            skLineSegment(sketch, "E28.2.2.101", {"start": v(-33.75, 27.21) * mm, "end": v(-34.83, 27.21) * mm});
            skLineSegment(sketch, "E28.2.2.102", {"start": v(-3.27, 11.97) * mm, "end": v(-3.27, 10.89) * mm});
            skLineSegment(sketch, "E28.2.2.103", {"start": v(-26.13, 4.35) * mm, "end": v(-27.21, 4.35) * mm});
            skLineSegment(sketch, "E28.2.2.104", {"start": v(-3.27, 18.5) * mm, "end": v(-4.35, 18.5) * mm});
            skLineSegment(sketch, "E28.2.2.105", {"start": v(-10.89, 34.83) * mm, "end": v(-10.89, 33.75) * mm});
            skLineSegment(sketch, "E28.2.2.106", {"start": v(-10.89, 4.35) * mm, "end": v(-10.89, 3.27) * mm});
            skLineSegment(sketch, "E28.2.2.107", {"start": v(-27.21, 27.21) * mm, "end": v(-27.21, 26.13) * mm});
            skLineSegment(sketch, "E28.2.2.108", {"start": v(-18.5, 10.89) * mm, "end": v(-19.6, 10.89) * mm});
            skLineSegment(sketch, "E28.2.2.109", {"start": v(-26.13, 27.21) * mm, "end": v(-26.13, 26.13) * mm});
            skLineSegment(sketch, "E28.2.2.110", {"start": v(-4.35, 19.6) * mm, "end": v(-4.35, 18.5) * mm});
            skLineSegment(sketch, "E28.2.2.111", {"start": v(-10.89, 3.27) * mm, "end": v(-11.97, 3.27) * mm});
            skLineSegment(sketch, "E28.2.2.112", {"start": v(-26.13, 34.83) * mm, "end": v(-26.13, 33.75) * mm});
            skLineSegment(sketch, "E28.2.2.113", {"start": v(-18.5, 4.35) * mm, "end": v(-18.5, 3.27) * mm});
            skLineSegment(sketch, "E28.2.2.114", {"start": v(-26.13, 19.6) * mm, "end": v(-27.21, 19.6) * mm});
            skLineSegment(sketch, "E28.2.2.115", {"start": v(-26.13, 18.5) * mm, "end": v(-27.21, 18.5) * mm});
            skLineSegment(sketch, "E28.2.2.116", {"start": v(-10.89, 4.35) * mm, "end": v(-11.97, 4.35) * mm});
            skLineSegment(sketch, "E28.2.2.117", {"start": v(-26.13, 4.35) * mm, "end": v(-26.13, 3.27) * mm});
            skLineSegment(sketch, "E28.2.2.118", {"start": v(-3.27, 19.6) * mm, "end": v(-4.35, 19.6) * mm});
            skLineSegment(sketch, "E28.2.2.119", {"start": v(-11.97, 27.21) * mm, "end": v(-11.97, 26.13) * mm});
            skLineSegment(sketch, "E28.2.2.120", {"start": v(-33.75, 10.89) * mm, "end": v(-34.83, 10.89) * mm});
            skLineSegment(sketch, "E28.2.2.121", {"start": v(-3.27, 11.97) * mm, "end": v(-4.35, 11.97) * mm});
            skLineSegment(sketch, "E28.2.2.122", {"start": v(-34.83, 4.35) * mm, "end": v(-34.83, 3.27) * mm});
            skLineSegment(sketch, "E28.2.2.123", {"start": v(-18.5, 34.83) * mm, "end": v(-18.5, 33.75) * mm});
            skLineSegment(sketch, "E28.2.2.124", {"start": v(-18.5, 27.21) * mm, "end": v(-18.5, 26.13) * mm});
            skLineSegment(sketch, "E28.2.2.125", {"start": v(-3.27, 33.75) * mm, "end": v(-4.35, 33.75) * mm});
            skLineSegment(sketch, "E28.2.2.126", {"start": v(-4.35, 27.21) * mm, "end": v(-4.35, 26.13) * mm});
            skLineSegment(sketch, "E28.2.2.127", {"start": v(-10.89, 34.83) * mm, "end": v(-11.97, 34.83) * mm});
            skLineSegment(sketch, "E28.2.2.128", {"start": v(-19.6, 11.97) * mm, "end": v(-19.6, 10.89) * mm});
            skLineSegment(sketch, "E28.2.2.129", {"start": v(-18.5, 33.75) * mm, "end": v(-19.6, 33.75) * mm});
            skLineSegment(sketch, "E28.2.2.130", {"start": v(-10.89, 33.75) * mm, "end": v(-11.97, 33.75) * mm});
            skLineSegment(sketch, "E28.2.2.131", {"start": v(-27.21, 34.83) * mm, "end": v(-27.21, 33.75) * mm});
            skLineSegment(sketch, "E28.2.2.132", {"start": v(-33.75, 27.21) * mm, "end": v(-33.75, 26.13) * mm});
            skLineSegment(sketch, "E28.2.2.133", {"start": v(-3.27, 34.83) * mm, "end": v(-4.35, 34.83) * mm});
            skLineSegment(sketch, "E28.2.2.134", {"start": v(-18.5, 4.35) * mm, "end": v(-19.6, 4.35) * mm});
            skLineSegment(sketch, "E28.2.2.135", {"start": v(-10.89, 27.21) * mm, "end": v(-11.97, 27.21) * mm});
            skLineSegment(sketch, "E28.2.2.136", {"start": v(-18.5, 34.83) * mm, "end": v(-19.6, 34.83) * mm});
            skLineSegment(sketch, "E28.2.2.137", {"start": v(-26.13, 11.97) * mm, "end": v(-26.13, 10.89) * mm});
            skLineSegment(sketch, "E28.2.2.138", {"start": v(-18.5, 27.21) * mm, "end": v(-19.6, 27.21) * mm});
            skLineSegment(sketch, "E28.2.2.139", {"start": v(-3.27, 4.35) * mm, "end": v(-4.35, 4.35) * mm});
            skLineSegment(sketch, "E28.2.2.140", {"start": v(-10.89, 27.21) * mm, "end": v(-10.89, 26.13) * mm});
            skLineSegment(sketch, "E28.2.2.141", {"start": v(-4.35, 34.83) * mm, "end": v(-4.35, 33.75) * mm});
            skLineSegment(sketch, "E28.2.2.142", {"start": v(-4.35, 11.97) * mm, "end": v(-4.35, 10.89) * mm});
            skLineSegment(sketch, "E28.2.2.143", {"start": v(-4.35, 4.35) * mm, "end": v(-4.35, 3.27) * mm});
            skLineSegment(sketch, "E28.2.2.144", {"start": v(-26.13, 26.13) * mm, "end": v(-27.21, 26.13) * mm});
            skLineSegment(sketch, "E28.2.2.145", {"start": v(-3.27, 34.83) * mm, "end": v(-3.27, 33.75) * mm});
            skLineSegment(sketch, "E28.2.2.146", {"start": v(-11.97, 34.83) * mm, "end": v(-11.97, 33.75) * mm});
            skLineSegment(sketch, "E28.2.2.147", {"start": v(-3.27, 4.35) * mm, "end": v(-3.27, 3.27) * mm});
            skLineSegment(sketch, "E28.2.2.148", {"start": v(-19.6, 34.83) * mm, "end": v(-19.6, 33.75) * mm});
            skLineSegment(sketch, "E28.2.2.149", {"start": v(-3.27, 10.89) * mm, "end": v(-4.35, 10.89) * mm});
            skLineSegment(sketch, "E28.2.2.150", {"start": v(-18.5, 11.97) * mm, "end": v(-19.6, 11.97) * mm});
            skLineSegment(sketch, "E28.2.2.151", {"start": v(-3.27, 19.6) * mm, "end": v(-3.27, 18.5) * mm});
            skLineSegment(sketch, "E28.2.2.152", {"start": v(-10.89, 10.89) * mm, "end": v(-11.97, 10.89) * mm});
            skLineSegment(sketch, "E28.2.2.153", {"start": v(-10.89, 11.97) * mm, "end": v(-10.89, 10.89) * mm});
            skLineSegment(sketch, "E28.2.2.154", {"start": v(-3.27, 26.13) * mm, "end": v(-4.35, 26.13) * mm});
            skLineSegment(sketch, "E28.2.2.155", {"start": v(-26.13, 27.21) * mm, "end": v(-27.21, 27.21) * mm});
            skLineSegment(sketch, "E28.2.2.156", {"start": v(-33.75, 4.35) * mm, "end": v(-34.83, 4.35) * mm});
            skLineSegment(sketch, "E28.2.2.157", {"start": v(-33.75, 19.6) * mm, "end": v(-34.83, 19.6) * mm});
            skLineSegment(sketch, "E28.2.2.158", {"start": v(-26.13, 10.89) * mm, "end": v(-27.21, 10.89) * mm});
            skLineSegment(sketch, "E28.2.2.159", {"start": v(-33.75, 34.83) * mm, "end": v(-34.83, 34.83) * mm});
            skLineSegment(sketch, "E28.2.2.160", {"start": v(-11.97, 11.97) * mm, "end": v(-11.97, 10.89) * mm});
            skLineSegment(sketch, "E28.2.2.161", {"start": v(-33.75, 33.75) * mm, "end": v(-34.83, 33.75) * mm});
            skLineSegment(sketch, "E28.2.2.162", {"start": v(-33.75, 34.83) * mm, "end": v(-33.75, 33.75) * mm});
            skLineSegment(sketch, "E28.2.2.163", {"start": v(-34.83, 27.21) * mm, "end": v(-34.83, 26.13) * mm});
            skLineSegment(sketch, "E28.2.2.164", {"start": v(-11.97, 19.6) * mm, "end": v(-11.97, 18.5) * mm});
            skLineSegment(sketch, "E28.2.2.165", {"start": v(-33.75, 19.6) * mm, "end": v(-33.75, 18.5) * mm});
            skLineSegment(sketch, "E28.2.2.166", {"start": v(-33.75, 11.97) * mm, "end": v(-33.75, 10.89) * mm});
            skLineSegment(sketch, "E28.2.2.167", {"start": v(-34.83, 34.83) * mm, "end": v(-34.83, 33.75) * mm});
            skSolve(sketch);
        }
        {
            var Q0;
            Q0=makeQuery(id+"F4.imprint","IMPRINT",FACE,{"disambiguationData":[TD([[makeQuery(id+"F4.imprint","IMPRINT",EDGE,{"derivedFrom":sQuery(id+"F4.wireOp",EDGE,"E28.0.1.82")}),1.0]])]});
            var Q1;
            Q1=makeQuery(id+"F4.imprint","IMPRINT",FACE,{"disambiguationData":[TD([[makeQuery(id+"F4.imprint","IMPRINT",EDGE,{"derivedFrom":sQuery(id+"F4.wireOp",EDGE,"E28.0.1.90")}),-1.0]])]});
            var Q2;
            Q2=makeQuery(id+"F4.imprint","IMPRINT",FACE,{"disambiguationData":[TD([[makeQuery(id+"F4.imprint","IMPRINT",EDGE,{"derivedFrom":sQuery(id+"F4.wireOp",EDGE,"E28.0.1.91")}),-1.0]])]});
            var Q3;
            Q3=makeQuery(id+"F4.imprint","IMPRINT",FACE,{"disambiguationData":[TD([[makeQuery(id+"F4.imprint","IMPRINT",EDGE,{"derivedFrom":sQuery(id+"F4.wireOp",EDGE,"E28.0.1.94")}),-1.0]])]});
            var Q4;
            Q4=makeQuery(id+"F4.imprint","IMPRINT",FACE,{"disambiguationData":[TD([[makeQuery(id+"F4.imprint","IMPRINT",EDGE,{"derivedFrom":sQuery(id+"F4.wireOp",EDGE,"E28.0.1.159")}),1.0]])]});
            var Q5;
            Q5=makeQuery(id+"F4.imprint","IMPRINT",FACE,{"disambiguationData":[TD([[makeQuery(id+"F4.imprint","IMPRINT",EDGE,{"derivedFrom":sQuery(id+"F4.wireOp",EDGE,"E28.0.2.74")}),-1.0]])]});
            var Q6;
            Q6=makeQuery(id+"F4.imprint","IMPRINT",FACE,{"disambiguationData":[TD([[makeQuery(id+"F4.imprint","IMPRINT",EDGE,{"derivedFrom":sQuery(id+"F4.wireOp",EDGE,"E28.0.2.75")}),1.0]])]});
            var Q7;
            Q7=makeQuery(id+"F4.imprint","IMPRINT",FACE,{"disambiguationData":[TD([[makeQuery(id+"F4.imprint","IMPRINT",EDGE,{"derivedFrom":sQuery(id+"F4.wireOp",EDGE,"E28.0.2.77")}),-1.0]])]});
            var Q8;
            Q8=makeQuery(id+"F4.imprint","IMPRINT",FACE,{"disambiguationData":[TD([[makeQuery(id+"F4.imprint","IMPRINT",EDGE,{"derivedFrom":sQuery(id+"F4.wireOp",EDGE,"E28.0.2.82")}),1.0]])]});
            var Q9;
            Q9=makeQuery(id+"F4.imprint","IMPRINT",FACE,{"disambiguationData":[TD([[makeQuery(id+"F4.imprint","IMPRINT",EDGE,{"derivedFrom":sQuery(id+"F4.wireOp",EDGE,"E28.0.2.90")}),-1.0]])]});
            var Q10;
            Q10=makeQuery(id+"F4.imprint","IMPRINT",FACE,{"disambiguationData":[TD([[makeQuery(id+"F4.imprint","IMPRINT",EDGE,{"derivedFrom":sQuery(id+"F4.wireOp",EDGE,"E28.0.2.91")}),-1.0]])]});
            var Q11;
            Q11=makeQuery(id+"F4.imprint","IMPRINT",FACE,{"disambiguationData":[TD([[makeQuery(id+"F4.imprint","IMPRINT",EDGE,{"derivedFrom":sQuery(id+"F4.wireOp",EDGE,"E28.0.2.94")}),-1.0]])]});
            var Q12;
            Q12=makeQuery(id+"F4.imprint","IMPRINT",FACE,{"disambiguationData":[TD([[makeQuery(id+"F4.imprint","IMPRINT",EDGE,{"derivedFrom":sQuery(id+"F4.wireOp",EDGE,"E28.0.2.97")}),1.0]])]});
            var Q13;
            Q13=makeQuery(id+"F4.imprint","IMPRINT",FACE,{"disambiguationData":[TD([[makeQuery(id+"F4.imprint","IMPRINT",EDGE,{"derivedFrom":sQuery(id+"F4.wireOp",EDGE,"E28.0.2.159")}),1.0]])]});
            var Q14;
            Q14=makeQuery(id+"F4.imprint","IMPRINT",FACE,{"disambiguationData":[TD([[makeQuery(id+"F4.imprint","IMPRINT",EDGE,{"derivedFrom":sQuery(id+"F4.wireOp",EDGE,"E28.1.0.80")}),-1.0]])]});
            var Q15;
            Q15=makeQuery(id+"F4.imprint","IMPRINT",FACE,{"disambiguationData":[TD([[makeQuery(id+"F4.imprint","IMPRINT",EDGE,{"derivedFrom":sQuery(id+"F4.wireOp",EDGE,"E28.1.0.105")}),-1.0]])]});
            var Q16;
            Q16=makeQuery(id+"F4.imprint","IMPRINT",FACE,{"disambiguationData":[TD([[makeQuery(id+"F4.imprint","IMPRINT",EDGE,{"derivedFrom":sQuery(id+"F4.wireOp",EDGE,"E28.1.0.123")}),-1.0]])]});
            var Q17;
            Q17=makeQuery(id+"F4.imprint","IMPRINT",FACE,{"disambiguationData":[TD([[makeQuery(id+"F4.imprint","IMPRINT",EDGE,{"derivedFrom":sQuery(id+"F4.wireOp",EDGE,"E28.1.0.125")}),-1.0]])]});
            var Q18;
            Q18=makeQuery(id+"F4.imprint","IMPRINT",FACE,{"disambiguationData":[TD([[makeQuery(id+"F4.imprint","IMPRINT",EDGE,{"derivedFrom":sQuery(id+"F4.wireOp",EDGE,"E28.1.0.159")}),1.0]])]});
            var Q19;
            Q19=makeQuery(id+"F4.imprint","IMPRINT",FACE,{"disambiguationData":[TD([[makeQuery(id+"F4.imprint","IMPRINT",EDGE,{"derivedFrom":sQuery(id+"F4.wireOp",EDGE,"E28.1.2.74")}),-1.0]])]});
            var Q20;
            Q20=makeQuery(id+"F4.imprint","IMPRINT",FACE,{"disambiguationData":[TD([[makeQuery(id+"F4.imprint","IMPRINT",EDGE,{"derivedFrom":sQuery(id+"F4.wireOp",EDGE,"E28.1.2.75")}),1.0]])]});
            var Q21;
            Q21=makeQuery(id+"F4.imprint","IMPRINT",FACE,{"disambiguationData":[TD([[makeQuery(id+"F4.imprint","IMPRINT",EDGE,{"derivedFrom":sQuery(id+"F4.wireOp",EDGE,"E28.1.2.77")}),-1.0]])]});
            var Q22;
            Q22=makeQuery(id+"F4.imprint","IMPRINT",FACE,{"disambiguationData":[TD([[makeQuery(id+"F4.imprint","IMPRINT",EDGE,{"derivedFrom":sQuery(id+"F4.wireOp",EDGE,"E28.1.2.90")}),-1.0]])]});
            var Q23;
            Q23=makeQuery(id+"F4.imprint","IMPRINT",FACE,{"disambiguationData":[TD([[makeQuery(id+"F4.imprint","IMPRINT",EDGE,{"derivedFrom":sQuery(id+"F4.wireOp",EDGE,"E28.1.2.97")}),1.0]])]});
            var Q24;
            Q24=makeQuery(id+"F4.imprint","IMPRINT",FACE,{"disambiguationData":[TD([[makeQuery(id+"F4.imprint","IMPRINT",EDGE,{"derivedFrom":sQuery(id+"F4.wireOp",EDGE,"E28.2.0.74")}),-1.0]])]});
            var Q25;
            Q25=makeQuery(id+"F4.imprint","IMPRINT",FACE,{"disambiguationData":[TD([[makeQuery(id+"F4.imprint","IMPRINT",EDGE,{"derivedFrom":sQuery(id+"F4.wireOp",EDGE,"E28.2.0.80")}),-1.0]])]});
            var Q26;
            Q26=makeQuery(id+"F4.imprint","IMPRINT",FACE,{"disambiguationData":[TD([[makeQuery(id+"F4.imprint","IMPRINT",EDGE,{"derivedFrom":sQuery(id+"F4.wireOp",EDGE,"E28.2.0.83")}),1.0]])]});
            var Q27;
            Q27=makeQuery(id+"F4.imprint","IMPRINT",FACE,{"disambiguationData":[TD([[makeQuery(id+"F4.imprint","IMPRINT",EDGE,{"derivedFrom":sQuery(id+"F4.wireOp",EDGE,"E28.2.0.102")}),-1.0]])]});
            var Q28;
            Q28=makeQuery(id+"F4.imprint","IMPRINT",FACE,{"disambiguationData":[TD([[makeQuery(id+"F4.imprint","IMPRINT",EDGE,{"derivedFrom":sQuery(id+"F4.wireOp",EDGE,"E28.2.0.104")}),-1.0]])]});
            var Q29;
            Q29=makeQuery(id+"F4.imprint","IMPRINT",FACE,{"disambiguationData":[TD([[makeQuery(id+"F4.imprint","IMPRINT",EDGE,{"derivedFrom":sQuery(id+"F4.wireOp",EDGE,"E28.2.0.105")}),-1.0]])]});
            var Q30;
            Q30=makeQuery(id+"F4.imprint","IMPRINT",FACE,{"disambiguationData":[TD([[makeQuery(id+"F4.imprint","IMPRINT",EDGE,{"derivedFrom":sQuery(id+"F4.wireOp",EDGE,"E28.2.0.123")}),-1.0]])]});
            var Q31;
            Q31=makeQuery(id+"F4.imprint","IMPRINT",FACE,{"disambiguationData":[TD([[makeQuery(id+"F4.imprint","IMPRINT",EDGE,{"derivedFrom":sQuery(id+"F4.wireOp",EDGE,"E28.2.0.125")}),-1.0]])]});
            var Q32;
            Q32=makeQuery(id+"F4.imprint","IMPRINT",FACE,{"disambiguationData":[TD([[makeQuery(id+"F4.imprint","IMPRINT",EDGE,{"derivedFrom":sQuery(id+"F4.wireOp",EDGE,"E28.2.0.159")}),1.0]])]});
            var Q33;
            Q33=makeQuery(id+"F4.imprint","IMPRINT",FACE,{"disambiguationData":[TD([[makeQuery(id+"F4.imprint","IMPRINT",EDGE,{"derivedFrom":sQuery(id+"F4.wireOp",EDGE,"E28.2.1.74")}),-1.0]])]});
            var Q34;
            Q34=makeQuery(id+"F4.imprint","IMPRINT",FACE,{"disambiguationData":[TD([[makeQuery(id+"F4.imprint","IMPRINT",EDGE,{"derivedFrom":sQuery(id+"F4.wireOp",EDGE,"E28.2.1.83")}),1.0]])]});
            var Q35;
            Q35=makeQuery(id+"F4.imprint","IMPRINT",FACE,{"disambiguationData":[TD([[makeQuery(id+"F4.imprint","IMPRINT",EDGE,{"derivedFrom":sQuery(id+"F4.wireOp",EDGE,"E28.2.1.102")}),-1.0]])]});
            var Q36;
            Q36=makeQuery(id+"F4.imprint","IMPRINT",FACE,{"disambiguationData":[TD([[makeQuery(id+"F4.imprint","IMPRINT",EDGE,{"derivedFrom":sQuery(id+"F4.wireOp",EDGE,"E28.2.1.104")}),-1.0]])]});
            var Q37;
            Q37=makeQuery(id+"F4.imprint","IMPRINT",FACE,{"disambiguationData":[TD([[makeQuery(id+"F4.imprint","IMPRINT",EDGE,{"derivedFrom":sQuery(id+"F4.wireOp",EDGE,"E28.2.1.125")}),-1.0]])]});
            var Q38;
            Q38=makeQuery(id+"F4.imprint","IMPRINT",FACE,{"disambiguationData":[TD([[makeQuery(id+"F4.imprint","IMPRINT",EDGE,{"derivedFrom":sQuery(id+"F4.wireOp",EDGE,"E28.2.2.74")}),-1.0]])]});
            var Q39;
            Q39=makeQuery(id+"F4.imprint","IMPRINT",FACE,{"disambiguationData":[TD([[makeQuery(id+"F4.imprint","IMPRINT",EDGE,{"derivedFrom":sQuery(id+"F4.wireOp",EDGE,"E28.2.2.75")}),1.0]])]});
            var Q40;
            Q40=makeQuery(id+"F4.imprint","IMPRINT",FACE,{"disambiguationData":[TD([[makeQuery(id+"F4.imprint","IMPRINT",EDGE,{"derivedFrom":sQuery(id+"F4.wireOp",EDGE,"E28.2.2.77")}),-1.0]])]});
            var Q41;
            Q41=makeQuery(id+"F4.imprint","IMPRINT",FACE,{"disambiguationData":[TD([[makeQuery(id+"F4.imprint","IMPRINT",EDGE,{"derivedFrom":sQuery(id+"F4.wireOp",EDGE,"E28.2.2.83")}),1.0]])]});
            var Q42;
            Q42=makeQuery(id+"F4.imprint","IMPRINT",FACE,{"disambiguationData":[TD([[makeQuery(id+"F4.imprint","IMPRINT",EDGE,{"derivedFrom":sQuery(id+"F4.wireOp",EDGE,"E28.2.2.90")}),-1.0]])]});
            var Q43;
            Q43=makeQuery(id+"F4.imprint","IMPRINT",FACE,{"disambiguationData":[TD([[makeQuery(id+"F4.imprint","IMPRINT",EDGE,{"derivedFrom":sQuery(id+"F4.wireOp",EDGE,"E28.2.2.97")}),1.0]])]});
            var Q44;
            Q44=makeQuery(id+"F4.imprint","IMPRINT",FACE,{"disambiguationData":[TD([[makeQuery(id+"F4.imprint","IMPRINT",EDGE,{"derivedFrom":sQuery(id+"F4.wireOp",EDGE,"E28.2.2.102")}),-1.0]])]});
            var Q45;
            Q45=makeQuery(id+"F4.imprint","IMPRINT",FACE,{"disambiguationData":[TD([[makeQuery(id+"F4.imprint","IMPRINT",EDGE,{"derivedFrom":sQuery(id+"F4.wireOp",EDGE,"E28.2.2.104")}),-1.0]])]});
            var Q46;
            Q46=makeQuery(id+"F4.imprint","IMPRINT",FACE,{"disambiguationData":[TD([[makeQuery(id+"F4.imprint","IMPRINT",EDGE,{"derivedFrom":sQuery(id+"F4.wireOp",EDGE,"E28.2.2.125")}),-1.0]])]});
            var Q47;
            Q47=makeQuery(id+"F4.imprint","IMPRINT",FACE,{"disambiguationData":[TD([[makeQuery(id+"F4.imprint","IMPRINT",EDGE,{"derivedFrom":sQuery(id+"F4.wireOp",EDGE,"E27.3.0.0")}),-1.0]])]});
            var Q48;
            Q48=makeQuery(id+"F4.imprint","IMPRINT",FACE,{"disambiguationData":[TD([[makeQuery(id+"F4.imprint","IMPRINT",EDGE,{"derivedFrom":sQuery(id+"F4.wireOp",EDGE,"E27.2.0.0")}),-1.0]])]});
            var Q49;
            Q49=makeQuery(id+"F4.imprint","IMPRINT",FACE,{"disambiguationData":[TD([[makeQuery(id+"F4.imprint","IMPRINT",EDGE,{"derivedFrom":sQuery(id+"F4.wireOp",EDGE,"E27.1.0.0")}),-1.0]])]});
            var Q50;
            Q50=makeQuery(id+"F4.imprint","IMPRINT",FACE,{"disambiguationData":[TD([[makeQuery(id+"F4.imprint","IMPRINT",EDGE,{"derivedFrom":sQuery(id+"F4.wireOp",EDGE,"E26.bottom")}),1.0]])]});
            var Q51;
            Q51=makeQuery(id+"F4.imprint","IMPRINT",FACE,{"disambiguationData":[TD([[makeQuery(id+"F4.imprint","IMPRINT",EDGE,{"derivedFrom":sQuery(id+"F4.wireOp",EDGE,"E27.1.1.0")}),-1.0]])]});
            var Q52;
            Q52=makeQuery(id+"F4.imprint","IMPRINT",FACE,{"disambiguationData":[TD([[makeQuery(id+"F4.imprint","IMPRINT",EDGE,{"derivedFrom":sQuery(id+"F4.wireOp",EDGE,"E27.2.1.0")}),-1.0]])]});
            var Q53;
            Q53=makeQuery(id+"F4.imprint","IMPRINT",FACE,{"disambiguationData":[TD([[makeQuery(id+"F4.imprint","IMPRINT",EDGE,{"derivedFrom":sQuery(id+"F4.wireOp",EDGE,"E27.3.1.0")}),-1.0]])]});
            var Q54;
            Q54=makeQuery(id+"F4.imprint","IMPRINT",FACE,{"disambiguationData":[TD([[makeQuery(id+"F4.imprint","IMPRINT",EDGE,{"derivedFrom":sQuery(id+"F4.wireOp",EDGE,"E27.4.1.0")}),-1.0]])]});
            var Q55;
            Q55=makeQuery(id+"F4.imprint","IMPRINT",FACE,{"disambiguationData":[TD([[makeQuery(id+"F4.imprint","IMPRINT",EDGE,{"derivedFrom":sQuery(id+"F4.wireOp",EDGE,"E27.4.0.0")}),-1.0]])]});
            var Q56;
            Q56=makeQuery(id+"F4.imprint","IMPRINT",FACE,{"disambiguationData":[TD([[makeQuery(id+"F4.imprint","IMPRINT",EDGE,{"derivedFrom":sQuery(id+"F4.wireOp",EDGE,"E28.1.0.91")}),-1.0]])]});
            var Q57;
            Q57=makeQuery(id+"F4.imprint","IMPRINT",FACE,{"disambiguationData":[TD([[makeQuery(id+"F4.imprint","IMPRINT",EDGE,{"derivedFrom":sQuery(id+"F4.wireOp",EDGE,"E27.0.2.0")}),-1.0]])]});
            var Q58;
            Q58=makeQuery(id+"F4.imprint","IMPRINT",FACE,{"disambiguationData":[TD([[makeQuery(id+"F4.imprint","IMPRINT",EDGE,{"derivedFrom":sQuery(id+"F4.wireOp",EDGE,"E27.1.2.0")}),-1.0]])]});
            var Q59;
            Q59=makeQuery(id+"F4.imprint","IMPRINT",FACE,{"disambiguationData":[TD([[makeQuery(id+"F4.imprint","IMPRINT",EDGE,{"derivedFrom":sQuery(id+"F4.wireOp",EDGE,"E27.3.2.0")}),-1.0]])]});
            var Q60;
            Q60=makeQuery(id+"F4.imprint","IMPRINT",FACE,{"disambiguationData":[TD([[makeQuery(id+"F4.imprint","IMPRINT",EDGE,{"derivedFrom":sQuery(id+"F4.wireOp",EDGE,"E27.4.2.0")}),-1.0]])]});
            var Q61;
            Q61=makeQuery(id+"F4.imprint","IMPRINT",FACE,{"disambiguationData":[TD([[makeQuery(id+"F4.imprint","IMPRINT",EDGE,{"derivedFrom":sQuery(id+"F4.wireOp",EDGE,"E28.1.0.94")}),-1.0]])]});
            var Q62;
            Q62=makeQuery(id+"F4.imprint","IMPRINT",FACE,{"disambiguationData":[TD([[makeQuery(id+"F4.imprint","IMPRINT",EDGE,{"derivedFrom":sQuery(id+"F4.wireOp",EDGE,"E27.0.1.0")}),-1.0]])]});
            var Q63;
            Q63=makeQuery(id+"F4.imprint","IMPRINT",FACE,{"disambiguationData":[TD([[makeQuery(id+"F4.imprint","IMPRINT",EDGE,{"derivedFrom":sQuery(id+"F4.wireOp",EDGE,"E28.1.0.107")}),1.0]])]});
            var Q64;
            Q64=makeQuery(id+"F4.imprint","IMPRINT",FACE,{"disambiguationData":[TD([[makeQuery(id+"F4.imprint","IMPRINT",EDGE,{"derivedFrom":sQuery(id+"F4.wireOp",EDGE,"E28.1.0.78")}),1.0]])]});
            var Q65;
            Q65=makeQuery(id+"F4.imprint","IMPRINT",FACE,{"disambiguationData":[TD([[makeQuery(id+"F4.imprint","IMPRINT",EDGE,{"derivedFrom":sQuery(id+"F4.wireOp",EDGE,"E28.1.0.89")}),1.0]])]});
            var Q66;
            Q66=makeQuery(id+"F4.imprint","IMPRINT",FACE,{"disambiguationData":[TD([[makeQuery(id+"F4.imprint","IMPRINT",EDGE,{"derivedFrom":sQuery(id+"F4.wireOp",EDGE,"E28.1.0.82")}),1.0]])]});
            var Q67;
            Q67=makeQuery(id+"F4.imprint","IMPRINT",FACE,{"disambiguationData":[TD([[makeQuery(id+"F4.imprint","IMPRINT",EDGE,{"derivedFrom":sQuery(id+"F4.wireOp",EDGE,"E27.4.3.0")}),-1.0]])]});
            var Q68;
            Q68=makeQuery(id+"F4.imprint","IMPRINT",FACE,{"disambiguationData":[TD([[makeQuery(id+"F4.imprint","IMPRINT",EDGE,{"derivedFrom":sQuery(id+"F4.wireOp",EDGE,"E27.3.3.0")}),-1.0]])]});
            var Q69;
            Q69=makeQuery(id+"F4.imprint","IMPRINT",FACE,{"disambiguationData":[TD([[makeQuery(id+"F4.imprint","IMPRINT",EDGE,{"derivedFrom":sQuery(id+"F4.wireOp",EDGE,"E27.2.3.0")}),-1.0]])]});
            var Q70;
            Q70=makeQuery(id+"F4.imprint","IMPRINT",FACE,{"disambiguationData":[TD([[makeQuery(id+"F4.imprint","IMPRINT",EDGE,{"derivedFrom":sQuery(id+"F4.wireOp",EDGE,"E27.1.3.0")}),-1.0]])]});
            var Q71;
            Q71=makeQuery(id+"F4.imprint","IMPRINT",FACE,{"disambiguationData":[TD([[makeQuery(id+"F4.imprint","IMPRINT",EDGE,{"derivedFrom":sQuery(id+"F4.wireOp",EDGE,"E27.0.3.0")}),-1.0]])]});
            var Q72;
            Q72=makeQuery(id+"F4.imprint","IMPRINT",FACE,{"disambiguationData":[TD([[makeQuery(id+"F4.imprint","IMPRINT",EDGE,{"derivedFrom":sQuery(id+"F4.wireOp",EDGE,"E27.0.4.0")}),-1.0]])]});
            var Q73;
            Q73=makeQuery(id+"F4.imprint","IMPRINT",FACE,{"disambiguationData":[TD([[makeQuery(id+"F4.imprint","IMPRINT",EDGE,{"derivedFrom":sQuery(id+"F4.wireOp",EDGE,"E27.1.4.0")}),-1.0]])]});
            var Q74;
            Q74=makeQuery(id+"F4.imprint","IMPRINT",FACE,{"disambiguationData":[TD([[makeQuery(id+"F4.imprint","IMPRINT",EDGE,{"derivedFrom":sQuery(id+"F4.wireOp",EDGE,"E27.2.4.0")}),-1.0]])]});
            var Q75;
            Q75=makeQuery(id+"F4.imprint","IMPRINT",FACE,{"disambiguationData":[TD([[makeQuery(id+"F4.imprint","IMPRINT",EDGE,{"derivedFrom":sQuery(id+"F4.wireOp",EDGE,"E27.4.4.0")}),-1.0]])]});
            var Q76;
            Q76=makeQuery(id+"F4.imprint","IMPRINT",FACE,{"disambiguationData":[TD([[makeQuery(id+"F4.imprint","IMPRINT",EDGE,{"derivedFrom":sQuery(id+"F4.wireOp",EDGE,"E28.1.0.90")}),-1.0]])]});
            var Q77;
            Q77=makeQuery(id+"F4.imprint","IMPRINT",FACE,{"disambiguationData":[TD([[makeQuery(id+"F4.imprint","IMPRINT",EDGE,{"derivedFrom":sQuery(id+"F4.wireOp",EDGE,"E28.1.0.77")}),-1.0]])]});
            var Q78;
            Q78=makeQuery(id+"F4.imprint","IMPRINT",FACE,{"disambiguationData":[TD([[makeQuery(id+"F4.imprint","IMPRINT",EDGE,{"derivedFrom":sQuery(id+"F4.wireOp",EDGE,"E28.1.0.75")}),1.0]])]});
            var Q79;
            Q79=makeQuery(id+"F4.imprint","IMPRINT",FACE,{"disambiguationData":[TD([[makeQuery(id+"F4.imprint","IMPRINT",EDGE,{"derivedFrom":sQuery(id+"F4.wireOp",EDGE,"E28.0.1.107")}),1.0]])]});
            var Q80;
            Q80=makeQuery(id+"F4.imprint","IMPRINT",FACE,{"disambiguationData":[TD([[makeQuery(id+"F4.imprint","IMPRINT",EDGE,{"derivedFrom":sQuery(id+"F4.wireOp",EDGE,"E28.0.1.86")}),-1.0]])]});
            var Q81;
            Q81=makeQuery(id+"F4.imprint","IMPRINT",FACE,{"disambiguationData":[TD([[makeQuery(id+"F4.imprint","IMPRINT",EDGE,{"derivedFrom":sQuery(id+"F4.wireOp",EDGE,"E28.0.1.123")}),-1.0]])]});
            var Q82;
            Q82=makeQuery(id+"F4.imprint","IMPRINT",FACE,{"disambiguationData":[TD([[makeQuery(id+"F4.imprint","IMPRINT",EDGE,{"derivedFrom":sQuery(id+"F4.wireOp",EDGE,"E28.0.1.80")}),-1.0]])]});
            var Q83;
            Q83=makeQuery(id+"F4.imprint","IMPRINT",FACE,{"disambiguationData":[TD([[makeQuery(id+"F4.imprint","IMPRINT",EDGE,{"derivedFrom":sQuery(id+"F4.wireOp",EDGE,"E28.0.1.105")}),-1.0]])]});
            var Q84;
            Q84=makeQuery(id+"F4.imprint","IMPRINT",FACE,{"disambiguationData":[TD([[makeQuery(id+"F4.imprint","IMPRINT",EDGE,{"derivedFrom":sQuery(id+"F4.wireOp",EDGE,"E27.3.4.0")}),-1.0]])]});
            var Q85;
            Q85=makeQuery(id+"F4.imprint","IMPRINT",FACE,{"disambiguationData":[TD([[makeQuery(id+"F4.imprint","IMPRINT",EDGE,{"derivedFrom":sQuery(id+"F4.wireOp",EDGE,"E28.0.1.125")}),-1.0]])]});
            var Q86;
            Q86=makeQuery(id+"F4.imprint","IMPRINT",FACE,{"disambiguationData":[TD([[makeQuery(id+"F4.imprint","IMPRINT",EDGE,{"derivedFrom":sQuery(id+"F4.wireOp",EDGE,"E28.0.1.83")}),1.0]])]});
            var Q87;
            Q87=makeQuery(id+"F4.imprint","IMPRINT",FACE,{"disambiguationData":[TD([[makeQuery(id+"F4.imprint","IMPRINT",EDGE,{"derivedFrom":sQuery(id+"F4.wireOp",EDGE,"E28.0.1.104")}),-1.0]])]});
            var Q88;
            Q88=makeQuery(id+"F4.imprint","IMPRINT",FACE,{"disambiguationData":[TD([[makeQuery(id+"F4.imprint","IMPRINT",EDGE,{"derivedFrom":sQuery(id+"F4.wireOp",EDGE,"E28.0.1.102")}),-1.0]])]});
            var Q89;
            Q89=makeQuery(id+"F4.imprint","IMPRINT",FACE,{"disambiguationData":[TD([[makeQuery(id+"F4.imprint","IMPRINT",EDGE,{"derivedFrom":sQuery(id+"F4.wireOp",EDGE,"E28.0.1.85")}),1.0]])]});
            var Q90;
            Q90=makeQuery(id+"F4.imprint","IMPRINT",FACE,{"disambiguationData":[TD([[makeQuery(id+"F4.imprint","IMPRINT",EDGE,{"derivedFrom":sQuery(id+"F4.wireOp",EDGE,"E28.0.1.71")}),-1.0]])]});
            var Q91;
            Q91=makeQuery(id+"F4.imprint","IMPRINT",FACE,{"disambiguationData":[TD([[makeQuery(id+"F4.imprint","IMPRINT",EDGE,{"derivedFrom":sQuery(id+"F4.wireOp",EDGE,"E28.0.1.76")}),-1.0]])]});
            var Q92;
            Q92=makeQuery(id+"F4.imprint","IMPRINT",FACE,{"disambiguationData":[TD([[makeQuery(id+"F4.imprint","IMPRINT",EDGE,{"derivedFrom":sQuery(id+"F4.wireOp",EDGE,"E28.0.1.89")}),1.0]])]});
            var Q93;
            Q93=makeQuery(id+"F4.imprint","IMPRINT",FACE,{"disambiguationData":[TD([[makeQuery(id+"F4.imprint","IMPRINT",EDGE,{"derivedFrom":sQuery(id+"F4.wireOp",EDGE,"E28.0.1.78")}),1.0]])]});
            var Q94;
            Q94=makeQuery(id+"F4.imprint","IMPRINT",FACE,{"disambiguationData":[TD([[makeQuery(id+"F4.imprint","IMPRINT",EDGE,{"derivedFrom":sQuery(id+"F4.wireOp",EDGE,"E28.0.1.77")}),-1.0]])]});
            var Q95;
            Q95=makeQuery(id+"F4.imprint","IMPRINT",FACE,{"disambiguationData":[TD([[makeQuery(id+"F4.imprint","IMPRINT",EDGE,{"derivedFrom":sQuery(id+"F4.wireOp",EDGE,"E28.0.1.75")}),1.0]])]});
            var Q96;
            Q96=makeQuery(id+"F4.imprint","IMPRINT",FACE,{"disambiguationData":[TD([[makeQuery(id+"F4.imprint","IMPRINT",EDGE,{"derivedFrom":sQuery(id+"F4.wireOp",EDGE,"E28.0.1.97")}),1.0]])]});
            var Q97;
            Q97=makeQuery(id+"F4.imprint","IMPRINT",FACE,{"disambiguationData":[TD([[makeQuery(id+"F4.imprint","IMPRINT",EDGE,{"derivedFrom":sQuery(id+"F4.wireOp",EDGE,"E28.0.1.74")}),-1.0]])]});
            var Q98;
            Q98=makeQuery(id+"F4.imprint","IMPRINT",FACE,{"disambiguationData":[TD([[makeQuery(id+"F4.imprint","IMPRINT",EDGE,{"derivedFrom":sQuery(id+"F4.wireOp",EDGE,"E28.0.1.87")}),-1.0]])]});
            var Q99;
            Q99=makeQuery(id+"F4.imprint","IMPRINT",FACE,{"disambiguationData":[TD([[makeQuery(id+"F4.imprint","IMPRINT",EDGE,{"derivedFrom":sQuery(id+"F4.wireOp",EDGE,"E28.0.2.80")}),-1.0]])]});
            var Q100;
            Q100=makeQuery(id+"F4.imprint","IMPRINT",FACE,{"disambiguationData":[TD([[makeQuery(id+"F4.imprint","IMPRINT",EDGE,{"derivedFrom":sQuery(id+"F4.wireOp",EDGE,"E28.0.2.123")}),-1.0]])]});
            var Q101;
            Q101=makeQuery(id+"F4.imprint","IMPRINT",FACE,{"disambiguationData":[TD([[makeQuery(id+"F4.imprint","IMPRINT",EDGE,{"derivedFrom":sQuery(id+"F4.wireOp",EDGE,"E28.0.2.105")}),-1.0]])]});
            var Q102;
            Q102=makeQuery(id+"F4.imprint","IMPRINT",FACE,{"disambiguationData":[TD([[makeQuery(id+"F4.imprint","IMPRINT",EDGE,{"derivedFrom":sQuery(id+"F4.wireOp",EDGE,"E28.0.2.125")}),-1.0]])]});
            var Q103;
            Q103=makeQuery(id+"F4.imprint","IMPRINT",FACE,{"disambiguationData":[TD([[makeQuery(id+"F4.imprint","IMPRINT",EDGE,{"derivedFrom":sQuery(id+"F4.wireOp",EDGE,"E28.1.2.159")}),1.0]])]});
            var Q104;
            Q104=makeQuery(id+"F4.imprint","IMPRINT",FACE,{"disambiguationData":[TD([[makeQuery(id+"F4.imprint","IMPRINT",EDGE,{"derivedFrom":sQuery(id+"F4.wireOp",EDGE,"E28.1.2.80")}),-1.0]])]});
            var Q105;
            Q105=makeQuery(id+"F4.imprint","IMPRINT",FACE,{"disambiguationData":[TD([[makeQuery(id+"F4.imprint","IMPRINT",EDGE,{"derivedFrom":sQuery(id+"F4.wireOp",EDGE,"E28.0.2.107")}),1.0]])]});
            var Q106;
            Q106=makeQuery(id+"F4.imprint","IMPRINT",FACE,{"disambiguationData":[TD([[makeQuery(id+"F4.imprint","IMPRINT",EDGE,{"derivedFrom":sQuery(id+"F4.wireOp",EDGE,"E28.0.2.86")}),-1.0]])]});
            var Q107;
            Q107=makeQuery(id+"F4.imprint","IMPRINT",FACE,{"disambiguationData":[TD([[makeQuery(id+"F4.imprint","IMPRINT",EDGE,{"derivedFrom":sQuery(id+"F4.wireOp",EDGE,"E28.0.2.87")}),-1.0]])]});
            var Q108;
            Q108=makeQuery(id+"F4.imprint","IMPRINT",FACE,{"disambiguationData":[TD([[makeQuery(id+"F4.imprint","IMPRINT",EDGE,{"derivedFrom":sQuery(id+"F4.wireOp",EDGE,"E28.0.2.83")}),1.0]])]});
            var Q109;
            Q109=makeQuery(id+"F4.imprint","IMPRINT",FACE,{"disambiguationData":[TD([[makeQuery(id+"F4.imprint","IMPRINT",EDGE,{"derivedFrom":sQuery(id+"F4.wireOp",EDGE,"E28.1.2.91")}),-1.0]])]});
            var Q110;
            Q110=makeQuery(id+"F4.imprint","IMPRINT",FACE,{"disambiguationData":[TD([[makeQuery(id+"F4.imprint","IMPRINT",EDGE,{"derivedFrom":sQuery(id+"F4.wireOp",EDGE,"E28.1.2.107")}),1.0]])]});
            var Q111;
            Q111=makeQuery(id+"F4.imprint","IMPRINT",FACE,{"disambiguationData":[TD([[makeQuery(id+"F4.imprint","IMPRINT",EDGE,{"derivedFrom":sQuery(id+"F4.wireOp",EDGE,"E28.0.2.71")}),-1.0]])]});
            var Q112;
            Q112=makeQuery(id+"F4.imprint","IMPRINT",FACE,{"disambiguationData":[TD([[makeQuery(id+"F4.imprint","IMPRINT",EDGE,{"derivedFrom":sQuery(id+"F4.wireOp",EDGE,"E28.0.2.104")}),-1.0]])]});
            var Q113;
            Q113=makeQuery(id+"F4.imprint","IMPRINT",FACE,{"disambiguationData":[TD([[makeQuery(id+"F4.imprint","IMPRINT",EDGE,{"derivedFrom":sQuery(id+"F4.wireOp",EDGE,"E28.1.2.94")}),-1.0]])]});
            var Q114;
            Q114=makeQuery(id+"F4.imprint","IMPRINT",FACE,{"disambiguationData":[TD([[makeQuery(id+"F4.imprint","IMPRINT",EDGE,{"derivedFrom":sQuery(id+"F4.wireOp",EDGE,"E28.1.2.78")}),1.0]])]});
            var Q115;
            Q115=makeQuery(id+"F4.imprint","IMPRINT",FACE,{"disambiguationData":[TD([[makeQuery(id+"F4.imprint","IMPRINT",EDGE,{"derivedFrom":sQuery(id+"F4.wireOp",EDGE,"E28.0.2.78")}),1.0]])]});
            var Q116;
            Q116=makeQuery(id+"F4.imprint","IMPRINT",FACE,{"disambiguationData":[TD([[makeQuery(id+"F4.imprint","IMPRINT",EDGE,{"derivedFrom":sQuery(id+"F4.wireOp",EDGE,"E28.0.2.89")}),1.0]])]});
            var Q117;
            Q117=makeQuery(id+"F4.imprint","IMPRINT",FACE,{"disambiguationData":[TD([[makeQuery(id+"F4.imprint","IMPRINT",EDGE,{"derivedFrom":sQuery(id+"F4.wireOp",EDGE,"E28.0.2.76")}),-1.0]])]});
            var Q118;
            Q118=makeQuery(id+"F4.imprint","IMPRINT",FACE,{"disambiguationData":[TD([[makeQuery(id+"F4.imprint","IMPRINT",EDGE,{"derivedFrom":sQuery(id+"F4.wireOp",EDGE,"E28.0.2.85")}),1.0]])]});
            var Q119;
            Q119=makeQuery(id+"F4.imprint","IMPRINT",FACE,{"disambiguationData":[TD([[makeQuery(id+"F4.imprint","IMPRINT",EDGE,{"derivedFrom":sQuery(id+"F4.wireOp",EDGE,"E28.1.2.82")}),1.0]])]});
            var Q120;
            Q120=makeQuery(id+"F4.imprint","IMPRINT",FACE,{"disambiguationData":[TD([[makeQuery(id+"F4.imprint","IMPRINT",EDGE,{"derivedFrom":sQuery(id+"F4.wireOp",EDGE,"E28.0.2.102")}),-1.0]])]});
            var Q121;
            Q121=makeQuery(id+"F4.imprint","IMPRINT",FACE,{"disambiguationData":[TD([[makeQuery(id+"F4.imprint","IMPRINT",EDGE,{"derivedFrom":sQuery(id+"F4.wireOp",EDGE,"E28.1.2.89")}),1.0]])]});
            var Q122;
            Q122=makeQuery(id+"F4.imprint","IMPRINT",FACE,{"disambiguationData":[TD([[makeQuery(id+"F4.imprint","IMPRINT",EDGE,{"derivedFrom":sQuery(id+"F4.wireOp",EDGE,"E28.1.2.76")}),-1.0]])]});
            var Q123;
            Q123=makeQuery(id+"F4.imprint","IMPRINT",FACE,{"disambiguationData":[TD([[makeQuery(id+"F4.imprint","IMPRINT",EDGE,{"derivedFrom":sQuery(id+"F4.wireOp",EDGE,"E28.1.2.85")}),1.0]])]});
            var Q124;
            Q124=makeQuery(id+"F4.imprint","IMPRINT",FACE,{"disambiguationData":[TD([[makeQuery(id+"F4.imprint","IMPRINT",EDGE,{"derivedFrom":sQuery(id+"F4.wireOp",EDGE,"E28.1.2.71")}),-1.0]])]});
            var Q125;
            Q125=makeQuery(id+"F4.imprint","IMPRINT",FACE,{"disambiguationData":[TD([[makeQuery(id+"F4.imprint","IMPRINT",EDGE,{"derivedFrom":sQuery(id+"F4.wireOp",EDGE,"E28.1.2.104")}),-1.0]])]});
            var Q126;
            Q126=makeQuery(id+"F4.imprint","IMPRINT",FACE,{"disambiguationData":[TD([[makeQuery(id+"F4.imprint","IMPRINT",EDGE,{"derivedFrom":sQuery(id+"F4.wireOp",EDGE,"E28.1.2.83")}),1.0]])]});
            var Q127;
            Q127=makeQuery(id+"F4.imprint","IMPRINT",FACE,{"disambiguationData":[TD([[makeQuery(id+"F4.imprint","IMPRINT",EDGE,{"derivedFrom":sQuery(id+"F4.wireOp",EDGE,"E28.1.2.125")}),-1.0]])]});
            var Q128;
            Q128=makeQuery(id+"F4.imprint","IMPRINT",FACE,{"disambiguationData":[TD([[makeQuery(id+"F4.imprint","IMPRINT",EDGE,{"derivedFrom":sQuery(id+"F4.wireOp",EDGE,"E28.1.2.105")}),-1.0]])]});
            var Q129;
            Q129=makeQuery(id+"F4.imprint","IMPRINT",FACE,{"disambiguationData":[TD([[makeQuery(id+"F4.imprint","IMPRINT",EDGE,{"derivedFrom":sQuery(id+"F4.wireOp",EDGE,"E28.1.2.123")}),-1.0]])]});
            var Q130;
            Q130=makeQuery(id+"F4.imprint","IMPRINT",FACE,{"disambiguationData":[TD([[makeQuery(id+"F4.imprint","IMPRINT",EDGE,{"derivedFrom":sQuery(id+"F4.wireOp",EDGE,"E28.1.2.86")}),-1.0]])]});
            var Q131;
            Q131=makeQuery(id+"F4.imprint","IMPRINT",FACE,{"disambiguationData":[TD([[makeQuery(id+"F4.imprint","IMPRINT",EDGE,{"derivedFrom":sQuery(id+"F4.wireOp",EDGE,"E28.1.2.87")}),-1.0]])]});
            var Q132;
            Q132=makeQuery(id+"F4.imprint","IMPRINT",FACE,{"disambiguationData":[TD([[makeQuery(id+"F4.imprint","IMPRINT",EDGE,{"derivedFrom":sQuery(id+"F4.wireOp",EDGE,"E28.1.2.102")}),-1.0]])]});
            var Q133;
            Q133=makeQuery(id+"F4.imprint","IMPRINT",FACE,{"disambiguationData":[TD([[makeQuery(id+"F4.imprint","IMPRINT",EDGE,{"derivedFrom":sQuery(id+"F4.wireOp",EDGE,"E28.2.2.82")}),1.0]])]});
            var Q134;
            Q134=makeQuery(id+"F4.imprint","IMPRINT",FACE,{"disambiguationData":[TD([[makeQuery(id+"F4.imprint","IMPRINT",EDGE,{"derivedFrom":sQuery(id+"F4.wireOp",EDGE,"E28.2.2.94")}),-1.0]])]});
            var Q135;
            Q135=makeQuery(id+"F4.imprint","IMPRINT",FACE,{"disambiguationData":[TD([[makeQuery(id+"F4.imprint","IMPRINT",EDGE,{"derivedFrom":sQuery(id+"F4.wireOp",EDGE,"E28.2.2.91")}),-1.0]])]});
            var Q136;
            Q136=makeQuery(id+"F4.imprint","IMPRINT",FACE,{"disambiguationData":[TD([[makeQuery(id+"F4.imprint","IMPRINT",EDGE,{"derivedFrom":sQuery(id+"F4.wireOp",EDGE,"E28.2.2.107")}),1.0]])]});
            var Q137;
            Q137=makeQuery(id+"F4.imprint","IMPRINT",FACE,{"disambiguationData":[TD([[makeQuery(id+"F4.imprint","IMPRINT",EDGE,{"derivedFrom":sQuery(id+"F4.wireOp",EDGE,"E28.2.2.76")}),-1.0]])]});
            var Q138;
            Q138=makeQuery(id+"F4.imprint","IMPRINT",FACE,{"disambiguationData":[TD([[makeQuery(id+"F4.imprint","IMPRINT",EDGE,{"derivedFrom":sQuery(id+"F4.wireOp",EDGE,"E28.2.2.71")}),-1.0]])]});
            var Q139;
            Q139=makeQuery(id+"F4.imprint","IMPRINT",FACE,{"disambiguationData":[TD([[makeQuery(id+"F4.imprint","IMPRINT",EDGE,{"derivedFrom":sQuery(id+"F4.wireOp",EDGE,"E28.2.2.87")}),-1.0]])]});
            var Q140;
            Q140=makeQuery(id+"F4.imprint","IMPRINT",FACE,{"disambiguationData":[TD([[makeQuery(id+"F4.imprint","IMPRINT",EDGE,{"derivedFrom":sQuery(id+"F4.wireOp",EDGE,"E28.2.2.86")}),-1.0]])]});
            var Q141;
            Q141=makeQuery(id+"F4.imprint","IMPRINT",FACE,{"disambiguationData":[TD([[makeQuery(id+"F4.imprint","IMPRINT",EDGE,{"derivedFrom":sQuery(id+"F4.wireOp",EDGE,"E28.2.2.78")}),1.0]])]});
            var Q142;
            Q142=makeQuery(id+"F4.imprint","IMPRINT",FACE,{"disambiguationData":[TD([[makeQuery(id+"F4.imprint","IMPRINT",EDGE,{"derivedFrom":sQuery(id+"F4.wireOp",EDGE,"E28.2.2.89")}),1.0]])]});
            var Q143;
            Q143=makeQuery(id+"F4.imprint","IMPRINT",FACE,{"disambiguationData":[TD([[makeQuery(id+"F4.imprint","IMPRINT",EDGE,{"derivedFrom":sQuery(id+"F4.wireOp",EDGE,"E28.2.2.85")}),1.0]])]});
            var Q144;
            Q144=makeQuery(id+"F4.imprint","IMPRINT",FACE,{"disambiguationData":[TD([[makeQuery(id+"F4.imprint","IMPRINT",EDGE,{"derivedFrom":sQuery(id+"F4.wireOp",EDGE,"E28.2.2.105")}),-1.0]])]});
            var Q145;
            Q145=makeQuery(id+"F4.imprint","IMPRINT",FACE,{"disambiguationData":[TD([[makeQuery(id+"F4.imprint","IMPRINT",EDGE,{"derivedFrom":sQuery(id+"F4.wireOp",EDGE,"E28.2.2.123")}),-1.0]])]});
            var Q146;
            Q146=makeQuery(id+"F4.imprint","IMPRINT",FACE,{"disambiguationData":[TD([[makeQuery(id+"F4.imprint","IMPRINT",EDGE,{"derivedFrom":sQuery(id+"F4.wireOp",EDGE,"E28.2.2.80")}),-1.0]])]});
            var Q147;
            Q147=makeQuery(id+"F4.imprint","IMPRINT",FACE,{"disambiguationData":[TD([[makeQuery(id+"F4.imprint","IMPRINT",EDGE,{"derivedFrom":sQuery(id+"F4.wireOp",EDGE,"E28.2.2.159")}),1.0]])]});
            var Q148;
            Q148=makeQuery(id+"F4.imprint","IMPRINT",FACE,{"disambiguationData":[TD([[makeQuery(id+"F4.imprint","IMPRINT",EDGE,{"derivedFrom":sQuery(id+"F4.wireOp",EDGE,"E28.2.1.90")}),-1.0]])]});
            var Q149;
            Q149=makeQuery(id+"F4.imprint","IMPRINT",FACE,{"disambiguationData":[TD([[makeQuery(id+"F4.imprint","IMPRINT",EDGE,{"derivedFrom":sQuery(id+"F4.wireOp",EDGE,"E28.2.1.77")}),-1.0]])]});
            var Q150;
            Q150=makeQuery(id+"F4.imprint","IMPRINT",FACE,{"disambiguationData":[TD([[makeQuery(id+"F4.imprint","IMPRINT",EDGE,{"derivedFrom":sQuery(id+"F4.wireOp",EDGE,"E28.2.1.75")}),1.0]])]});
            var Q151;
            Q151=makeQuery(id+"F4.imprint","IMPRINT",FACE,{"disambiguationData":[TD([[makeQuery(id+"F4.imprint","IMPRINT",EDGE,{"derivedFrom":sQuery(id+"F4.wireOp",EDGE,"E28.2.1.97")}),1.0]])]});
            var Q152;
            Q152=makeQuery(id+"F4.imprint","IMPRINT",FACE,{"disambiguationData":[TD([[makeQuery(id+"F4.imprint","IMPRINT",EDGE,{"derivedFrom":sQuery(id+"F4.wireOp",EDGE,"E28.2.1.89")}),1.0]])]});
            var Q153;
            Q153=makeQuery(id+"F4.imprint","IMPRINT",FACE,{"disambiguationData":[TD([[makeQuery(id+"F4.imprint","IMPRINT",EDGE,{"derivedFrom":sQuery(id+"F4.wireOp",EDGE,"E28.2.1.82")}),1.0]])]});
            var Q154;
            Q154=makeQuery(id+"F4.imprint","IMPRINT",FACE,{"disambiguationData":[TD([[makeQuery(id+"F4.imprint","IMPRINT",EDGE,{"derivedFrom":sQuery(id+"F4.wireOp",EDGE,"E28.2.1.94")}),-1.0]])]});
            var Q155;
            Q155=makeQuery(id+"F4.imprint","IMPRINT",FACE,{"disambiguationData":[TD([[makeQuery(id+"F4.imprint","IMPRINT",EDGE,{"derivedFrom":sQuery(id+"F4.wireOp",EDGE,"E28.2.1.91")}),-1.0]])]});
            var Q156;
            Q156=makeQuery(id+"F4.imprint","IMPRINT",FACE,{"disambiguationData":[TD([[makeQuery(id+"F4.imprint","IMPRINT",EDGE,{"derivedFrom":sQuery(id+"F4.wireOp",EDGE,"E28.2.1.107")}),1.0]])]});
            var Q157;
            Q157=makeQuery(id+"F4.imprint","IMPRINT",FACE,{"disambiguationData":[TD([[makeQuery(id+"F4.imprint","IMPRINT",EDGE,{"derivedFrom":sQuery(id+"F4.wireOp",EDGE,"E28.2.1.78")}),1.0]])]});
            var Q158;
            Q158=makeQuery(id+"F4.imprint","IMPRINT",FACE,{"disambiguationData":[TD([[makeQuery(id+"F4.imprint","IMPRINT",EDGE,{"derivedFrom":sQuery(id+"F4.wireOp",EDGE,"E28.2.1.86")}),-1.0]])]});
            var Q159;
            Q159=makeQuery(id+"F4.imprint","IMPRINT",FACE,{"disambiguationData":[TD([[makeQuery(id+"F4.imprint","IMPRINT",EDGE,{"derivedFrom":sQuery(id+"F4.wireOp",EDGE,"E28.2.1.87")}),-1.0]])]});
            var Q160;
            Q160=makeQuery(id+"F4.imprint","IMPRINT",FACE,{"disambiguationData":[TD([[makeQuery(id+"F4.imprint","IMPRINT",EDGE,{"derivedFrom":sQuery(id+"F4.wireOp",EDGE,"E28.2.1.85")}),1.0]])]});
            var Q161;
            Q161=makeQuery(id+"F4.imprint","IMPRINT",FACE,{"disambiguationData":[TD([[makeQuery(id+"F4.imprint","IMPRINT",EDGE,{"derivedFrom":sQuery(id+"F4.wireOp",EDGE,"E28.2.1.76")}),-1.0]])]});
            var Q162;
            Q162=makeQuery(id+"F4.imprint","IMPRINT",FACE,{"disambiguationData":[TD([[makeQuery(id+"F4.imprint","IMPRINT",EDGE,{"derivedFrom":sQuery(id+"F4.wireOp",EDGE,"E28.2.1.71")}),-1.0]])]});
            var Q163;
            Q163=makeQuery(id+"F4.imprint","IMPRINT",FACE,{"disambiguationData":[TD([[makeQuery(id+"F4.imprint","IMPRINT",EDGE,{"derivedFrom":sQuery(id+"F4.wireOp",EDGE,"E28.2.1.105")}),-1.0]])]});
            var Q164;
            Q164=makeQuery(id+"F4.imprint","IMPRINT",FACE,{"disambiguationData":[TD([[makeQuery(id+"F4.imprint","IMPRINT",EDGE,{"derivedFrom":sQuery(id+"F4.wireOp",EDGE,"E28.2.0.97")}),1.0]])]});
            var Q165;
            Q165=makeQuery(id+"F4.imprint","IMPRINT",FACE,{"disambiguationData":[TD([[makeQuery(id+"F4.imprint","IMPRINT",EDGE,{"derivedFrom":sQuery(id+"F4.wireOp",EDGE,"E28.2.0.75")}),1.0]])]});
            var Q166;
            Q166=makeQuery(id+"F4.imprint","IMPRINT",FACE,{"disambiguationData":[TD([[makeQuery(id+"F4.imprint","IMPRINT",EDGE,{"derivedFrom":sQuery(id+"F4.wireOp",EDGE,"E28.2.1.80")}),-1.0]])]});
            var Q167;
            Q167=makeQuery(id+"F4.imprint","IMPRINT",FACE,{"disambiguationData":[TD([[makeQuery(id+"F4.imprint","IMPRINT",EDGE,{"derivedFrom":sQuery(id+"F4.wireOp",EDGE,"E28.2.1.159")}),1.0]])]});
            var Q168;
            Q168=makeQuery(id+"F4.imprint","IMPRINT",FACE,{"disambiguationData":[TD([[makeQuery(id+"F4.imprint","IMPRINT",EDGE,{"derivedFrom":sQuery(id+"F4.wireOp",EDGE,"E28.2.0.90")}),-1.0]])]});
            var Q169;
            Q169=makeQuery(id+"F4.imprint","IMPRINT",FACE,{"disambiguationData":[TD([[makeQuery(id+"F4.imprint","IMPRINT",EDGE,{"derivedFrom":sQuery(id+"F4.wireOp",EDGE,"E28.2.0.77")}),-1.0]])]});
            var Q170;
            Q170=makeQuery(id+"F4.imprint","IMPRINT",FACE,{"disambiguationData":[TD([[makeQuery(id+"F4.imprint","IMPRINT",EDGE,{"derivedFrom":sQuery(id+"F4.wireOp",EDGE,"E28.2.0.89")}),1.0]])]});
            var Q171;
            Q171=makeQuery(id+"F4.imprint","IMPRINT",FACE,{"disambiguationData":[TD([[makeQuery(id+"F4.imprint","IMPRINT",EDGE,{"derivedFrom":sQuery(id+"F4.wireOp",EDGE,"E28.2.0.82")}),1.0]])]});
            var Q172;
            Q172=makeQuery(id+"F4.imprint","IMPRINT",FACE,{"disambiguationData":[TD([[makeQuery(id+"F4.imprint","IMPRINT",EDGE,{"derivedFrom":sQuery(id+"F4.wireOp",EDGE,"E28.2.0.94")}),-1.0]])]});
            var Q173;
            Q173=makeQuery(id+"F4.imprint","IMPRINT",FACE,{"disambiguationData":[TD([[makeQuery(id+"F4.imprint","IMPRINT",EDGE,{"derivedFrom":sQuery(id+"F4.wireOp",EDGE,"E28.1.0.104")}),-1.0]])]});
            var Q174;
            Q174=makeQuery(id+"F4.imprint","IMPRINT",FACE,{"disambiguationData":[TD([[makeQuery(id+"F4.imprint","IMPRINT",EDGE,{"derivedFrom":sQuery(id+"F4.wireOp",EDGE,"E28.1.0.102")}),-1.0]])]});
            var Q175;
            Q175=makeQuery(id+"F4.imprint","IMPRINT",FACE,{"disambiguationData":[TD([[makeQuery(id+"F4.imprint","IMPRINT",EDGE,{"derivedFrom":sQuery(id+"F4.wireOp",EDGE,"E28.1.0.74")}),-1.0]])]});
            var Q176;
            Q176=makeQuery(id+"F4.imprint","IMPRINT",FACE,{"disambiguationData":[TD([[makeQuery(id+"F4.imprint","IMPRINT",EDGE,{"derivedFrom":sQuery(id+"F4.wireOp",EDGE,"E28.1.0.97")}),1.0]])]});
            var Q177;
            Q177=makeQuery(id+"F4.imprint","IMPRINT",FACE,{"disambiguationData":[TD([[makeQuery(id+"F4.imprint","IMPRINT",EDGE,{"derivedFrom":sQuery(id+"F4.wireOp",EDGE,"E28.1.0.85")}),1.0]])]});
            var Q178;
            Q178=makeQuery(id+"F4.imprint","IMPRINT",FACE,{"disambiguationData":[TD([[makeQuery(id+"F4.imprint","IMPRINT",EDGE,{"derivedFrom":sQuery(id+"F4.wireOp",EDGE,"E28.2.0.71")}),-1.0]])]});
            var Q179;
            Q179=makeQuery(id+"F4.imprint","IMPRINT",FACE,{"disambiguationData":[TD([[makeQuery(id+"F4.imprint","IMPRINT",EDGE,{"derivedFrom":sQuery(id+"F4.wireOp",EDGE,"E28.2.0.87")}),-1.0]])]});
            var Q180;
            Q180=makeQuery(id+"F4.imprint","IMPRINT",FACE,{"disambiguationData":[TD([[makeQuery(id+"F4.imprint","IMPRINT",EDGE,{"derivedFrom":sQuery(id+"F4.wireOp",EDGE,"E28.2.0.86")}),-1.0]])]});
            var Q181;
            Q181=makeQuery(id+"F4.imprint","IMPRINT",FACE,{"disambiguationData":[TD([[makeQuery(id+"F4.imprint","IMPRINT",EDGE,{"derivedFrom":sQuery(id+"F4.wireOp",EDGE,"E28.2.0.107")}),1.0]])]});
            var Q182;
            Q182=makeQuery(id+"F4.imprint","IMPRINT",FACE,{"disambiguationData":[TD([[makeQuery(id+"F4.imprint","IMPRINT",EDGE,{"derivedFrom":sQuery(id+"F4.wireOp",EDGE,"E28.2.0.78")}),1.0]])]});
            var Q183;
            Q183=makeQuery(id+"F4.imprint","IMPRINT",FACE,{"disambiguationData":[TD([[makeQuery(id+"F4.imprint","IMPRINT",EDGE,{"derivedFrom":sQuery(id+"F4.wireOp",EDGE,"E28.2.0.91")}),-1.0]])]});
            var Q184;
            Q184=makeQuery(id+"F4.imprint","IMPRINT",FACE,{"disambiguationData":[TD([[makeQuery(id+"F4.imprint","IMPRINT",EDGE,{"derivedFrom":sQuery(id+"F4.wireOp",EDGE,"E28.1.0.83")}),1.0]])]});
            var Q185;
            Q185=makeQuery(id+"F4.imprint","IMPRINT",FACE,{"disambiguationData":[TD([[makeQuery(id+"F4.imprint","IMPRINT",EDGE,{"derivedFrom":sQuery(id+"F4.wireOp",EDGE,"E28.1.0.86")}),-1.0]])]});
            var Q186;
            Q186=makeQuery(id+"F4.imprint","IMPRINT",FACE,{"disambiguationData":[TD([[makeQuery(id+"F4.imprint","IMPRINT",EDGE,{"derivedFrom":sQuery(id+"F4.wireOp",EDGE,"E28.1.0.71")}),-1.0]])]});
            var Q187;
            Q187=makeQuery(id+"F4.imprint","IMPRINT",FACE,{"disambiguationData":[TD([[makeQuery(id+"F4.imprint","IMPRINT",EDGE,{"derivedFrom":sQuery(id+"F4.wireOp",EDGE,"E28.1.0.76")}),-1.0]])]});
            var Q188;
            Q188=makeQuery(id+"F4.imprint","IMPRINT",FACE,{"disambiguationData":[TD([[makeQuery(id+"F4.imprint","IMPRINT",EDGE,{"derivedFrom":sQuery(id+"F4.wireOp",EDGE,"E28.2.1.123")}),-1.0]])]});
            var Q189;
            Q189=makeQuery(id+"F4.imprint","IMPRINT",FACE,{"disambiguationData":[TD([[makeQuery(id+"F4.imprint","IMPRINT",EDGE,{"derivedFrom":sQuery(id+"F4.wireOp",EDGE,"E28.1.0.87")}),-1.0]])]});
            var Q190;
            Q190=makeQuery(id+"F4.imprint","IMPRINT",FACE,{"disambiguationData":[TD([[makeQuery(id+"F4.imprint","IMPRINT",EDGE,{"derivedFrom":sQuery(id+"F4.wireOp",EDGE,"E28.2.0.76")}),-1.0]])]});
            var Q191;
            Q191=makeQuery(id+"F4.imprint","IMPRINT",FACE,{"disambiguationData":[TD([[makeQuery(id+"F4.imprint","IMPRINT",EDGE,{"derivedFrom":sQuery(id+"F4.wireOp",EDGE,"E28.2.0.85")}),1.0]])]});
            extrude(context, id + "F5", {"entities" : qUnion([Q0, Q1, Q2, Q3, Q4, Q5, Q6, Q7, Q8, Q9, Q10, Q11, Q12, Q13, Q14, Q15, Q16, Q17, Q18, Q19, Q20, Q21, Q22, Q23, Q24, Q25, Q26, Q27, Q28, Q29, Q30, Q31, Q32, Q33, Q34, Q35, Q36, Q37, Q38, Q39, Q40, Q41, Q42, Q43, Q44, Q45, Q46, Q47, Q48, Q49, Q50, Q51, Q52, Q53, Q54, Q55, Q56, Q57, Q58, Q59, Q60, Q61, Q62, Q63, Q64, Q65, Q66, Q67, Q68, Q69, Q70, Q71, Q72, Q73, Q74, Q75, Q76, Q77, Q78, Q79, Q80, Q81, Q82, Q83, Q84, Q85, Q86, Q87, Q88, Q89, Q90, Q91, Q92, Q93, Q94, Q95, Q96, Q97, Q98, Q99, Q100, Q101, Q102, Q103, Q104, Q105, Q106, Q107, Q108, Q109, Q110, Q111, Q112, Q113, Q114, Q115, Q116, Q117, Q118, Q119, Q120, Q121, Q122, Q123, Q124, Q125, Q126, Q127, Q128, Q129, Q130, Q131, Q132, Q133, Q134, Q135, Q136, Q137, Q138, Q139, Q140, Q141, Q142, Q143, Q144, Q145, Q146, Q147, Q148, Q149, Q150, Q151, Q152, Q153, Q154, Q155, Q156, Q157, Q158, Q159, Q160, Q161, Q162, Q163, Q164, Q165, Q166, Q167, Q168, Q169, Q170, Q171, Q172, Q173, Q174, Q175, Q176, Q177, Q178, Q179, Q180, Q181, Q182, Q183, Q184, Q185, Q186, Q187, Q188, Q189, Q190, Q191]), "operationType" : NewBodyOperationType.REMOVE, "oppositeDirection" : true, "depth" : 228.6 * mm, "offsetDistance" : 25.4 * mm});
        }
    });
